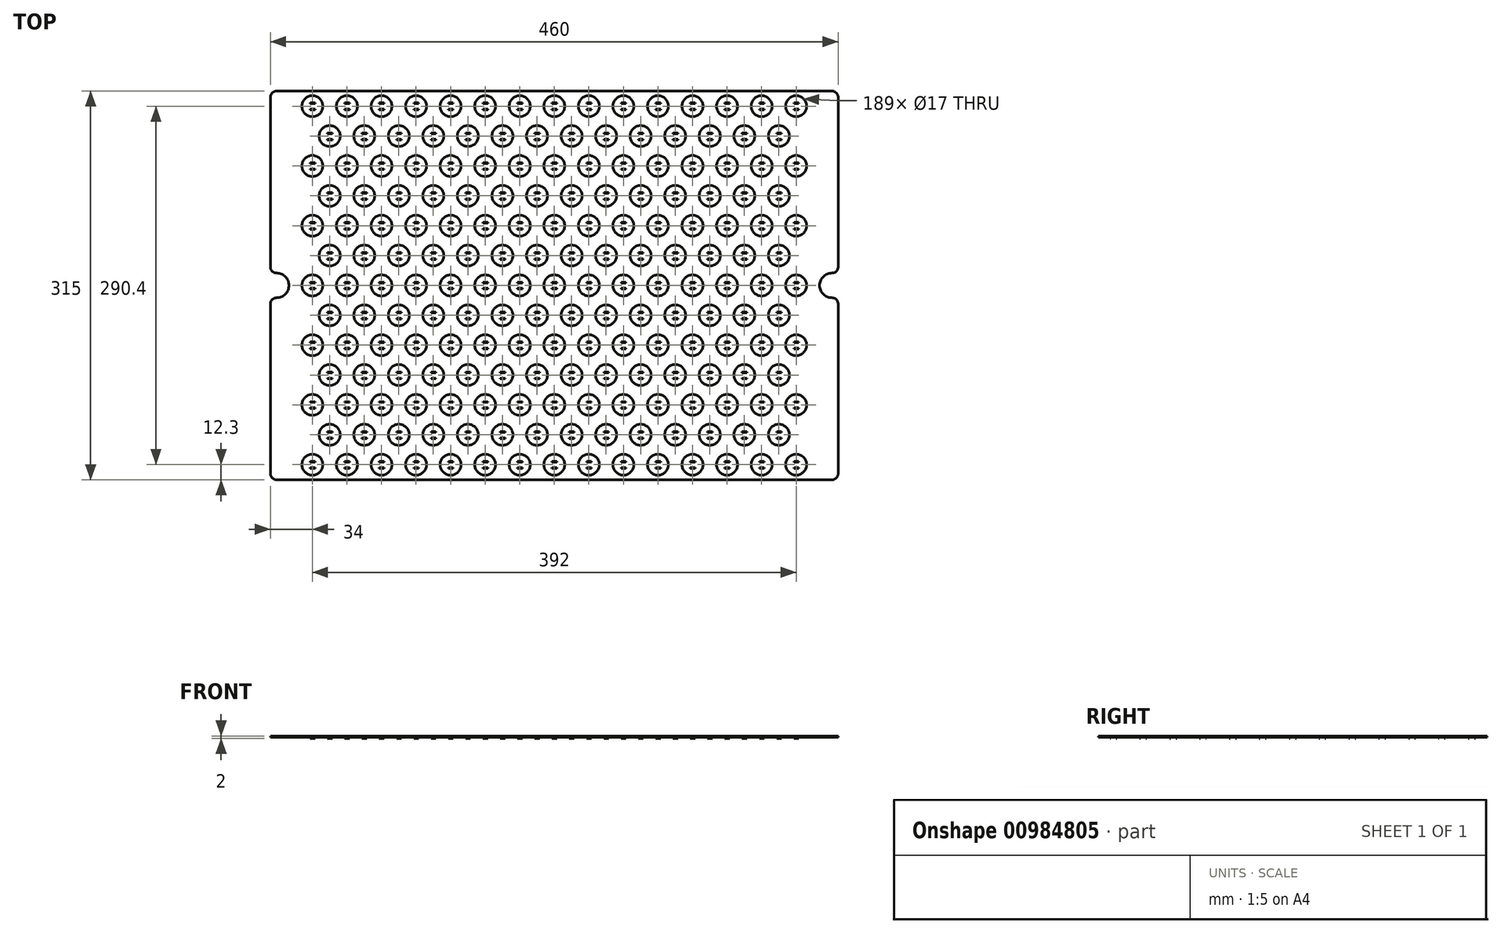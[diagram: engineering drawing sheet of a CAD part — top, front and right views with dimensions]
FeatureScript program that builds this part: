
annotation { "Feature Type Name" : "Feature", "Feature Type Description" : "" }
export const myFeature = defineFeature(function(context is Context, id is Id, definition is map)
    precondition{}
    {
        {
            var Q0;
            Q0=qCreatedBy(makeId("Top.planeOp"),FACE);
            var sketch = newSketch(context, id + "F0", { "sketchPlane" : qUnion([Q0])});
            skLineSegment(sketch, "E0.bottom", {"start": v(-225, 157.5) * mm, "end": v(225, 157.5) * mm});
            skLineSegment(sketch, "E0.top", {"start": v(-225, -157.5) * mm, "end": v(225, -157.5) * mm});
            skLineSegment(sketch, "E0.left", {"start": v(-230, 152.5) * mm, "end": v(-230, 15) * mm});
            skLineSegment(sketch, "E0.right", {"start": v(230, 152.5) * mm, "end": v(230, 15) * mm});
            skPoint(sketch, "E1.visualSharp", {"position": v(-230, 157.5) * mm});
            skArc(sketch, "E1.filletArc", {"start": v(-225, 157.5) * mm, "mid": v(-228.54, 156.04) * mm, "end": v(-230, 152.5) * mm});
            skPoint(sketch, "E2.visualSharp", {"position": v(230, 157.5) * mm});
            skArc(sketch, "E2.filletArc", {"start": v(230, 152.5) * mm, "mid": v(228.54, 156.04) * mm, "end": v(225, 157.5) * mm});
            skPoint(sketch, "E3.visualSharp", {"position": v(230, -157.5) * mm});
            skArc(sketch, "E3.filletArc", {"start": v(225, -157.5) * mm, "mid": v(228.54, -156.04) * mm, "end": v(230, -152.5) * mm});
            skPoint(sketch, "E4.visualSharp", {"position": v(-230, -157.5) * mm});
            skArc(sketch, "E4.filletArc", {"start": v(-230, -152.5) * mm, "mid": v(-228.54, -156.04) * mm, "end": v(-225, -157.5) * mm});
            skArc(sketch, "E5", {"start": v(-225, 10) * mm, "mid": v(-215, 0) * mm, "end": v(-225, -10) * mm});
            skArc(sketch, "E6", {"start": v(225, 10) * mm, "mid": v(215, 0) * mm, "end": v(225, -10) * mm});
            skLineSegment(sketch, "E7.trimOffspring", {"start": v(-230, -15) * mm, "end": v(-230, -152.5) * mm});
            skLineSegment(sketch, "E8.trimOffspring", {"start": v(230, -15) * mm, "end": v(230, -152.5) * mm});
            skPoint(sketch, "E9.visualSharp", {"position": v(230, 8.66) * mm});
            skArc(sketch, "E9.filletArc", {"start": v(225, 10) * mm, "mid": v(228.54, 11.46) * mm, "end": v(230, 15) * mm});
            skPoint(sketch, "E10.visualSharp", {"position": v(230, -8.66) * mm});
            skArc(sketch, "E10.filletArc", {"start": v(230, -15) * mm, "mid": v(228.54, -11.46) * mm, "end": v(225, -10) * mm});
            skPoint(sketch, "E11.visualSharp", {"position": v(-230, 8.66) * mm});
            skArc(sketch, "E11.filletArc", {"start": v(-230, 15) * mm, "mid": v(-228.54, 11.46) * mm, "end": v(-225, 10) * mm});
            skPoint(sketch, "E12.visualSharp", {"position": v(-230, -8.66) * mm});
            skArc(sketch, "E12.filletArc", {"start": v(-225, -10) * mm, "mid": v(-228.54, -11.46) * mm, "end": v(-230, -15) * mm});
            skCircle(sketch, "E13", {"center": v(-196, 145.2) * mm, "radius": 8.5 * mm});
            skCircle(sketch, "E14", {"center": v(-182, 121) * mm, "radius": 8.5 * mm});
            skCircle(sketch, "E15.0.1.0", {"center": v(-196, 96.8) * mm, "radius": 8.5 * mm});
            skCircle(sketch, "E15.0.2.0", {"center": v(-196, 48.4) * mm, "radius": 8.5 * mm});
            skCircle(sketch, "E15.0.3.0", {"center": v(-196, 0) * mm, "radius": 8.5 * mm});
            skCircle(sketch, "E15.0.4.0", {"center": v(-196, -48.4) * mm, "radius": 8.5 * mm});
            skCircle(sketch, "E15.0.5.0", {"center": v(-196, -96.8) * mm, "radius": 8.5 * mm});
            skCircle(sketch, "E15.0.6.0", {"center": v(-196, -145.2) * mm, "radius": 8.5 * mm});
            skCircle(sketch, "E15.1.0.0", {"center": v(-168, 145.2) * mm, "radius": 8.5 * mm});
            skCircle(sketch, "E15.1.1.0", {"center": v(-168, 96.8) * mm, "radius": 8.5 * mm});
            skCircle(sketch, "E15.1.2.0", {"center": v(-168, 48.4) * mm, "radius": 8.5 * mm});
            skCircle(sketch, "E15.1.3.0", {"center": v(-168, 0) * mm, "radius": 8.5 * mm});
            skCircle(sketch, "E15.1.4.0", {"center": v(-168, -48.4) * mm, "radius": 8.5 * mm});
            skCircle(sketch, "E15.1.5.0", {"center": v(-168, -96.8) * mm, "radius": 8.5 * mm});
            skCircle(sketch, "E15.1.6.0", {"center": v(-168, -145.2) * mm, "radius": 8.5 * mm});
            skCircle(sketch, "E15.2.0.0", {"center": v(-140, 145.2) * mm, "radius": 8.5 * mm});
            skCircle(sketch, "E15.2.1.0", {"center": v(-140, 96.8) * mm, "radius": 8.5 * mm});
            skCircle(sketch, "E15.2.2.0", {"center": v(-140, 48.4) * mm, "radius": 8.5 * mm});
            skCircle(sketch, "E15.2.3.0", {"center": v(-140, 0) * mm, "radius": 8.5 * mm});
            skCircle(sketch, "E15.2.4.0", {"center": v(-140, -48.4) * mm, "radius": 8.5 * mm});
            skCircle(sketch, "E15.2.5.0", {"center": v(-140, -96.8) * mm, "radius": 8.5 * mm});
            skCircle(sketch, "E15.2.6.0", {"center": v(-140, -145.2) * mm, "radius": 8.5 * mm});
            skCircle(sketch, "E15.3.0.0", {"center": v(-112, 145.2) * mm, "radius": 8.5 * mm});
            skCircle(sketch, "E15.3.1.0", {"center": v(-112, 96.8) * mm, "radius": 8.5 * mm});
            skCircle(sketch, "E15.3.2.0", {"center": v(-112, 48.4) * mm, "radius": 8.5 * mm});
            skCircle(sketch, "E15.3.3.0", {"center": v(-112, 0) * mm, "radius": 8.5 * mm});
            skCircle(sketch, "E15.3.4.0", {"center": v(-112, -48.4) * mm, "radius": 8.5 * mm});
            skCircle(sketch, "E15.3.5.0", {"center": v(-112, -96.8) * mm, "radius": 8.5 * mm});
            skCircle(sketch, "E15.3.6.0", {"center": v(-112, -145.2) * mm, "radius": 8.5 * mm});
            skCircle(sketch, "E15.4.0.0", {"center": v(-84, 145.2) * mm, "radius": 8.5 * mm});
            skCircle(sketch, "E15.4.1.0", {"center": v(-84, 96.8) * mm, "radius": 8.5 * mm});
            skCircle(sketch, "E15.4.2.0", {"center": v(-84, 48.4) * mm, "radius": 8.5 * mm});
            skCircle(sketch, "E15.4.3.0", {"center": v(-84, 0) * mm, "radius": 8.5 * mm});
            skCircle(sketch, "E15.4.4.0", {"center": v(-84, -48.4) * mm, "radius": 8.5 * mm});
            skCircle(sketch, "E15.4.5.0", {"center": v(-84, -96.8) * mm, "radius": 8.5 * mm});
            skCircle(sketch, "E15.4.6.0", {"center": v(-84, -145.2) * mm, "radius": 8.5 * mm});
            skCircle(sketch, "E15.5.0.0", {"center": v(-56, 145.2) * mm, "radius": 8.5 * mm});
            skCircle(sketch, "E15.5.1.0", {"center": v(-56, 96.8) * mm, "radius": 8.5 * mm});
            skCircle(sketch, "E15.5.2.0", {"center": v(-56, 48.4) * mm, "radius": 8.5 * mm});
            skCircle(sketch, "E15.5.3.0", {"center": v(-56, 0) * mm, "radius": 8.5 * mm});
            skCircle(sketch, "E15.5.4.0", {"center": v(-56, -48.4) * mm, "radius": 8.5 * mm});
            skCircle(sketch, "E15.5.5.0", {"center": v(-56, -96.8) * mm, "radius": 8.5 * mm});
            skCircle(sketch, "E15.5.6.0", {"center": v(-56, -145.2) * mm, "radius": 8.5 * mm});
            skCircle(sketch, "E15.6.0.0", {"center": v(-28, 145.2) * mm, "radius": 8.5 * mm});
            skCircle(sketch, "E15.6.1.0", {"center": v(-28, 96.8) * mm, "radius": 8.5 * mm});
            skCircle(sketch, "E15.6.2.0", {"center": v(-28, 48.4) * mm, "radius": 8.5 * mm});
            skCircle(sketch, "E15.6.3.0", {"center": v(-28, 0) * mm, "radius": 8.5 * mm});
            skCircle(sketch, "E15.6.4.0", {"center": v(-28, -48.4) * mm, "radius": 8.5 * mm});
            skCircle(sketch, "E15.6.5.0", {"center": v(-28, -96.8) * mm, "radius": 8.5 * mm});
            skCircle(sketch, "E15.6.6.0", {"center": v(-28, -145.2) * mm, "radius": 8.5 * mm});
            skCircle(sketch, "E15.7.0.0", {"center": v(0, 145.2) * mm, "radius": 8.5 * mm});
            skCircle(sketch, "E15.7.1.0", {"center": v(0, 96.8) * mm, "radius": 8.5 * mm});
            skCircle(sketch, "E15.7.2.0", {"center": v(0, 48.4) * mm, "radius": 8.5 * mm});
            skCircle(sketch, "E15.7.3.0", {"center": v(0, 0) * mm, "radius": 8.5 * mm});
            skCircle(sketch, "E15.7.4.0", {"center": v(0, -48.4) * mm, "radius": 8.5 * mm});
            skCircle(sketch, "E15.7.5.0", {"center": v(0, -96.8) * mm, "radius": 8.5 * mm});
            skCircle(sketch, "E15.7.6.0", {"center": v(0, -145.2) * mm, "radius": 8.5 * mm});
            skCircle(sketch, "E15.8.0.0", {"center": v(28, 145.2) * mm, "radius": 8.5 * mm});
            skCircle(sketch, "E15.8.1.0", {"center": v(28, 96.8) * mm, "radius": 8.5 * mm});
            skCircle(sketch, "E15.8.2.0", {"center": v(28, 48.4) * mm, "radius": 8.5 * mm});
            skCircle(sketch, "E15.8.3.0", {"center": v(28, 0) * mm, "radius": 8.5 * mm});
            skCircle(sketch, "E15.8.4.0", {"center": v(28, -48.4) * mm, "radius": 8.5 * mm});
            skCircle(sketch, "E15.8.5.0", {"center": v(28, -96.8) * mm, "radius": 8.5 * mm});
            skCircle(sketch, "E15.8.6.0", {"center": v(28, -145.2) * mm, "radius": 8.5 * mm});
            skCircle(sketch, "E15.9.0.0", {"center": v(56, 145.2) * mm, "radius": 8.5 * mm});
            skCircle(sketch, "E15.9.1.0", {"center": v(56, 96.8) * mm, "radius": 8.5 * mm});
            skCircle(sketch, "E15.9.2.0", {"center": v(56, 48.4) * mm, "radius": 8.5 * mm});
            skCircle(sketch, "E15.9.3.0", {"center": v(56, 0) * mm, "radius": 8.5 * mm});
            skCircle(sketch, "E15.9.4.0", {"center": v(56, -48.4) * mm, "radius": 8.5 * mm});
            skCircle(sketch, "E15.9.5.0", {"center": v(56, -96.8) * mm, "radius": 8.5 * mm});
            skCircle(sketch, "E15.9.6.0", {"center": v(56, -145.2) * mm, "radius": 8.5 * mm});
            skCircle(sketch, "E15.10.0.0", {"center": v(84, 145.2) * mm, "radius": 8.5 * mm});
            skCircle(sketch, "E15.10.1.0", {"center": v(84, 96.8) * mm, "radius": 8.5 * mm});
            skCircle(sketch, "E15.10.2.0", {"center": v(84, 48.4) * mm, "radius": 8.5 * mm});
            skCircle(sketch, "E15.10.3.0", {"center": v(84, 0) * mm, "radius": 8.5 * mm});
            skCircle(sketch, "E15.10.4.0", {"center": v(84, -48.4) * mm, "radius": 8.5 * mm});
            skCircle(sketch, "E15.10.5.0", {"center": v(84, -96.8) * mm, "radius": 8.5 * mm});
            skCircle(sketch, "E15.10.6.0", {"center": v(84, -145.2) * mm, "radius": 8.5 * mm});
            skCircle(sketch, "E15.11.0.0", {"center": v(112, 145.2) * mm, "radius": 8.5 * mm});
            skCircle(sketch, "E15.11.1.0", {"center": v(112, 96.8) * mm, "radius": 8.5 * mm});
            skCircle(sketch, "E15.11.2.0", {"center": v(112, 48.4) * mm, "radius": 8.5 * mm});
            skCircle(sketch, "E15.11.3.0", {"center": v(112, 0) * mm, "radius": 8.5 * mm});
            skCircle(sketch, "E15.11.4.0", {"center": v(112, -48.4) * mm, "radius": 8.5 * mm});
            skCircle(sketch, "E15.11.5.0", {"center": v(112, -96.8) * mm, "radius": 8.5 * mm});
            skCircle(sketch, "E15.11.6.0", {"center": v(112, -145.2) * mm, "radius": 8.5 * mm});
            skCircle(sketch, "E15.12.0.0", {"center": v(140, 145.2) * mm, "radius": 8.5 * mm});
            skCircle(sketch, "E15.12.1.0", {"center": v(140, 96.8) * mm, "radius": 8.5 * mm});
            skCircle(sketch, "E15.12.2.0", {"center": v(140, 48.4) * mm, "radius": 8.5 * mm});
            skCircle(sketch, "E15.12.3.0", {"center": v(140, 0) * mm, "radius": 8.5 * mm});
            skCircle(sketch, "E15.12.4.0", {"center": v(140, -48.4) * mm, "radius": 8.5 * mm});
            skCircle(sketch, "E15.12.5.0", {"center": v(140, -96.8) * mm, "radius": 8.5 * mm});
            skCircle(sketch, "E15.12.6.0", {"center": v(140, -145.2) * mm, "radius": 8.5 * mm});
            skCircle(sketch, "E15.13.0.0", {"center": v(168, 145.2) * mm, "radius": 8.5 * mm});
            skCircle(sketch, "E15.13.1.0", {"center": v(168, 96.8) * mm, "radius": 8.5 * mm});
            skCircle(sketch, "E15.13.2.0", {"center": v(168, 48.4) * mm, "radius": 8.5 * mm});
            skCircle(sketch, "E15.13.3.0", {"center": v(168, 0) * mm, "radius": 8.5 * mm});
            skCircle(sketch, "E15.13.4.0", {"center": v(168, -48.4) * mm, "radius": 8.5 * mm});
            skCircle(sketch, "E15.13.5.0", {"center": v(168, -96.8) * mm, "radius": 8.5 * mm});
            skCircle(sketch, "E15.13.6.0", {"center": v(168, -145.2) * mm, "radius": 8.5 * mm});
            skCircle(sketch, "E15.14.0.0", {"center": v(196, 145.2) * mm, "radius": 8.5 * mm});
            skCircle(sketch, "E15.14.1.0", {"center": v(196, 96.8) * mm, "radius": 8.5 * mm});
            skCircle(sketch, "E15.14.2.0", {"center": v(196, 48.4) * mm, "radius": 8.5 * mm});
            skCircle(sketch, "E15.14.3.0", {"center": v(196, 0) * mm, "radius": 8.5 * mm});
            skCircle(sketch, "E15.14.4.0", {"center": v(196, -48.4) * mm, "radius": 8.5 * mm});
            skCircle(sketch, "E15.14.5.0", {"center": v(196, -96.8) * mm, "radius": 8.5 * mm});
            skCircle(sketch, "E15.14.6.0", {"center": v(196, -145.2) * mm, "radius": 8.5 * mm});
            skLineSegment(sketch, "E15.direction1", {"start": v(-196, 145.2) * mm, "end": v(-168, 145.2) * mm, "construction": true});
            skLineSegment(sketch, "E15.direction2", {"start": v(-196, 145.2) * mm, "end": v(-196, 96.8) * mm, "construction": true});
            skCircle(sketch, "E16.0.1.0", {"center": v(-182, 72.6) * mm, "radius": 8.5 * mm});
            skCircle(sketch, "E16.0.2.0", {"center": v(-182, 24.2) * mm, "radius": 8.5 * mm});
            skCircle(sketch, "E16.0.3.0", {"center": v(-182, -24.2) * mm, "radius": 8.5 * mm});
            skCircle(sketch, "E16.0.4.0", {"center": v(-182, -72.6) * mm, "radius": 8.5 * mm});
            skCircle(sketch, "E16.0.5.0", {"center": v(-182, -121) * mm, "radius": 8.5 * mm});
            skCircle(sketch, "E16.1.0.0", {"center": v(-154, 121) * mm, "radius": 8.5 * mm});
            skCircle(sketch, "E16.1.1.0", {"center": v(-154, 72.6) * mm, "radius": 8.5 * mm});
            skCircle(sketch, "E16.1.2.0", {"center": v(-154, 24.2) * mm, "radius": 8.5 * mm});
            skCircle(sketch, "E16.1.3.0", {"center": v(-154, -24.2) * mm, "radius": 8.5 * mm});
            skCircle(sketch, "E16.1.4.0", {"center": v(-154, -72.6) * mm, "radius": 8.5 * mm});
            skCircle(sketch, "E16.1.5.0", {"center": v(-154, -121) * mm, "radius": 8.5 * mm});
            skCircle(sketch, "E16.2.0.0", {"center": v(-126, 121) * mm, "radius": 8.5 * mm});
            skCircle(sketch, "E16.2.1.0", {"center": v(-126, 72.6) * mm, "radius": 8.5 * mm});
            skCircle(sketch, "E16.2.2.0", {"center": v(-126, 24.2) * mm, "radius": 8.5 * mm});
            skCircle(sketch, "E16.2.3.0", {"center": v(-126, -24.2) * mm, "radius": 8.5 * mm});
            skCircle(sketch, "E16.2.4.0", {"center": v(-126, -72.6) * mm, "radius": 8.5 * mm});
            skCircle(sketch, "E16.2.5.0", {"center": v(-126, -121) * mm, "radius": 8.5 * mm});
            skCircle(sketch, "E16.3.0.0", {"center": v(-98, 121) * mm, "radius": 8.5 * mm});
            skCircle(sketch, "E16.3.1.0", {"center": v(-98, 72.6) * mm, "radius": 8.5 * mm});
            skCircle(sketch, "E16.3.2.0", {"center": v(-98, 24.2) * mm, "radius": 8.5 * mm});
            skCircle(sketch, "E16.3.3.0", {"center": v(-98, -24.2) * mm, "radius": 8.5 * mm});
            skCircle(sketch, "E16.3.4.0", {"center": v(-98, -72.6) * mm, "radius": 8.5 * mm});
            skCircle(sketch, "E16.3.5.0", {"center": v(-98, -121) * mm, "radius": 8.5 * mm});
            skCircle(sketch, "E16.4.0.0", {"center": v(-70, 121) * mm, "radius": 8.5 * mm});
            skCircle(sketch, "E16.4.1.0", {"center": v(-70, 72.6) * mm, "radius": 8.5 * mm});
            skCircle(sketch, "E16.4.2.0", {"center": v(-70, 24.2) * mm, "radius": 8.5 * mm});
            skCircle(sketch, "E16.4.3.0", {"center": v(-70, -24.2) * mm, "radius": 8.5 * mm});
            skCircle(sketch, "E16.4.4.0", {"center": v(-70, -72.6) * mm, "radius": 8.5 * mm});
            skCircle(sketch, "E16.4.5.0", {"center": v(-70, -121) * mm, "radius": 8.5 * mm});
            skCircle(sketch, "E16.5.0.0", {"center": v(-42, 121) * mm, "radius": 8.5 * mm});
            skCircle(sketch, "E16.5.1.0", {"center": v(-42, 72.6) * mm, "radius": 8.5 * mm});
            skCircle(sketch, "E16.5.2.0", {"center": v(-42, 24.2) * mm, "radius": 8.5 * mm});
            skCircle(sketch, "E16.5.3.0", {"center": v(-42, -24.2) * mm, "radius": 8.5 * mm});
            skCircle(sketch, "E16.5.4.0", {"center": v(-42, -72.6) * mm, "radius": 8.5 * mm});
            skCircle(sketch, "E16.5.5.0", {"center": v(-42, -121) * mm, "radius": 8.5 * mm});
            skCircle(sketch, "E16.6.0.0", {"center": v(-14, 121) * mm, "radius": 8.5 * mm});
            skCircle(sketch, "E16.6.1.0", {"center": v(-14, 72.6) * mm, "radius": 8.5 * mm});
            skCircle(sketch, "E16.6.2.0", {"center": v(-14, 24.2) * mm, "radius": 8.5 * mm});
            skCircle(sketch, "E16.6.3.0", {"center": v(-14, -24.2) * mm, "radius": 8.5 * mm});
            skCircle(sketch, "E16.6.4.0", {"center": v(-14, -72.6) * mm, "radius": 8.5 * mm});
            skCircle(sketch, "E16.6.5.0", {"center": v(-14, -121) * mm, "radius": 8.5 * mm});
            skCircle(sketch, "E16.7.0.0", {"center": v(14, 121) * mm, "radius": 8.5 * mm});
            skCircle(sketch, "E16.7.1.0", {"center": v(14, 72.6) * mm, "radius": 8.5 * mm});
            skCircle(sketch, "E16.7.2.0", {"center": v(14, 24.2) * mm, "radius": 8.5 * mm});
            skCircle(sketch, "E16.7.3.0", {"center": v(14, -24.2) * mm, "radius": 8.5 * mm});
            skCircle(sketch, "E16.7.4.0", {"center": v(14, -72.6) * mm, "radius": 8.5 * mm});
            skCircle(sketch, "E16.7.5.0", {"center": v(14, -121) * mm, "radius": 8.5 * mm});
            skCircle(sketch, "E16.8.0.0", {"center": v(42, 121) * mm, "radius": 8.5 * mm});
            skCircle(sketch, "E16.8.1.0", {"center": v(42, 72.6) * mm, "radius": 8.5 * mm});
            skCircle(sketch, "E16.8.2.0", {"center": v(42, 24.2) * mm, "radius": 8.5 * mm});
            skCircle(sketch, "E16.8.3.0", {"center": v(42, -24.2) * mm, "radius": 8.5 * mm});
            skCircle(sketch, "E16.8.4.0", {"center": v(42, -72.6) * mm, "radius": 8.5 * mm});
            skCircle(sketch, "E16.8.5.0", {"center": v(42, -121) * mm, "radius": 8.5 * mm});
            skCircle(sketch, "E16.9.0.0", {"center": v(70, 121) * mm, "radius": 8.5 * mm});
            skCircle(sketch, "E16.9.1.0", {"center": v(70, 72.6) * mm, "radius": 8.5 * mm});
            skCircle(sketch, "E16.9.2.0", {"center": v(70, 24.2) * mm, "radius": 8.5 * mm});
            skCircle(sketch, "E16.9.3.0", {"center": v(70, -24.2) * mm, "radius": 8.5 * mm});
            skCircle(sketch, "E16.9.4.0", {"center": v(70, -72.6) * mm, "radius": 8.5 * mm});
            skCircle(sketch, "E16.9.5.0", {"center": v(70, -121) * mm, "radius": 8.5 * mm});
            skCircle(sketch, "E16.10.0.0", {"center": v(98, 121) * mm, "radius": 8.5 * mm});
            skCircle(sketch, "E16.10.1.0", {"center": v(98, 72.6) * mm, "radius": 8.5 * mm});
            skCircle(sketch, "E16.10.2.0", {"center": v(98, 24.2) * mm, "radius": 8.5 * mm});
            skCircle(sketch, "E16.10.3.0", {"center": v(98, -24.2) * mm, "radius": 8.5 * mm});
            skCircle(sketch, "E16.10.4.0", {"center": v(98, -72.6) * mm, "radius": 8.5 * mm});
            skCircle(sketch, "E16.10.5.0", {"center": v(98, -121) * mm, "radius": 8.5 * mm});
            skCircle(sketch, "E16.11.0.0", {"center": v(126, 121) * mm, "radius": 8.5 * mm});
            skCircle(sketch, "E16.11.1.0", {"center": v(126, 72.6) * mm, "radius": 8.5 * mm});
            skCircle(sketch, "E16.11.2.0", {"center": v(126, 24.2) * mm, "radius": 8.5 * mm});
            skCircle(sketch, "E16.11.3.0", {"center": v(126, -24.2) * mm, "radius": 8.5 * mm});
            skCircle(sketch, "E16.11.4.0", {"center": v(126, -72.6) * mm, "radius": 8.5 * mm});
            skCircle(sketch, "E16.11.5.0", {"center": v(126, -121) * mm, "radius": 8.5 * mm});
            skCircle(sketch, "E16.12.0.0", {"center": v(154, 121) * mm, "radius": 8.5 * mm});
            skCircle(sketch, "E16.12.1.0", {"center": v(154, 72.6) * mm, "radius": 8.5 * mm});
            skCircle(sketch, "E16.12.2.0", {"center": v(154, 24.2) * mm, "radius": 8.5 * mm});
            skCircle(sketch, "E16.12.3.0", {"center": v(154, -24.2) * mm, "radius": 8.5 * mm});
            skCircle(sketch, "E16.12.4.0", {"center": v(154, -72.6) * mm, "radius": 8.5 * mm});
            skCircle(sketch, "E16.12.5.0", {"center": v(154, -121) * mm, "radius": 8.5 * mm});
            skCircle(sketch, "E16.13.0.0", {"center": v(182, 121) * mm, "radius": 8.5 * mm});
            skCircle(sketch, "E16.13.1.0", {"center": v(182, 72.6) * mm, "radius": 8.5 * mm});
            skCircle(sketch, "E16.13.2.0", {"center": v(182, 24.2) * mm, "radius": 8.5 * mm});
            skCircle(sketch, "E16.13.3.0", {"center": v(182, -24.2) * mm, "radius": 8.5 * mm});
            skCircle(sketch, "E16.13.4.0", {"center": v(182, -72.6) * mm, "radius": 8.5 * mm});
            skCircle(sketch, "E16.13.5.0", {"center": v(182, -121) * mm, "radius": 8.5 * mm});
            skLineSegment(sketch, "E16.direction1", {"start": v(-182, 121) * mm, "end": v(-154, 121) * mm, "construction": true});
            skLineSegment(sketch, "E16.direction2", {"start": v(-182, 121) * mm, "end": v(-182, 72.6) * mm, "construction": true});
            skSolve(sketch);
        }
        {
            var Q0;
            Q0=makeQuery(id+"F0.imprint","IMPRINT",FACE,{"disambiguationData":[TD([[makeQuery(id+"F0.imprint","IMPRINT",EDGE,{"derivedFrom":sQuery(id+"F0.wireOp",EDGE,"E0.bottom")}),-1.0]])]});
            extrude(context, id + "F1", {"entities" : qUnion([Q0]), "depth" : 1 * mm, "offsetDistance" : 25 * mm});
        }
        {
            var Q0;
            Q0=makeQuery(id+"F1.opExtrude","CAP_FACE",FACE,{"disambiguationData":[OSD([sQuery(id+"F0.wireOp",EDGE,"E0.bottom"),sQuery(id+"F0.wireOp",EDGE,"E0.top"),sQuery(id+"F0.wireOp",EDGE,"E0.left"),sQuery(id+"F0.wireOp",EDGE,"E0.right"),sQuery(id+"F0.wireOp",EDGE,"E1.filletArc"),sQuery(id+"F0.wireOp",EDGE,"E2.filletArc"),sQuery(id+"F0.wireOp",EDGE,"E3.filletArc"),sQuery(id+"F0.wireOp",EDGE,"E4.filletArc"),sQuery(id+"F0.wireOp",EDGE,"E5"),sQuery(id+"F0.wireOp",EDGE,"E6"),sQuery(id+"F0.wireOp",EDGE,"E7.trimOffspring"),sQuery(id+"F0.wireOp",EDGE,"E8.trimOffspring"),sQuery(id+"F0.wireOp",EDGE,"E9.filletArc"),sQuery(id+"F0.wireOp",EDGE,"E10.filletArc"),sQuery(id+"F0.wireOp",EDGE,"E11.filletArc"),sQuery(id+"F0.wireOp",EDGE,"E12.filletArc"),sQuery(id+"F0.wireOp",EDGE,"E13"),sQuery(id+"F0.wireOp",EDGE,"E14"),sQuery(id+"F0.wireOp",EDGE,"E15.0.1.0"),sQuery(id+"F0.wireOp",EDGE,"E15.0.2.0"),sQuery(id+"F0.wireOp",EDGE,"E15.0.3.0"),sQuery(id+"F0.wireOp",EDGE,"E15.0.4.0"),sQuery(id+"F0.wireOp",EDGE,"E15.0.5.0"),sQuery(id+"F0.wireOp",EDGE,"E15.0.6.0"),sQuery(id+"F0.wireOp",EDGE,"E15.1.0.0"),sQuery(id+"F0.wireOp",EDGE,"E15.1.1.0"),sQuery(id+"F0.wireOp",EDGE,"E15.1.2.0"),sQuery(id+"F0.wireOp",EDGE,"E15.1.3.0"),sQuery(id+"F0.wireOp",EDGE,"E15.1.4.0"),sQuery(id+"F0.wireOp",EDGE,"E15.1.5.0"),sQuery(id+"F0.wireOp",EDGE,"E15.1.6.0"),sQuery(id+"F0.wireOp",EDGE,"E15.2.0.0"),sQuery(id+"F0.wireOp",EDGE,"E15.2.1.0"),sQuery(id+"F0.wireOp",EDGE,"E15.2.2.0"),sQuery(id+"F0.wireOp",EDGE,"E15.2.3.0"),sQuery(id+"F0.wireOp",EDGE,"E15.2.4.0"),sQuery(id+"F0.wireOp",EDGE,"E15.2.5.0"),sQuery(id+"F0.wireOp",EDGE,"E15.2.6.0"),sQuery(id+"F0.wireOp",EDGE,"E15.3.0.0"),sQuery(id+"F0.wireOp",EDGE,"E15.3.1.0"),sQuery(id+"F0.wireOp",EDGE,"E15.3.2.0"),sQuery(id+"F0.wireOp",EDGE,"E15.3.3.0"),sQuery(id+"F0.wireOp",EDGE,"E15.3.4.0"),sQuery(id+"F0.wireOp",EDGE,"E15.3.5.0"),sQuery(id+"F0.wireOp",EDGE,"E15.3.6.0"),sQuery(id+"F0.wireOp",EDGE,"E15.4.0.0"),sQuery(id+"F0.wireOp",EDGE,"E15.4.1.0"),sQuery(id+"F0.wireOp",EDGE,"E15.4.2.0"),sQuery(id+"F0.wireOp",EDGE,"E15.4.3.0"),sQuery(id+"F0.wireOp",EDGE,"E15.4.4.0"),sQuery(id+"F0.wireOp",EDGE,"E15.4.5.0"),sQuery(id+"F0.wireOp",EDGE,"E15.4.6.0"),sQuery(id+"F0.wireOp",EDGE,"E15.5.0.0"),sQuery(id+"F0.wireOp",EDGE,"E15.5.1.0"),sQuery(id+"F0.wireOp",EDGE,"E15.5.2.0"),sQuery(id+"F0.wireOp",EDGE,"E15.5.3.0"),sQuery(id+"F0.wireOp",EDGE,"E15.5.4.0"),sQuery(id+"F0.wireOp",EDGE,"E15.5.5.0"),sQuery(id+"F0.wireOp",EDGE,"E15.5.6.0"),sQuery(id+"F0.wireOp",EDGE,"E15.6.0.0"),sQuery(id+"F0.wireOp",EDGE,"E15.6.1.0"),sQuery(id+"F0.wireOp",EDGE,"E15.6.2.0"),sQuery(id+"F0.wireOp",EDGE,"E15.6.3.0"),sQuery(id+"F0.wireOp",EDGE,"E15.6.4.0"),sQuery(id+"F0.wireOp",EDGE,"E15.6.5.0"),sQuery(id+"F0.wireOp",EDGE,"E15.6.6.0"),sQuery(id+"F0.wireOp",EDGE,"E15.7.0.0"),sQuery(id+"F0.wireOp",EDGE,"E15.7.1.0"),sQuery(id+"F0.wireOp",EDGE,"E15.7.2.0"),sQuery(id+"F0.wireOp",EDGE,"E15.7.3.0"),sQuery(id+"F0.wireOp",EDGE,"E15.7.4.0"),sQuery(id+"F0.wireOp",EDGE,"E15.7.5.0"),sQuery(id+"F0.wireOp",EDGE,"E15.7.6.0"),sQuery(id+"F0.wireOp",EDGE,"E15.8.0.0"),sQuery(id+"F0.wireOp",EDGE,"E15.8.1.0"),sQuery(id+"F0.wireOp",EDGE,"E15.8.2.0"),sQuery(id+"F0.wireOp",EDGE,"E15.8.3.0"),sQuery(id+"F0.wireOp",EDGE,"E15.8.4.0"),sQuery(id+"F0.wireOp",EDGE,"E15.8.5.0"),sQuery(id+"F0.wireOp",EDGE,"E15.8.6.0"),sQuery(id+"F0.wireOp",EDGE,"E15.9.0.0"),sQuery(id+"F0.wireOp",EDGE,"E15.9.1.0"),sQuery(id+"F0.wireOp",EDGE,"E15.9.2.0"),sQuery(id+"F0.wireOp",EDGE,"E15.9.3.0"),sQuery(id+"F0.wireOp",EDGE,"E15.9.4.0"),sQuery(id+"F0.wireOp",EDGE,"E15.9.5.0"),sQuery(id+"F0.wireOp",EDGE,"E15.9.6.0"),sQuery(id+"F0.wireOp",EDGE,"E15.10.0.0"),sQuery(id+"F0.wireOp",EDGE,"E15.10.1.0"),sQuery(id+"F0.wireOp",EDGE,"E15.10.2.0"),sQuery(id+"F0.wireOp",EDGE,"E15.10.3.0"),sQuery(id+"F0.wireOp",EDGE,"E15.10.4.0"),sQuery(id+"F0.wireOp",EDGE,"E15.10.5.0"),sQuery(id+"F0.wireOp",EDGE,"E15.10.6.0"),sQuery(id+"F0.wireOp",EDGE,"E15.11.0.0"),sQuery(id+"F0.wireOp",EDGE,"E15.11.1.0"),sQuery(id+"F0.wireOp",EDGE,"E15.11.2.0"),sQuery(id+"F0.wireOp",EDGE,"E15.11.3.0"),sQuery(id+"F0.wireOp",EDGE,"E15.11.4.0"),sQuery(id+"F0.wireOp",EDGE,"E15.11.5.0"),sQuery(id+"F0.wireOp",EDGE,"E15.11.6.0"),sQuery(id+"F0.wireOp",EDGE,"E15.12.0.0"),sQuery(id+"F0.wireOp",EDGE,"E15.12.1.0"),sQuery(id+"F0.wireOp",EDGE,"E15.12.2.0"),sQuery(id+"F0.wireOp",EDGE,"E15.12.3.0"),sQuery(id+"F0.wireOp",EDGE,"E15.12.4.0"),sQuery(id+"F0.wireOp",EDGE,"E15.12.5.0"),sQuery(id+"F0.wireOp",EDGE,"E15.12.6.0"),sQuery(id+"F0.wireOp",EDGE,"E15.13.0.0"),sQuery(id+"F0.wireOp",EDGE,"E15.13.1.0"),sQuery(id+"F0.wireOp",EDGE,"E15.13.2.0"),sQuery(id+"F0.wireOp",EDGE,"E15.13.3.0"),sQuery(id+"F0.wireOp",EDGE,"E15.13.4.0"),sQuery(id+"F0.wireOp",EDGE,"E15.13.5.0"),sQuery(id+"F0.wireOp",EDGE,"E15.13.6.0"),sQuery(id+"F0.wireOp",EDGE,"E15.14.0.0"),sQuery(id+"F0.wireOp",EDGE,"E15.14.1.0"),sQuery(id+"F0.wireOp",EDGE,"E15.14.2.0"),sQuery(id+"F0.wireOp",EDGE,"E15.14.3.0"),sQuery(id+"F0.wireOp",EDGE,"E15.14.4.0"),sQuery(id+"F0.wireOp",EDGE,"E15.14.5.0"),sQuery(id+"F0.wireOp",EDGE,"E15.14.6.0"),sQuery(id+"F0.wireOp",EDGE,"E16.0.1.0"),sQuery(id+"F0.wireOp",EDGE,"E16.0.2.0"),sQuery(id+"F0.wireOp",EDGE,"E16.0.3.0"),sQuery(id+"F0.wireOp",EDGE,"E16.0.4.0"),sQuery(id+"F0.wireOp",EDGE,"E16.0.5.0"),sQuery(id+"F0.wireOp",EDGE,"E16.1.0.0"),sQuery(id+"F0.wireOp",EDGE,"E16.1.1.0"),sQuery(id+"F0.wireOp",EDGE,"E16.1.2.0"),sQuery(id+"F0.wireOp",EDGE,"E16.1.3.0"),sQuery(id+"F0.wireOp",EDGE,"E16.1.4.0"),sQuery(id+"F0.wireOp",EDGE,"E16.1.5.0"),sQuery(id+"F0.wireOp",EDGE,"E16.2.0.0"),sQuery(id+"F0.wireOp",EDGE,"E16.2.1.0"),sQuery(id+"F0.wireOp",EDGE,"E16.2.2.0"),sQuery(id+"F0.wireOp",EDGE,"E16.2.3.0"),sQuery(id+"F0.wireOp",EDGE,"E16.2.4.0"),sQuery(id+"F0.wireOp",EDGE,"E16.2.5.0"),sQuery(id+"F0.wireOp",EDGE,"E16.3.0.0"),sQuery(id+"F0.wireOp",EDGE,"E16.3.1.0"),sQuery(id+"F0.wireOp",EDGE,"E16.3.2.0"),sQuery(id+"F0.wireOp",EDGE,"E16.3.3.0"),sQuery(id+"F0.wireOp",EDGE,"E16.3.4.0"),sQuery(id+"F0.wireOp",EDGE,"E16.3.5.0"),sQuery(id+"F0.wireOp",EDGE,"E16.4.0.0"),sQuery(id+"F0.wireOp",EDGE,"E16.4.1.0"),sQuery(id+"F0.wireOp",EDGE,"E16.4.2.0"),sQuery(id+"F0.wireOp",EDGE,"E16.4.3.0"),sQuery(id+"F0.wireOp",EDGE,"E16.4.4.0"),sQuery(id+"F0.wireOp",EDGE,"E16.4.5.0"),sQuery(id+"F0.wireOp",EDGE,"E16.5.0.0"),sQuery(id+"F0.wireOp",EDGE,"E16.5.1.0"),sQuery(id+"F0.wireOp",EDGE,"E16.5.2.0"),sQuery(id+"F0.wireOp",EDGE,"E16.5.3.0"),sQuery(id+"F0.wireOp",EDGE,"E16.5.4.0"),sQuery(id+"F0.wireOp",EDGE,"E16.5.5.0"),sQuery(id+"F0.wireOp",EDGE,"E16.6.0.0"),sQuery(id+"F0.wireOp",EDGE,"E16.6.1.0"),sQuery(id+"F0.wireOp",EDGE,"E16.6.2.0"),sQuery(id+"F0.wireOp",EDGE,"E16.6.3.0"),sQuery(id+"F0.wireOp",EDGE,"E16.6.4.0"),sQuery(id+"F0.wireOp",EDGE,"E16.6.5.0"),sQuery(id+"F0.wireOp",EDGE,"E16.7.0.0"),sQuery(id+"F0.wireOp",EDGE,"E16.7.1.0"),sQuery(id+"F0.wireOp",EDGE,"E16.7.2.0"),sQuery(id+"F0.wireOp",EDGE,"E16.7.3.0"),sQuery(id+"F0.wireOp",EDGE,"E16.7.4.0"),sQuery(id+"F0.wireOp",EDGE,"E16.7.5.0"),sQuery(id+"F0.wireOp",EDGE,"E16.8.0.0"),sQuery(id+"F0.wireOp",EDGE,"E16.8.1.0"),sQuery(id+"F0.wireOp",EDGE,"E16.8.2.0"),sQuery(id+"F0.wireOp",EDGE,"E16.8.3.0"),sQuery(id+"F0.wireOp",EDGE,"E16.8.4.0"),sQuery(id+"F0.wireOp",EDGE,"E16.8.5.0"),sQuery(id+"F0.wireOp",EDGE,"E16.9.0.0"),sQuery(id+"F0.wireOp",EDGE,"E16.9.1.0"),sQuery(id+"F0.wireOp",EDGE,"E16.9.2.0"),sQuery(id+"F0.wireOp",EDGE,"E16.9.3.0"),sQuery(id+"F0.wireOp",EDGE,"E16.9.4.0"),sQuery(id+"F0.wireOp",EDGE,"E16.9.5.0"),sQuery(id+"F0.wireOp",EDGE,"E16.10.0.0"),sQuery(id+"F0.wireOp",EDGE,"E16.10.1.0"),sQuery(id+"F0.wireOp",EDGE,"E16.10.2.0"),sQuery(id+"F0.wireOp",EDGE,"E16.10.3.0"),sQuery(id+"F0.wireOp",EDGE,"E16.10.4.0"),sQuery(id+"F0.wireOp",EDGE,"E16.10.5.0"),sQuery(id+"F0.wireOp",EDGE,"E16.11.0.0"),sQuery(id+"F0.wireOp",EDGE,"E16.11.1.0"),sQuery(id+"F0.wireOp",EDGE,"E16.11.2.0"),sQuery(id+"F0.wireOp",EDGE,"E16.11.3.0"),sQuery(id+"F0.wireOp",EDGE,"E16.11.4.0"),sQuery(id+"F0.wireOp",EDGE,"E16.11.5.0"),sQuery(id+"F0.wireOp",EDGE,"E16.12.0.0"),sQuery(id+"F0.wireOp",EDGE,"E16.12.1.0"),sQuery(id+"F0.wireOp",EDGE,"E16.12.2.0"),sQuery(id+"F0.wireOp",EDGE,"E16.12.3.0"),sQuery(id+"F0.wireOp",EDGE,"E16.12.4.0"),sQuery(id+"F0.wireOp",EDGE,"E16.12.5.0"),sQuery(id+"F0.wireOp",EDGE,"E16.13.0.0"),sQuery(id+"F0.wireOp",EDGE,"E16.13.1.0"),sQuery(id+"F0.wireOp",EDGE,"E16.13.2.0"),sQuery(id+"F0.wireOp",EDGE,"E16.13.3.0"),sQuery(id+"F0.wireOp",EDGE,"E16.13.4.0"),sQuery(id+"F0.wireOp",EDGE,"E16.13.5.0")])],"isStart":true});
            var sketch = newSketch(context, id + "F2", { "sketchPlane" : qUnion([Q0])});
            skLineSegment(sketch, "E17.bottom", {"start": v(198.17, -147.84) * mm, "end": v(194.17, -147.84) * mm});
            skLineSegment(sketch, "E17.top", {"start": v(198.17, -147.24) * mm, "end": v(194.17, -147.24) * mm});
            skLineSegment(sketch, "E17.left", {"start": v(198.17, -147.84) * mm, "end": v(198.17, -147.24) * mm});
            skLineSegment(sketch, "E17.right", {"start": v(194.17, -147.84) * mm, "end": v(194.17, -147.24) * mm});
            skLineSegment(sketch, "E18.bottom", {"start": v(198.17, -142.84) * mm, "end": v(194.17, -142.84) * mm});
            skLineSegment(sketch, "E18.top", {"start": v(198.17, -142.24) * mm, "end": v(194.17, -142.24) * mm});
            skLineSegment(sketch, "E18.left", {"start": v(198.17, -142.84) * mm, "end": v(198.17, -142.24) * mm});
            skLineSegment(sketch, "E18.right", {"start": v(194.17, -142.84) * mm, "end": v(194.17, -142.24) * mm});
            skLineSegment(sketch, "E19.bottom", {"start": v(184.15, -123.5) * mm, "end": v(180.15, -123.5) * mm});
            skLineSegment(sketch, "E19.top", {"start": v(184.15, -122.9) * mm, "end": v(180.15, -122.9) * mm});
            skLineSegment(sketch, "E19.left", {"start": v(184.15, -123.5) * mm, "end": v(184.15, -122.9) * mm});
            skLineSegment(sketch, "E19.right", {"start": v(180.15, -123.5) * mm, "end": v(180.15, -122.9) * mm});
            skLineSegment(sketch, "E20.bottom", {"start": v(184.15, -118.5) * mm, "end": v(180.15, -118.5) * mm});
            skLineSegment(sketch, "E20.top", {"start": v(184.15, -117.9) * mm, "end": v(180.15, -117.9) * mm});
            skLineSegment(sketch, "E20.left", {"start": v(184.15, -118.5) * mm, "end": v(184.15, -117.9) * mm});
            skLineSegment(sketch, "E20.right", {"start": v(180.15, -118.5) * mm, "end": v(180.15, -117.9) * mm});
            skLineSegment(sketch, "E21.0.1.0", {"start": v(198.17, -94.44) * mm, "end": v(194.17, -94.44) * mm});
            skLineSegment(sketch, "E21.0.1.1", {"start": v(198.17, -98.84) * mm, "end": v(194.17, -98.84) * mm});
            skLineSegment(sketch, "E21.0.1.2", {"start": v(198.17, -93.84) * mm, "end": v(194.17, -93.84) * mm});
            skLineSegment(sketch, "E21.0.1.3", {"start": v(198.17, -99.44) * mm, "end": v(194.17, -99.44) * mm});
            skLineSegment(sketch, "E21.0.1.4", {"start": v(198.17, -94.44) * mm, "end": v(198.17, -93.84) * mm});
            skLineSegment(sketch, "E21.0.1.5", {"start": v(198.17, -99.44) * mm, "end": v(198.17, -98.84) * mm});
            skLineSegment(sketch, "E21.0.1.6", {"start": v(194.17, -99.44) * mm, "end": v(194.17, -98.84) * mm});
            skLineSegment(sketch, "E21.0.1.7", {"start": v(194.17, -94.44) * mm, "end": v(194.17, -93.84) * mm});
            skLineSegment(sketch, "E21.0.2.0", {"start": v(198.17, -46.04) * mm, "end": v(194.17, -46.04) * mm});
            skLineSegment(sketch, "E21.0.2.1", {"start": v(198.17, -50.44) * mm, "end": v(194.17, -50.44) * mm});
            skLineSegment(sketch, "E21.0.2.2", {"start": v(198.17, -45.44) * mm, "end": v(194.17, -45.44) * mm});
            skLineSegment(sketch, "E21.0.2.3", {"start": v(198.17, -51.04) * mm, "end": v(194.17, -51.04) * mm});
            skLineSegment(sketch, "E21.0.2.4", {"start": v(198.17, -46.04) * mm, "end": v(198.17, -45.44) * mm});
            skLineSegment(sketch, "E21.0.2.5", {"start": v(198.17, -51.04) * mm, "end": v(198.17, -50.44) * mm});
            skLineSegment(sketch, "E21.0.2.6", {"start": v(194.17, -51.04) * mm, "end": v(194.17, -50.44) * mm});
            skLineSegment(sketch, "E21.0.2.7", {"start": v(194.17, -46.04) * mm, "end": v(194.17, -45.44) * mm});
            skLineSegment(sketch, "E21.0.3.0", {"start": v(198.17, 2.36) * mm, "end": v(194.17, 2.36) * mm});
            skLineSegment(sketch, "E21.0.3.1", {"start": v(198.17, -2.04) * mm, "end": v(194.17, -2.04) * mm});
            skLineSegment(sketch, "E21.0.3.2", {"start": v(198.17, 2.96) * mm, "end": v(194.17, 2.96) * mm});
            skLineSegment(sketch, "E21.0.3.3", {"start": v(198.17, -2.64) * mm, "end": v(194.17, -2.64) * mm});
            skLineSegment(sketch, "E21.0.3.4", {"start": v(198.17, 2.36) * mm, "end": v(198.17, 2.96) * mm});
            skLineSegment(sketch, "E21.0.3.5", {"start": v(198.17, -2.64) * mm, "end": v(198.17, -2.04) * mm});
            skLineSegment(sketch, "E21.0.3.6", {"start": v(194.17, -2.64) * mm, "end": v(194.17, -2.04) * mm});
            skLineSegment(sketch, "E21.0.3.7", {"start": v(194.17, 2.36) * mm, "end": v(194.17, 2.96) * mm});
            skLineSegment(sketch, "E21.0.4.0", {"start": v(198.17, 50.76) * mm, "end": v(194.17, 50.76) * mm});
            skLineSegment(sketch, "E21.0.4.1", {"start": v(198.17, 46.36) * mm, "end": v(194.17, 46.36) * mm});
            skLineSegment(sketch, "E21.0.4.2", {"start": v(198.17, 51.36) * mm, "end": v(194.17, 51.36) * mm});
            skLineSegment(sketch, "E21.0.4.3", {"start": v(198.17, 45.76) * mm, "end": v(194.17, 45.76) * mm});
            skLineSegment(sketch, "E21.0.4.4", {"start": v(198.17, 50.76) * mm, "end": v(198.17, 51.36) * mm});
            skLineSegment(sketch, "E21.0.4.5", {"start": v(198.17, 45.76) * mm, "end": v(198.17, 46.36) * mm});
            skLineSegment(sketch, "E21.0.4.6", {"start": v(194.17, 45.76) * mm, "end": v(194.17, 46.36) * mm});
            skLineSegment(sketch, "E21.0.4.7", {"start": v(194.17, 50.76) * mm, "end": v(194.17, 51.36) * mm});
            skLineSegment(sketch, "E21.0.5.0", {"start": v(198.17, 99.16) * mm, "end": v(194.17, 99.16) * mm});
            skLineSegment(sketch, "E21.0.5.1", {"start": v(198.17, 94.76) * mm, "end": v(194.17, 94.76) * mm});
            skLineSegment(sketch, "E21.0.5.2", {"start": v(198.17, 99.76) * mm, "end": v(194.17, 99.76) * mm});
            skLineSegment(sketch, "E21.0.5.3", {"start": v(198.17, 94.16) * mm, "end": v(194.17, 94.16) * mm});
            skLineSegment(sketch, "E21.0.5.4", {"start": v(198.17, 99.16) * mm, "end": v(198.17, 99.76) * mm});
            skLineSegment(sketch, "E21.0.5.5", {"start": v(198.17, 94.16) * mm, "end": v(198.17, 94.76) * mm});
            skLineSegment(sketch, "E21.0.5.6", {"start": v(194.17, 94.16) * mm, "end": v(194.17, 94.76) * mm});
            skLineSegment(sketch, "E21.0.5.7", {"start": v(194.17, 99.16) * mm, "end": v(194.17, 99.76) * mm});
            skLineSegment(sketch, "E21.0.6.0", {"start": v(198.17, 147.56) * mm, "end": v(194.17, 147.56) * mm});
            skLineSegment(sketch, "E21.0.6.1", {"start": v(198.17, 143.16) * mm, "end": v(194.17, 143.16) * mm});
            skLineSegment(sketch, "E21.0.6.2", {"start": v(198.17, 148.16) * mm, "end": v(194.17, 148.16) * mm});
            skLineSegment(sketch, "E21.0.6.3", {"start": v(198.17, 142.56) * mm, "end": v(194.17, 142.56) * mm});
            skLineSegment(sketch, "E21.0.6.4", {"start": v(198.17, 147.56) * mm, "end": v(198.17, 148.16) * mm});
            skLineSegment(sketch, "E21.0.6.5", {"start": v(198.17, 142.56) * mm, "end": v(198.17, 143.16) * mm});
            skLineSegment(sketch, "E21.0.6.6", {"start": v(194.17, 142.56) * mm, "end": v(194.17, 143.16) * mm});
            skLineSegment(sketch, "E21.0.6.7", {"start": v(194.17, 147.56) * mm, "end": v(194.17, 148.16) * mm});
            skLineSegment(sketch, "E21.1.0.0", {"start": v(170.17, -142.84) * mm, "end": v(166.17, -142.84) * mm});
            skLineSegment(sketch, "E21.1.0.1", {"start": v(170.17, -147.24) * mm, "end": v(166.17, -147.24) * mm});
            skLineSegment(sketch, "E21.1.0.2", {"start": v(170.17, -142.24) * mm, "end": v(166.17, -142.24) * mm});
            skLineSegment(sketch, "E21.1.0.3", {"start": v(170.17, -147.84) * mm, "end": v(166.17, -147.84) * mm});
            skLineSegment(sketch, "E21.1.0.4", {"start": v(170.17, -142.84) * mm, "end": v(170.17, -142.24) * mm});
            skLineSegment(sketch, "E21.1.0.5", {"start": v(170.17, -147.84) * mm, "end": v(170.17, -147.24) * mm});
            skLineSegment(sketch, "E21.1.0.6", {"start": v(166.17, -147.84) * mm, "end": v(166.17, -147.24) * mm});
            skLineSegment(sketch, "E21.1.0.7", {"start": v(166.17, -142.84) * mm, "end": v(166.17, -142.24) * mm});
            skLineSegment(sketch, "E21.1.1.0", {"start": v(170.17, -94.44) * mm, "end": v(166.17, -94.44) * mm});
            skLineSegment(sketch, "E21.1.1.1", {"start": v(170.17, -98.84) * mm, "end": v(166.17, -98.84) * mm});
            skLineSegment(sketch, "E21.1.1.2", {"start": v(170.17, -93.84) * mm, "end": v(166.17, -93.84) * mm});
            skLineSegment(sketch, "E21.1.1.3", {"start": v(170.17, -99.44) * mm, "end": v(166.17, -99.44) * mm});
            skLineSegment(sketch, "E21.1.1.4", {"start": v(170.17, -94.44) * mm, "end": v(170.17, -93.84) * mm});
            skLineSegment(sketch, "E21.1.1.5", {"start": v(170.17, -99.44) * mm, "end": v(170.17, -98.84) * mm});
            skLineSegment(sketch, "E21.1.1.6", {"start": v(166.17, -99.44) * mm, "end": v(166.17, -98.84) * mm});
            skLineSegment(sketch, "E21.1.1.7", {"start": v(166.17, -94.44) * mm, "end": v(166.17, -93.84) * mm});
            skLineSegment(sketch, "E21.1.2.0", {"start": v(170.17, -46.04) * mm, "end": v(166.17, -46.04) * mm});
            skLineSegment(sketch, "E21.1.2.1", {"start": v(170.17, -50.44) * mm, "end": v(166.17, -50.44) * mm});
            skLineSegment(sketch, "E21.1.2.2", {"start": v(170.17, -45.44) * mm, "end": v(166.17, -45.44) * mm});
            skLineSegment(sketch, "E21.1.2.3", {"start": v(170.17, -51.04) * mm, "end": v(166.17, -51.04) * mm});
            skLineSegment(sketch, "E21.1.2.4", {"start": v(170.17, -46.04) * mm, "end": v(170.17, -45.44) * mm});
            skLineSegment(sketch, "E21.1.2.5", {"start": v(170.17, -51.04) * mm, "end": v(170.17, -50.44) * mm});
            skLineSegment(sketch, "E21.1.2.6", {"start": v(166.17, -51.04) * mm, "end": v(166.17, -50.44) * mm});
            skLineSegment(sketch, "E21.1.2.7", {"start": v(166.17, -46.04) * mm, "end": v(166.17, -45.44) * mm});
            skLineSegment(sketch, "E21.1.3.0", {"start": v(170.17, 2.36) * mm, "end": v(166.17, 2.36) * mm});
            skLineSegment(sketch, "E21.1.3.1", {"start": v(170.17, -2.04) * mm, "end": v(166.17, -2.04) * mm});
            skLineSegment(sketch, "E21.1.3.2", {"start": v(170.17, 2.96) * mm, "end": v(166.17, 2.96) * mm});
            skLineSegment(sketch, "E21.1.3.3", {"start": v(170.17, -2.64) * mm, "end": v(166.17, -2.64) * mm});
            skLineSegment(sketch, "E21.1.3.4", {"start": v(170.17, 2.36) * mm, "end": v(170.17, 2.96) * mm});
            skLineSegment(sketch, "E21.1.3.5", {"start": v(170.17, -2.64) * mm, "end": v(170.17, -2.04) * mm});
            skLineSegment(sketch, "E21.1.3.6", {"start": v(166.17, -2.64) * mm, "end": v(166.17, -2.04) * mm});
            skLineSegment(sketch, "E21.1.3.7", {"start": v(166.17, 2.36) * mm, "end": v(166.17, 2.96) * mm});
            skLineSegment(sketch, "E21.1.4.0", {"start": v(170.17, 50.76) * mm, "end": v(166.17, 50.76) * mm});
            skLineSegment(sketch, "E21.1.4.1", {"start": v(170.17, 46.36) * mm, "end": v(166.17, 46.36) * mm});
            skLineSegment(sketch, "E21.1.4.2", {"start": v(170.17, 51.36) * mm, "end": v(166.17, 51.36) * mm});
            skLineSegment(sketch, "E21.1.4.3", {"start": v(170.17, 45.76) * mm, "end": v(166.17, 45.76) * mm});
            skLineSegment(sketch, "E21.1.4.4", {"start": v(170.17, 50.76) * mm, "end": v(170.17, 51.36) * mm});
            skLineSegment(sketch, "E21.1.4.5", {"start": v(170.17, 45.76) * mm, "end": v(170.17, 46.36) * mm});
            skLineSegment(sketch, "E21.1.4.6", {"start": v(166.17, 45.76) * mm, "end": v(166.17, 46.36) * mm});
            skLineSegment(sketch, "E21.1.4.7", {"start": v(166.17, 50.76) * mm, "end": v(166.17, 51.36) * mm});
            skLineSegment(sketch, "E21.1.5.0", {"start": v(170.17, 99.16) * mm, "end": v(166.17, 99.16) * mm});
            skLineSegment(sketch, "E21.1.5.1", {"start": v(170.17, 94.76) * mm, "end": v(166.17, 94.76) * mm});
            skLineSegment(sketch, "E21.1.5.2", {"start": v(170.17, 99.76) * mm, "end": v(166.17, 99.76) * mm});
            skLineSegment(sketch, "E21.1.5.3", {"start": v(170.17, 94.16) * mm, "end": v(166.17, 94.16) * mm});
            skLineSegment(sketch, "E21.1.5.4", {"start": v(170.17, 99.16) * mm, "end": v(170.17, 99.76) * mm});
            skLineSegment(sketch, "E21.1.5.5", {"start": v(170.17, 94.16) * mm, "end": v(170.17, 94.76) * mm});
            skLineSegment(sketch, "E21.1.5.6", {"start": v(166.17, 94.16) * mm, "end": v(166.17, 94.76) * mm});
            skLineSegment(sketch, "E21.1.5.7", {"start": v(166.17, 99.16) * mm, "end": v(166.17, 99.76) * mm});
            skLineSegment(sketch, "E21.1.6.0", {"start": v(170.17, 147.56) * mm, "end": v(166.17, 147.56) * mm});
            skLineSegment(sketch, "E21.1.6.1", {"start": v(170.17, 143.16) * mm, "end": v(166.17, 143.16) * mm});
            skLineSegment(sketch, "E21.1.6.2", {"start": v(170.17, 148.16) * mm, "end": v(166.17, 148.16) * mm});
            skLineSegment(sketch, "E21.1.6.3", {"start": v(170.17, 142.56) * mm, "end": v(166.17, 142.56) * mm});
            skLineSegment(sketch, "E21.1.6.4", {"start": v(170.17, 147.56) * mm, "end": v(170.17, 148.16) * mm});
            skLineSegment(sketch, "E21.1.6.5", {"start": v(170.17, 142.56) * mm, "end": v(170.17, 143.16) * mm});
            skLineSegment(sketch, "E21.1.6.6", {"start": v(166.17, 142.56) * mm, "end": v(166.17, 143.16) * mm});
            skLineSegment(sketch, "E21.1.6.7", {"start": v(166.17, 147.56) * mm, "end": v(166.17, 148.16) * mm});
            skLineSegment(sketch, "E21.2.0.0", {"start": v(142.17, -142.84) * mm, "end": v(138.17, -142.84) * mm});
            skLineSegment(sketch, "E21.2.0.1", {"start": v(142.17, -147.24) * mm, "end": v(138.17, -147.24) * mm});
            skLineSegment(sketch, "E21.2.0.2", {"start": v(142.17, -142.24) * mm, "end": v(138.17, -142.24) * mm});
            skLineSegment(sketch, "E21.2.0.3", {"start": v(142.17, -147.84) * mm, "end": v(138.17, -147.84) * mm});
            skLineSegment(sketch, "E21.2.0.4", {"start": v(142.17, -142.84) * mm, "end": v(142.17, -142.24) * mm});
            skLineSegment(sketch, "E21.2.0.5", {"start": v(142.17, -147.84) * mm, "end": v(142.17, -147.24) * mm});
            skLineSegment(sketch, "E21.2.0.6", {"start": v(138.17, -147.84) * mm, "end": v(138.17, -147.24) * mm});
            skLineSegment(sketch, "E21.2.0.7", {"start": v(138.17, -142.84) * mm, "end": v(138.17, -142.24) * mm});
            skLineSegment(sketch, "E21.2.1.0", {"start": v(142.17, -94.44) * mm, "end": v(138.17, -94.44) * mm});
            skLineSegment(sketch, "E21.2.1.1", {"start": v(142.17, -98.84) * mm, "end": v(138.17, -98.84) * mm});
            skLineSegment(sketch, "E21.2.1.2", {"start": v(142.17, -93.84) * mm, "end": v(138.17, -93.84) * mm});
            skLineSegment(sketch, "E21.2.1.3", {"start": v(142.17, -99.44) * mm, "end": v(138.17, -99.44) * mm});
            skLineSegment(sketch, "E21.2.1.4", {"start": v(142.17, -94.44) * mm, "end": v(142.17, -93.84) * mm});
            skLineSegment(sketch, "E21.2.1.5", {"start": v(142.17, -99.44) * mm, "end": v(142.17, -98.84) * mm});
            skLineSegment(sketch, "E21.2.1.6", {"start": v(138.17, -99.44) * mm, "end": v(138.17, -98.84) * mm});
            skLineSegment(sketch, "E21.2.1.7", {"start": v(138.17, -94.44) * mm, "end": v(138.17, -93.84) * mm});
            skLineSegment(sketch, "E21.2.2.0", {"start": v(142.17, -46.04) * mm, "end": v(138.17, -46.04) * mm});
            skLineSegment(sketch, "E21.2.2.1", {"start": v(142.17, -50.44) * mm, "end": v(138.17, -50.44) * mm});
            skLineSegment(sketch, "E21.2.2.2", {"start": v(142.17, -45.44) * mm, "end": v(138.17, -45.44) * mm});
            skLineSegment(sketch, "E21.2.2.3", {"start": v(142.17, -51.04) * mm, "end": v(138.17, -51.04) * mm});
            skLineSegment(sketch, "E21.2.2.4", {"start": v(142.17, -46.04) * mm, "end": v(142.17, -45.44) * mm});
            skLineSegment(sketch, "E21.2.2.5", {"start": v(142.17, -51.04) * mm, "end": v(142.17, -50.44) * mm});
            skLineSegment(sketch, "E21.2.2.6", {"start": v(138.17, -51.04) * mm, "end": v(138.17, -50.44) * mm});
            skLineSegment(sketch, "E21.2.2.7", {"start": v(138.17, -46.04) * mm, "end": v(138.17, -45.44) * mm});
            skLineSegment(sketch, "E21.2.3.0", {"start": v(142.17, 2.36) * mm, "end": v(138.17, 2.36) * mm});
            skLineSegment(sketch, "E21.2.3.1", {"start": v(142.17, -2.04) * mm, "end": v(138.17, -2.04) * mm});
            skLineSegment(sketch, "E21.2.3.2", {"start": v(142.17, 2.96) * mm, "end": v(138.17, 2.96) * mm});
            skLineSegment(sketch, "E21.2.3.3", {"start": v(142.17, -2.64) * mm, "end": v(138.17, -2.64) * mm});
            skLineSegment(sketch, "E21.2.3.4", {"start": v(142.17, 2.36) * mm, "end": v(142.17, 2.96) * mm});
            skLineSegment(sketch, "E21.2.3.5", {"start": v(142.17, -2.64) * mm, "end": v(142.17, -2.04) * mm});
            skLineSegment(sketch, "E21.2.3.6", {"start": v(138.17, -2.64) * mm, "end": v(138.17, -2.04) * mm});
            skLineSegment(sketch, "E21.2.3.7", {"start": v(138.17, 2.36) * mm, "end": v(138.17, 2.96) * mm});
            skLineSegment(sketch, "E21.2.4.0", {"start": v(142.17, 50.76) * mm, "end": v(138.17, 50.76) * mm});
            skLineSegment(sketch, "E21.2.4.1", {"start": v(142.17, 46.36) * mm, "end": v(138.17, 46.36) * mm});
            skLineSegment(sketch, "E21.2.4.2", {"start": v(142.17, 51.36) * mm, "end": v(138.17, 51.36) * mm});
            skLineSegment(sketch, "E21.2.4.3", {"start": v(142.17, 45.76) * mm, "end": v(138.17, 45.76) * mm});
            skLineSegment(sketch, "E21.2.4.4", {"start": v(142.17, 50.76) * mm, "end": v(142.17, 51.36) * mm});
            skLineSegment(sketch, "E21.2.4.5", {"start": v(142.17, 45.76) * mm, "end": v(142.17, 46.36) * mm});
            skLineSegment(sketch, "E21.2.4.6", {"start": v(138.17, 45.76) * mm, "end": v(138.17, 46.36) * mm});
            skLineSegment(sketch, "E21.2.4.7", {"start": v(138.17, 50.76) * mm, "end": v(138.17, 51.36) * mm});
            skLineSegment(sketch, "E21.2.5.0", {"start": v(142.17, 99.16) * mm, "end": v(138.17, 99.16) * mm});
            skLineSegment(sketch, "E21.2.5.1", {"start": v(142.17, 94.76) * mm, "end": v(138.17, 94.76) * mm});
            skLineSegment(sketch, "E21.2.5.2", {"start": v(142.17, 99.76) * mm, "end": v(138.17, 99.76) * mm});
            skLineSegment(sketch, "E21.2.5.3", {"start": v(142.17, 94.16) * mm, "end": v(138.17, 94.16) * mm});
            skLineSegment(sketch, "E21.2.5.4", {"start": v(142.17, 99.16) * mm, "end": v(142.17, 99.76) * mm});
            skLineSegment(sketch, "E21.2.5.5", {"start": v(142.17, 94.16) * mm, "end": v(142.17, 94.76) * mm});
            skLineSegment(sketch, "E21.2.5.6", {"start": v(138.17, 94.16) * mm, "end": v(138.17, 94.76) * mm});
            skLineSegment(sketch, "E21.2.5.7", {"start": v(138.17, 99.16) * mm, "end": v(138.17, 99.76) * mm});
            skLineSegment(sketch, "E21.2.6.0", {"start": v(142.17, 147.56) * mm, "end": v(138.17, 147.56) * mm});
            skLineSegment(sketch, "E21.2.6.1", {"start": v(142.17, 143.16) * mm, "end": v(138.17, 143.16) * mm});
            skLineSegment(sketch, "E21.2.6.2", {"start": v(142.17, 148.16) * mm, "end": v(138.17, 148.16) * mm});
            skLineSegment(sketch, "E21.2.6.3", {"start": v(142.17, 142.56) * mm, "end": v(138.17, 142.56) * mm});
            skLineSegment(sketch, "E21.2.6.4", {"start": v(142.17, 147.56) * mm, "end": v(142.17, 148.16) * mm});
            skLineSegment(sketch, "E21.2.6.5", {"start": v(142.17, 142.56) * mm, "end": v(142.17, 143.16) * mm});
            skLineSegment(sketch, "E21.2.6.6", {"start": v(138.17, 142.56) * mm, "end": v(138.17, 143.16) * mm});
            skLineSegment(sketch, "E21.2.6.7", {"start": v(138.17, 147.56) * mm, "end": v(138.17, 148.16) * mm});
            skLineSegment(sketch, "E21.3.0.0", {"start": v(114.17, -142.84) * mm, "end": v(110.17, -142.84) * mm});
            skLineSegment(sketch, "E21.3.0.1", {"start": v(114.17, -147.24) * mm, "end": v(110.17, -147.24) * mm});
            skLineSegment(sketch, "E21.3.0.2", {"start": v(114.17, -142.24) * mm, "end": v(110.17, -142.24) * mm});
            skLineSegment(sketch, "E21.3.0.3", {"start": v(114.17, -147.84) * mm, "end": v(110.17, -147.84) * mm});
            skLineSegment(sketch, "E21.3.0.4", {"start": v(114.17, -142.84) * mm, "end": v(114.17, -142.24) * mm});
            skLineSegment(sketch, "E21.3.0.5", {"start": v(114.17, -147.84) * mm, "end": v(114.17, -147.24) * mm});
            skLineSegment(sketch, "E21.3.0.6", {"start": v(110.17, -147.84) * mm, "end": v(110.17, -147.24) * mm});
            skLineSegment(sketch, "E21.3.0.7", {"start": v(110.17, -142.84) * mm, "end": v(110.17, -142.24) * mm});
            skLineSegment(sketch, "E21.3.1.0", {"start": v(114.17, -94.44) * mm, "end": v(110.17, -94.44) * mm});
            skLineSegment(sketch, "E21.3.1.1", {"start": v(114.17, -98.84) * mm, "end": v(110.17, -98.84) * mm});
            skLineSegment(sketch, "E21.3.1.2", {"start": v(114.17, -93.84) * mm, "end": v(110.17, -93.84) * mm});
            skLineSegment(sketch, "E21.3.1.3", {"start": v(114.17, -99.44) * mm, "end": v(110.17, -99.44) * mm});
            skLineSegment(sketch, "E21.3.1.4", {"start": v(114.17, -94.44) * mm, "end": v(114.17, -93.84) * mm});
            skLineSegment(sketch, "E21.3.1.5", {"start": v(114.17, -99.44) * mm, "end": v(114.17, -98.84) * mm});
            skLineSegment(sketch, "E21.3.1.6", {"start": v(110.17, -99.44) * mm, "end": v(110.17, -98.84) * mm});
            skLineSegment(sketch, "E21.3.1.7", {"start": v(110.17, -94.44) * mm, "end": v(110.17, -93.84) * mm});
            skLineSegment(sketch, "E21.3.2.0", {"start": v(114.17, -46.04) * mm, "end": v(110.17, -46.04) * mm});
            skLineSegment(sketch, "E21.3.2.1", {"start": v(114.17, -50.44) * mm, "end": v(110.17, -50.44) * mm});
            skLineSegment(sketch, "E21.3.2.2", {"start": v(114.17, -45.44) * mm, "end": v(110.17, -45.44) * mm});
            skLineSegment(sketch, "E21.3.2.3", {"start": v(114.17, -51.04) * mm, "end": v(110.17, -51.04) * mm});
            skLineSegment(sketch, "E21.3.2.4", {"start": v(114.17, -46.04) * mm, "end": v(114.17, -45.44) * mm});
            skLineSegment(sketch, "E21.3.2.5", {"start": v(114.17, -51.04) * mm, "end": v(114.17, -50.44) * mm});
            skLineSegment(sketch, "E21.3.2.6", {"start": v(110.17, -51.04) * mm, "end": v(110.17, -50.44) * mm});
            skLineSegment(sketch, "E21.3.2.7", {"start": v(110.17, -46.04) * mm, "end": v(110.17, -45.44) * mm});
            skLineSegment(sketch, "E21.3.3.0", {"start": v(114.17, 2.36) * mm, "end": v(110.17, 2.36) * mm});
            skLineSegment(sketch, "E21.3.3.1", {"start": v(114.17, -2.04) * mm, "end": v(110.17, -2.04) * mm});
            skLineSegment(sketch, "E21.3.3.2", {"start": v(114.17, 2.96) * mm, "end": v(110.17, 2.96) * mm});
            skLineSegment(sketch, "E21.3.3.3", {"start": v(114.17, -2.64) * mm, "end": v(110.17, -2.64) * mm});
            skLineSegment(sketch, "E21.3.3.4", {"start": v(114.17, 2.36) * mm, "end": v(114.17, 2.96) * mm});
            skLineSegment(sketch, "E21.3.3.5", {"start": v(114.17, -2.64) * mm, "end": v(114.17, -2.04) * mm});
            skLineSegment(sketch, "E21.3.3.6", {"start": v(110.17, -2.64) * mm, "end": v(110.17, -2.04) * mm});
            skLineSegment(sketch, "E21.3.3.7", {"start": v(110.17, 2.36) * mm, "end": v(110.17, 2.96) * mm});
            skLineSegment(sketch, "E21.3.4.0", {"start": v(114.17, 50.76) * mm, "end": v(110.17, 50.76) * mm});
            skLineSegment(sketch, "E21.3.4.1", {"start": v(114.17, 46.36) * mm, "end": v(110.17, 46.36) * mm});
            skLineSegment(sketch, "E21.3.4.2", {"start": v(114.17, 51.36) * mm, "end": v(110.17, 51.36) * mm});
            skLineSegment(sketch, "E21.3.4.3", {"start": v(114.17, 45.76) * mm, "end": v(110.17, 45.76) * mm});
            skLineSegment(sketch, "E21.3.4.4", {"start": v(114.17, 50.76) * mm, "end": v(114.17, 51.36) * mm});
            skLineSegment(sketch, "E21.3.4.5", {"start": v(114.17, 45.76) * mm, "end": v(114.17, 46.36) * mm});
            skLineSegment(sketch, "E21.3.4.6", {"start": v(110.17, 45.76) * mm, "end": v(110.17, 46.36) * mm});
            skLineSegment(sketch, "E21.3.4.7", {"start": v(110.17, 50.76) * mm, "end": v(110.17, 51.36) * mm});
            skLineSegment(sketch, "E21.3.5.0", {"start": v(114.17, 99.16) * mm, "end": v(110.17, 99.16) * mm});
            skLineSegment(sketch, "E21.3.5.1", {"start": v(114.17, 94.76) * mm, "end": v(110.17, 94.76) * mm});
            skLineSegment(sketch, "E21.3.5.2", {"start": v(114.17, 99.76) * mm, "end": v(110.17, 99.76) * mm});
            skLineSegment(sketch, "E21.3.5.3", {"start": v(114.17, 94.16) * mm, "end": v(110.17, 94.16) * mm});
            skLineSegment(sketch, "E21.3.5.4", {"start": v(114.17, 99.16) * mm, "end": v(114.17, 99.76) * mm});
            skLineSegment(sketch, "E21.3.5.5", {"start": v(114.17, 94.16) * mm, "end": v(114.17, 94.76) * mm});
            skLineSegment(sketch, "E21.3.5.6", {"start": v(110.17, 94.16) * mm, "end": v(110.17, 94.76) * mm});
            skLineSegment(sketch, "E21.3.5.7", {"start": v(110.17, 99.16) * mm, "end": v(110.17, 99.76) * mm});
            skLineSegment(sketch, "E21.3.6.0", {"start": v(114.17, 147.56) * mm, "end": v(110.17, 147.56) * mm});
            skLineSegment(sketch, "E21.3.6.1", {"start": v(114.17, 143.16) * mm, "end": v(110.17, 143.16) * mm});
            skLineSegment(sketch, "E21.3.6.2", {"start": v(114.17, 148.16) * mm, "end": v(110.17, 148.16) * mm});
            skLineSegment(sketch, "E21.3.6.3", {"start": v(114.17, 142.56) * mm, "end": v(110.17, 142.56) * mm});
            skLineSegment(sketch, "E21.3.6.4", {"start": v(114.17, 147.56) * mm, "end": v(114.17, 148.16) * mm});
            skLineSegment(sketch, "E21.3.6.5", {"start": v(114.17, 142.56) * mm, "end": v(114.17, 143.16) * mm});
            skLineSegment(sketch, "E21.3.6.6", {"start": v(110.17, 142.56) * mm, "end": v(110.17, 143.16) * mm});
            skLineSegment(sketch, "E21.3.6.7", {"start": v(110.17, 147.56) * mm, "end": v(110.17, 148.16) * mm});
            skLineSegment(sketch, "E21.4.0.0", {"start": v(86.17, -142.84) * mm, "end": v(82.17, -142.84) * mm});
            skLineSegment(sketch, "E21.4.0.1", {"start": v(86.17, -147.24) * mm, "end": v(82.17, -147.24) * mm});
            skLineSegment(sketch, "E21.4.0.2", {"start": v(86.17, -142.24) * mm, "end": v(82.17, -142.24) * mm});
            skLineSegment(sketch, "E21.4.0.3", {"start": v(86.17, -147.84) * mm, "end": v(82.17, -147.84) * mm});
            skLineSegment(sketch, "E21.4.0.4", {"start": v(86.17, -142.84) * mm, "end": v(86.17, -142.24) * mm});
            skLineSegment(sketch, "E21.4.0.5", {"start": v(86.17, -147.84) * mm, "end": v(86.17, -147.24) * mm});
            skLineSegment(sketch, "E21.4.0.6", {"start": v(82.17, -147.84) * mm, "end": v(82.17, -147.24) * mm});
            skLineSegment(sketch, "E21.4.0.7", {"start": v(82.17, -142.84) * mm, "end": v(82.17, -142.24) * mm});
            skLineSegment(sketch, "E21.4.1.0", {"start": v(86.17, -94.44) * mm, "end": v(82.17, -94.44) * mm});
            skLineSegment(sketch, "E21.4.1.1", {"start": v(86.17, -98.84) * mm, "end": v(82.17, -98.84) * mm});
            skLineSegment(sketch, "E21.4.1.2", {"start": v(86.17, -93.84) * mm, "end": v(82.17, -93.84) * mm});
            skLineSegment(sketch, "E21.4.1.3", {"start": v(86.17, -99.44) * mm, "end": v(82.17, -99.44) * mm});
            skLineSegment(sketch, "E21.4.1.4", {"start": v(86.17, -94.44) * mm, "end": v(86.17, -93.84) * mm});
            skLineSegment(sketch, "E21.4.1.5", {"start": v(86.17, -99.44) * mm, "end": v(86.17, -98.84) * mm});
            skLineSegment(sketch, "E21.4.1.6", {"start": v(82.17, -99.44) * mm, "end": v(82.17, -98.84) * mm});
            skLineSegment(sketch, "E21.4.1.7", {"start": v(82.17, -94.44) * mm, "end": v(82.17, -93.84) * mm});
            skLineSegment(sketch, "E21.4.2.0", {"start": v(86.17, -46.04) * mm, "end": v(82.17, -46.04) * mm});
            skLineSegment(sketch, "E21.4.2.1", {"start": v(86.17, -50.44) * mm, "end": v(82.17, -50.44) * mm});
            skLineSegment(sketch, "E21.4.2.2", {"start": v(86.17, -45.44) * mm, "end": v(82.17, -45.44) * mm});
            skLineSegment(sketch, "E21.4.2.3", {"start": v(86.17, -51.04) * mm, "end": v(82.17, -51.04) * mm});
            skLineSegment(sketch, "E21.4.2.4", {"start": v(86.17, -46.04) * mm, "end": v(86.17, -45.44) * mm});
            skLineSegment(sketch, "E21.4.2.5", {"start": v(86.17, -51.04) * mm, "end": v(86.17, -50.44) * mm});
            skLineSegment(sketch, "E21.4.2.6", {"start": v(82.17, -51.04) * mm, "end": v(82.17, -50.44) * mm});
            skLineSegment(sketch, "E21.4.2.7", {"start": v(82.17, -46.04) * mm, "end": v(82.17, -45.44) * mm});
            skLineSegment(sketch, "E21.4.3.0", {"start": v(86.17, 2.36) * mm, "end": v(82.17, 2.36) * mm});
            skLineSegment(sketch, "E21.4.3.1", {"start": v(86.17, -2.04) * mm, "end": v(82.17, -2.04) * mm});
            skLineSegment(sketch, "E21.4.3.2", {"start": v(86.17, 2.96) * mm, "end": v(82.17, 2.96) * mm});
            skLineSegment(sketch, "E21.4.3.3", {"start": v(86.17, -2.64) * mm, "end": v(82.17, -2.64) * mm});
            skLineSegment(sketch, "E21.4.3.4", {"start": v(86.17, 2.36) * mm, "end": v(86.17, 2.96) * mm});
            skLineSegment(sketch, "E21.4.3.5", {"start": v(86.17, -2.64) * mm, "end": v(86.17, -2.04) * mm});
            skLineSegment(sketch, "E21.4.3.6", {"start": v(82.17, -2.64) * mm, "end": v(82.17, -2.04) * mm});
            skLineSegment(sketch, "E21.4.3.7", {"start": v(82.17, 2.36) * mm, "end": v(82.17, 2.96) * mm});
            skLineSegment(sketch, "E21.4.4.0", {"start": v(86.17, 50.76) * mm, "end": v(82.17, 50.76) * mm});
            skLineSegment(sketch, "E21.4.4.1", {"start": v(86.17, 46.36) * mm, "end": v(82.17, 46.36) * mm});
            skLineSegment(sketch, "E21.4.4.2", {"start": v(86.17, 51.36) * mm, "end": v(82.17, 51.36) * mm});
            skLineSegment(sketch, "E21.4.4.3", {"start": v(86.17, 45.76) * mm, "end": v(82.17, 45.76) * mm});
            skLineSegment(sketch, "E21.4.4.4", {"start": v(86.17, 50.76) * mm, "end": v(86.17, 51.36) * mm});
            skLineSegment(sketch, "E21.4.4.5", {"start": v(86.17, 45.76) * mm, "end": v(86.17, 46.36) * mm});
            skLineSegment(sketch, "E21.4.4.6", {"start": v(82.17, 45.76) * mm, "end": v(82.17, 46.36) * mm});
            skLineSegment(sketch, "E21.4.4.7", {"start": v(82.17, 50.76) * mm, "end": v(82.17, 51.36) * mm});
            skLineSegment(sketch, "E21.4.5.0", {"start": v(86.17, 99.16) * mm, "end": v(82.17, 99.16) * mm});
            skLineSegment(sketch, "E21.4.5.1", {"start": v(86.17, 94.76) * mm, "end": v(82.17, 94.76) * mm});
            skLineSegment(sketch, "E21.4.5.2", {"start": v(86.17, 99.76) * mm, "end": v(82.17, 99.76) * mm});
            skLineSegment(sketch, "E21.4.5.3", {"start": v(86.17, 94.16) * mm, "end": v(82.17, 94.16) * mm});
            skLineSegment(sketch, "E21.4.5.4", {"start": v(86.17, 99.16) * mm, "end": v(86.17, 99.76) * mm});
            skLineSegment(sketch, "E21.4.5.5", {"start": v(86.17, 94.16) * mm, "end": v(86.17, 94.76) * mm});
            skLineSegment(sketch, "E21.4.5.6", {"start": v(82.17, 94.16) * mm, "end": v(82.17, 94.76) * mm});
            skLineSegment(sketch, "E21.4.5.7", {"start": v(82.17, 99.16) * mm, "end": v(82.17, 99.76) * mm});
            skLineSegment(sketch, "E21.4.6.0", {"start": v(86.17, 147.56) * mm, "end": v(82.17, 147.56) * mm});
            skLineSegment(sketch, "E21.4.6.1", {"start": v(86.17, 143.16) * mm, "end": v(82.17, 143.16) * mm});
            skLineSegment(sketch, "E21.4.6.2", {"start": v(86.17, 148.16) * mm, "end": v(82.17, 148.16) * mm});
            skLineSegment(sketch, "E21.4.6.3", {"start": v(86.17, 142.56) * mm, "end": v(82.17, 142.56) * mm});
            skLineSegment(sketch, "E21.4.6.4", {"start": v(86.17, 147.56) * mm, "end": v(86.17, 148.16) * mm});
            skLineSegment(sketch, "E21.4.6.5", {"start": v(86.17, 142.56) * mm, "end": v(86.17, 143.16) * mm});
            skLineSegment(sketch, "E21.4.6.6", {"start": v(82.17, 142.56) * mm, "end": v(82.17, 143.16) * mm});
            skLineSegment(sketch, "E21.4.6.7", {"start": v(82.17, 147.56) * mm, "end": v(82.17, 148.16) * mm});
            skLineSegment(sketch, "E21.5.0.0", {"start": v(58.17, -142.84) * mm, "end": v(54.17, -142.84) * mm});
            skLineSegment(sketch, "E21.5.0.1", {"start": v(58.17, -147.24) * mm, "end": v(54.17, -147.24) * mm});
            skLineSegment(sketch, "E21.5.0.2", {"start": v(58.17, -142.24) * mm, "end": v(54.17, -142.24) * mm});
            skLineSegment(sketch, "E21.5.0.3", {"start": v(58.17, -147.84) * mm, "end": v(54.17, -147.84) * mm});
            skLineSegment(sketch, "E21.5.0.4", {"start": v(58.17, -142.84) * mm, "end": v(58.17, -142.24) * mm});
            skLineSegment(sketch, "E21.5.0.5", {"start": v(58.17, -147.84) * mm, "end": v(58.17, -147.24) * mm});
            skLineSegment(sketch, "E21.5.0.6", {"start": v(54.17, -147.84) * mm, "end": v(54.17, -147.24) * mm});
            skLineSegment(sketch, "E21.5.0.7", {"start": v(54.17, -142.84) * mm, "end": v(54.17, -142.24) * mm});
            skLineSegment(sketch, "E21.5.1.0", {"start": v(58.17, -94.44) * mm, "end": v(54.17, -94.44) * mm});
            skLineSegment(sketch, "E21.5.1.1", {"start": v(58.17, -98.84) * mm, "end": v(54.17, -98.84) * mm});
            skLineSegment(sketch, "E21.5.1.2", {"start": v(58.17, -93.84) * mm, "end": v(54.17, -93.84) * mm});
            skLineSegment(sketch, "E21.5.1.3", {"start": v(58.17, -99.44) * mm, "end": v(54.17, -99.44) * mm});
            skLineSegment(sketch, "E21.5.1.4", {"start": v(58.17, -94.44) * mm, "end": v(58.17, -93.84) * mm});
            skLineSegment(sketch, "E21.5.1.5", {"start": v(58.17, -99.44) * mm, "end": v(58.17, -98.84) * mm});
            skLineSegment(sketch, "E21.5.1.6", {"start": v(54.17, -99.44) * mm, "end": v(54.17, -98.84) * mm});
            skLineSegment(sketch, "E21.5.1.7", {"start": v(54.17, -94.44) * mm, "end": v(54.17, -93.84) * mm});
            skLineSegment(sketch, "E21.5.2.0", {"start": v(58.17, -46.04) * mm, "end": v(54.17, -46.04) * mm});
            skLineSegment(sketch, "E21.5.2.1", {"start": v(58.17, -50.44) * mm, "end": v(54.17, -50.44) * mm});
            skLineSegment(sketch, "E21.5.2.2", {"start": v(58.17, -45.44) * mm, "end": v(54.17, -45.44) * mm});
            skLineSegment(sketch, "E21.5.2.3", {"start": v(58.17, -51.04) * mm, "end": v(54.17, -51.04) * mm});
            skLineSegment(sketch, "E21.5.2.4", {"start": v(58.17, -46.04) * mm, "end": v(58.17, -45.44) * mm});
            skLineSegment(sketch, "E21.5.2.5", {"start": v(58.17, -51.04) * mm, "end": v(58.17, -50.44) * mm});
            skLineSegment(sketch, "E21.5.2.6", {"start": v(54.17, -51.04) * mm, "end": v(54.17, -50.44) * mm});
            skLineSegment(sketch, "E21.5.2.7", {"start": v(54.17, -46.04) * mm, "end": v(54.17, -45.44) * mm});
            skLineSegment(sketch, "E21.5.3.0", {"start": v(58.17, 2.36) * mm, "end": v(54.17, 2.36) * mm});
            skLineSegment(sketch, "E21.5.3.1", {"start": v(58.17, -2.04) * mm, "end": v(54.17, -2.04) * mm});
            skLineSegment(sketch, "E21.5.3.2", {"start": v(58.17, 2.96) * mm, "end": v(54.17, 2.96) * mm});
            skLineSegment(sketch, "E21.5.3.3", {"start": v(58.17, -2.64) * mm, "end": v(54.17, -2.64) * mm});
            skLineSegment(sketch, "E21.5.3.4", {"start": v(58.17, 2.36) * mm, "end": v(58.17, 2.96) * mm});
            skLineSegment(sketch, "E21.5.3.5", {"start": v(58.17, -2.64) * mm, "end": v(58.17, -2.04) * mm});
            skLineSegment(sketch, "E21.5.3.6", {"start": v(54.17, -2.64) * mm, "end": v(54.17, -2.04) * mm});
            skLineSegment(sketch, "E21.5.3.7", {"start": v(54.17, 2.36) * mm, "end": v(54.17, 2.96) * mm});
            skLineSegment(sketch, "E21.5.4.0", {"start": v(58.17, 50.76) * mm, "end": v(54.17, 50.76) * mm});
            skLineSegment(sketch, "E21.5.4.1", {"start": v(58.17, 46.36) * mm, "end": v(54.17, 46.36) * mm});
            skLineSegment(sketch, "E21.5.4.2", {"start": v(58.17, 51.36) * mm, "end": v(54.17, 51.36) * mm});
            skLineSegment(sketch, "E21.5.4.3", {"start": v(58.17, 45.76) * mm, "end": v(54.17, 45.76) * mm});
            skLineSegment(sketch, "E21.5.4.4", {"start": v(58.17, 50.76) * mm, "end": v(58.17, 51.36) * mm});
            skLineSegment(sketch, "E21.5.4.5", {"start": v(58.17, 45.76) * mm, "end": v(58.17, 46.36) * mm});
            skLineSegment(sketch, "E21.5.4.6", {"start": v(54.17, 45.76) * mm, "end": v(54.17, 46.36) * mm});
            skLineSegment(sketch, "E21.5.4.7", {"start": v(54.17, 50.76) * mm, "end": v(54.17, 51.36) * mm});
            skLineSegment(sketch, "E21.5.5.0", {"start": v(58.17, 99.16) * mm, "end": v(54.17, 99.16) * mm});
            skLineSegment(sketch, "E21.5.5.1", {"start": v(58.17, 94.76) * mm, "end": v(54.17, 94.76) * mm});
            skLineSegment(sketch, "E21.5.5.2", {"start": v(58.17, 99.76) * mm, "end": v(54.17, 99.76) * mm});
            skLineSegment(sketch, "E21.5.5.3", {"start": v(58.17, 94.16) * mm, "end": v(54.17, 94.16) * mm});
            skLineSegment(sketch, "E21.5.5.4", {"start": v(58.17, 99.16) * mm, "end": v(58.17, 99.76) * mm});
            skLineSegment(sketch, "E21.5.5.5", {"start": v(58.17, 94.16) * mm, "end": v(58.17, 94.76) * mm});
            skLineSegment(sketch, "E21.5.5.6", {"start": v(54.17, 94.16) * mm, "end": v(54.17, 94.76) * mm});
            skLineSegment(sketch, "E21.5.5.7", {"start": v(54.17, 99.16) * mm, "end": v(54.17, 99.76) * mm});
            skLineSegment(sketch, "E21.5.6.0", {"start": v(58.17, 147.56) * mm, "end": v(54.17, 147.56) * mm});
            skLineSegment(sketch, "E21.5.6.1", {"start": v(58.17, 143.16) * mm, "end": v(54.17, 143.16) * mm});
            skLineSegment(sketch, "E21.5.6.2", {"start": v(58.17, 148.16) * mm, "end": v(54.17, 148.16) * mm});
            skLineSegment(sketch, "E21.5.6.3", {"start": v(58.17, 142.56) * mm, "end": v(54.17, 142.56) * mm});
            skLineSegment(sketch, "E21.5.6.4", {"start": v(58.17, 147.56) * mm, "end": v(58.17, 148.16) * mm});
            skLineSegment(sketch, "E21.5.6.5", {"start": v(58.17, 142.56) * mm, "end": v(58.17, 143.16) * mm});
            skLineSegment(sketch, "E21.5.6.6", {"start": v(54.17, 142.56) * mm, "end": v(54.17, 143.16) * mm});
            skLineSegment(sketch, "E21.5.6.7", {"start": v(54.17, 147.56) * mm, "end": v(54.17, 148.16) * mm});
            skLineSegment(sketch, "E21.6.0.0", {"start": v(30.17, -142.84) * mm, "end": v(26.17, -142.84) * mm});
            skLineSegment(sketch, "E21.6.0.1", {"start": v(30.17, -147.24) * mm, "end": v(26.17, -147.24) * mm});
            skLineSegment(sketch, "E21.6.0.2", {"start": v(30.17, -142.24) * mm, "end": v(26.17, -142.24) * mm});
            skLineSegment(sketch, "E21.6.0.3", {"start": v(30.17, -147.84) * mm, "end": v(26.17, -147.84) * mm});
            skLineSegment(sketch, "E21.6.0.4", {"start": v(30.17, -142.84) * mm, "end": v(30.17, -142.24) * mm});
            skLineSegment(sketch, "E21.6.0.5", {"start": v(30.17, -147.84) * mm, "end": v(30.17, -147.24) * mm});
            skLineSegment(sketch, "E21.6.0.6", {"start": v(26.17, -147.84) * mm, "end": v(26.17, -147.24) * mm});
            skLineSegment(sketch, "E21.6.0.7", {"start": v(26.17, -142.84) * mm, "end": v(26.17, -142.24) * mm});
            skLineSegment(sketch, "E21.6.1.0", {"start": v(30.17, -94.44) * mm, "end": v(26.17, -94.44) * mm});
            skLineSegment(sketch, "E21.6.1.1", {"start": v(30.17, -98.84) * mm, "end": v(26.17, -98.84) * mm});
            skLineSegment(sketch, "E21.6.1.2", {"start": v(30.17, -93.84) * mm, "end": v(26.17, -93.84) * mm});
            skLineSegment(sketch, "E21.6.1.3", {"start": v(30.17, -99.44) * mm, "end": v(26.17, -99.44) * mm});
            skLineSegment(sketch, "E21.6.1.4", {"start": v(30.17, -94.44) * mm, "end": v(30.17, -93.84) * mm});
            skLineSegment(sketch, "E21.6.1.5", {"start": v(30.17, -99.44) * mm, "end": v(30.17, -98.84) * mm});
            skLineSegment(sketch, "E21.6.1.6", {"start": v(26.17, -99.44) * mm, "end": v(26.17, -98.84) * mm});
            skLineSegment(sketch, "E21.6.1.7", {"start": v(26.17, -94.44) * mm, "end": v(26.17, -93.84) * mm});
            skLineSegment(sketch, "E21.6.2.0", {"start": v(30.17, -46.04) * mm, "end": v(26.17, -46.04) * mm});
            skLineSegment(sketch, "E21.6.2.1", {"start": v(30.17, -50.44) * mm, "end": v(26.17, -50.44) * mm});
            skLineSegment(sketch, "E21.6.2.2", {"start": v(30.17, -45.44) * mm, "end": v(26.17, -45.44) * mm});
            skLineSegment(sketch, "E21.6.2.3", {"start": v(30.17, -51.04) * mm, "end": v(26.17, -51.04) * mm});
            skLineSegment(sketch, "E21.6.2.4", {"start": v(30.17, -46.04) * mm, "end": v(30.17, -45.44) * mm});
            skLineSegment(sketch, "E21.6.2.5", {"start": v(30.17, -51.04) * mm, "end": v(30.17, -50.44) * mm});
            skLineSegment(sketch, "E21.6.2.6", {"start": v(26.17, -51.04) * mm, "end": v(26.17, -50.44) * mm});
            skLineSegment(sketch, "E21.6.2.7", {"start": v(26.17, -46.04) * mm, "end": v(26.17, -45.44) * mm});
            skLineSegment(sketch, "E21.6.3.0", {"start": v(30.17, 2.36) * mm, "end": v(26.17, 2.36) * mm});
            skLineSegment(sketch, "E21.6.3.1", {"start": v(30.17, -2.04) * mm, "end": v(26.17, -2.04) * mm});
            skLineSegment(sketch, "E21.6.3.2", {"start": v(30.17, 2.96) * mm, "end": v(26.17, 2.96) * mm});
            skLineSegment(sketch, "E21.6.3.3", {"start": v(30.17, -2.64) * mm, "end": v(26.17, -2.64) * mm});
            skLineSegment(sketch, "E21.6.3.4", {"start": v(30.17, 2.36) * mm, "end": v(30.17, 2.96) * mm});
            skLineSegment(sketch, "E21.6.3.5", {"start": v(30.17, -2.64) * mm, "end": v(30.17, -2.04) * mm});
            skLineSegment(sketch, "E21.6.3.6", {"start": v(26.17, -2.64) * mm, "end": v(26.17, -2.04) * mm});
            skLineSegment(sketch, "E21.6.3.7", {"start": v(26.17, 2.36) * mm, "end": v(26.17, 2.96) * mm});
            skLineSegment(sketch, "E21.6.4.0", {"start": v(30.17, 50.76) * mm, "end": v(26.17, 50.76) * mm});
            skLineSegment(sketch, "E21.6.4.1", {"start": v(30.17, 46.36) * mm, "end": v(26.17, 46.36) * mm});
            skLineSegment(sketch, "E21.6.4.2", {"start": v(30.17, 51.36) * mm, "end": v(26.17, 51.36) * mm});
            skLineSegment(sketch, "E21.6.4.3", {"start": v(30.17, 45.76) * mm, "end": v(26.17, 45.76) * mm});
            skLineSegment(sketch, "E21.6.4.4", {"start": v(30.17, 50.76) * mm, "end": v(30.17, 51.36) * mm});
            skLineSegment(sketch, "E21.6.4.5", {"start": v(30.17, 45.76) * mm, "end": v(30.17, 46.36) * mm});
            skLineSegment(sketch, "E21.6.4.6", {"start": v(26.17, 45.76) * mm, "end": v(26.17, 46.36) * mm});
            skLineSegment(sketch, "E21.6.4.7", {"start": v(26.17, 50.76) * mm, "end": v(26.17, 51.36) * mm});
            skLineSegment(sketch, "E21.6.5.0", {"start": v(30.17, 99.16) * mm, "end": v(26.17, 99.16) * mm});
            skLineSegment(sketch, "E21.6.5.1", {"start": v(30.17, 94.76) * mm, "end": v(26.17, 94.76) * mm});
            skLineSegment(sketch, "E21.6.5.2", {"start": v(30.17, 99.76) * mm, "end": v(26.17, 99.76) * mm});
            skLineSegment(sketch, "E21.6.5.3", {"start": v(30.17, 94.16) * mm, "end": v(26.17, 94.16) * mm});
            skLineSegment(sketch, "E21.6.5.4", {"start": v(30.17, 99.16) * mm, "end": v(30.17, 99.76) * mm});
            skLineSegment(sketch, "E21.6.5.5", {"start": v(30.17, 94.16) * mm, "end": v(30.17, 94.76) * mm});
            skLineSegment(sketch, "E21.6.5.6", {"start": v(26.17, 94.16) * mm, "end": v(26.17, 94.76) * mm});
            skLineSegment(sketch, "E21.6.5.7", {"start": v(26.17, 99.16) * mm, "end": v(26.17, 99.76) * mm});
            skLineSegment(sketch, "E21.6.6.0", {"start": v(30.17, 147.56) * mm, "end": v(26.17, 147.56) * mm});
            skLineSegment(sketch, "E21.6.6.1", {"start": v(30.17, 143.16) * mm, "end": v(26.17, 143.16) * mm});
            skLineSegment(sketch, "E21.6.6.2", {"start": v(30.17, 148.16) * mm, "end": v(26.17, 148.16) * mm});
            skLineSegment(sketch, "E21.6.6.3", {"start": v(30.17, 142.56) * mm, "end": v(26.17, 142.56) * mm});
            skLineSegment(sketch, "E21.6.6.4", {"start": v(30.17, 147.56) * mm, "end": v(30.17, 148.16) * mm});
            skLineSegment(sketch, "E21.6.6.5", {"start": v(30.17, 142.56) * mm, "end": v(30.17, 143.16) * mm});
            skLineSegment(sketch, "E21.6.6.6", {"start": v(26.17, 142.56) * mm, "end": v(26.17, 143.16) * mm});
            skLineSegment(sketch, "E21.6.6.7", {"start": v(26.17, 147.56) * mm, "end": v(26.17, 148.16) * mm});
            skLineSegment(sketch, "E21.7.0.0", {"start": v(2.17, -142.84) * mm, "end": v(-1.83, -142.84) * mm});
            skLineSegment(sketch, "E21.7.0.1", {"start": v(2.17, -147.24) * mm, "end": v(-1.83, -147.24) * mm});
            skLineSegment(sketch, "E21.7.0.2", {"start": v(2.17, -142.24) * mm, "end": v(-1.83, -142.24) * mm});
            skLineSegment(sketch, "E21.7.0.3", {"start": v(2.17, -147.84) * mm, "end": v(-1.83, -147.84) * mm});
            skLineSegment(sketch, "E21.7.0.4", {"start": v(2.17, -142.84) * mm, "end": v(2.17, -142.24) * mm});
            skLineSegment(sketch, "E21.7.0.5", {"start": v(2.17, -147.84) * mm, "end": v(2.17, -147.24) * mm});
            skLineSegment(sketch, "E21.7.0.6", {"start": v(-1.83, -147.84) * mm, "end": v(-1.83, -147.24) * mm});
            skLineSegment(sketch, "E21.7.0.7", {"start": v(-1.83, -142.84) * mm, "end": v(-1.83, -142.24) * mm});
            skLineSegment(sketch, "E21.7.1.0", {"start": v(2.17, -94.44) * mm, "end": v(-1.83, -94.44) * mm});
            skLineSegment(sketch, "E21.7.1.1", {"start": v(2.17, -98.84) * mm, "end": v(-1.83, -98.84) * mm});
            skLineSegment(sketch, "E21.7.1.2", {"start": v(2.17, -93.84) * mm, "end": v(-1.83, -93.84) * mm});
            skLineSegment(sketch, "E21.7.1.3", {"start": v(2.17, -99.44) * mm, "end": v(-1.83, -99.44) * mm});
            skLineSegment(sketch, "E21.7.1.4", {"start": v(2.17, -94.44) * mm, "end": v(2.17, -93.84) * mm});
            skLineSegment(sketch, "E21.7.1.5", {"start": v(2.17, -99.44) * mm, "end": v(2.17, -98.84) * mm});
            skLineSegment(sketch, "E21.7.1.6", {"start": v(-1.83, -99.44) * mm, "end": v(-1.83, -98.84) * mm});
            skLineSegment(sketch, "E21.7.1.7", {"start": v(-1.83, -94.44) * mm, "end": v(-1.83, -93.84) * mm});
            skLineSegment(sketch, "E21.7.2.0", {"start": v(2.17, -46.04) * mm, "end": v(-1.83, -46.04) * mm});
            skLineSegment(sketch, "E21.7.2.1", {"start": v(2.17, -50.44) * mm, "end": v(-1.83, -50.44) * mm});
            skLineSegment(sketch, "E21.7.2.2", {"start": v(2.17, -45.44) * mm, "end": v(-1.83, -45.44) * mm});
            skLineSegment(sketch, "E21.7.2.3", {"start": v(2.17, -51.04) * mm, "end": v(-1.83, -51.04) * mm});
            skLineSegment(sketch, "E21.7.2.4", {"start": v(2.17, -46.04) * mm, "end": v(2.17, -45.44) * mm});
            skLineSegment(sketch, "E21.7.2.5", {"start": v(2.17, -51.04) * mm, "end": v(2.17, -50.44) * mm});
            skLineSegment(sketch, "E21.7.2.6", {"start": v(-1.83, -51.04) * mm, "end": v(-1.83, -50.44) * mm});
            skLineSegment(sketch, "E21.7.2.7", {"start": v(-1.83, -46.04) * mm, "end": v(-1.83, -45.44) * mm});
            skLineSegment(sketch, "E21.7.3.0", {"start": v(2.17, 2.36) * mm, "end": v(-1.83, 2.36) * mm});
            skLineSegment(sketch, "E21.7.3.1", {"start": v(2.17, -2.04) * mm, "end": v(-1.83, -2.04) * mm});
            skLineSegment(sketch, "E21.7.3.2", {"start": v(2.17, 2.96) * mm, "end": v(-1.83, 2.96) * mm});
            skLineSegment(sketch, "E21.7.3.3", {"start": v(2.17, -2.64) * mm, "end": v(-1.83, -2.64) * mm});
            skLineSegment(sketch, "E21.7.3.4", {"start": v(2.17, 2.36) * mm, "end": v(2.17, 2.96) * mm});
            skLineSegment(sketch, "E21.7.3.5", {"start": v(2.17, -2.64) * mm, "end": v(2.17, -2.04) * mm});
            skLineSegment(sketch, "E21.7.3.6", {"start": v(-1.83, -2.64) * mm, "end": v(-1.83, -2.04) * mm});
            skLineSegment(sketch, "E21.7.3.7", {"start": v(-1.83, 2.36) * mm, "end": v(-1.83, 2.96) * mm});
            skLineSegment(sketch, "E21.7.4.0", {"start": v(2.17, 50.76) * mm, "end": v(-1.83, 50.76) * mm});
            skLineSegment(sketch, "E21.7.4.1", {"start": v(2.17, 46.36) * mm, "end": v(-1.83, 46.36) * mm});
            skLineSegment(sketch, "E21.7.4.2", {"start": v(2.17, 51.36) * mm, "end": v(-1.83, 51.36) * mm});
            skLineSegment(sketch, "E21.7.4.3", {"start": v(2.17, 45.76) * mm, "end": v(-1.83, 45.76) * mm});
            skLineSegment(sketch, "E21.7.4.4", {"start": v(2.17, 50.76) * mm, "end": v(2.17, 51.36) * mm});
            skLineSegment(sketch, "E21.7.4.5", {"start": v(2.17, 45.76) * mm, "end": v(2.17, 46.36) * mm});
            skLineSegment(sketch, "E21.7.4.6", {"start": v(-1.83, 45.76) * mm, "end": v(-1.83, 46.36) * mm});
            skLineSegment(sketch, "E21.7.4.7", {"start": v(-1.83, 50.76) * mm, "end": v(-1.83, 51.36) * mm});
            skLineSegment(sketch, "E21.7.5.0", {"start": v(2.17, 99.16) * mm, "end": v(-1.83, 99.16) * mm});
            skLineSegment(sketch, "E21.7.5.1", {"start": v(2.17, 94.76) * mm, "end": v(-1.83, 94.76) * mm});
            skLineSegment(sketch, "E21.7.5.2", {"start": v(2.17, 99.76) * mm, "end": v(-1.83, 99.76) * mm});
            skLineSegment(sketch, "E21.7.5.3", {"start": v(2.17, 94.16) * mm, "end": v(-1.83, 94.16) * mm});
            skLineSegment(sketch, "E21.7.5.4", {"start": v(2.17, 99.16) * mm, "end": v(2.17, 99.76) * mm});
            skLineSegment(sketch, "E21.7.5.5", {"start": v(2.17, 94.16) * mm, "end": v(2.17, 94.76) * mm});
            skLineSegment(sketch, "E21.7.5.6", {"start": v(-1.83, 94.16) * mm, "end": v(-1.83, 94.76) * mm});
            skLineSegment(sketch, "E21.7.5.7", {"start": v(-1.83, 99.16) * mm, "end": v(-1.83, 99.76) * mm});
            skLineSegment(sketch, "E21.7.6.0", {"start": v(2.17, 147.56) * mm, "end": v(-1.83, 147.56) * mm});
            skLineSegment(sketch, "E21.7.6.1", {"start": v(2.17, 143.16) * mm, "end": v(-1.83, 143.16) * mm});
            skLineSegment(sketch, "E21.7.6.2", {"start": v(2.17, 148.16) * mm, "end": v(-1.83, 148.16) * mm});
            skLineSegment(sketch, "E21.7.6.3", {"start": v(2.17, 142.56) * mm, "end": v(-1.83, 142.56) * mm});
            skLineSegment(sketch, "E21.7.6.4", {"start": v(2.17, 147.56) * mm, "end": v(2.17, 148.16) * mm});
            skLineSegment(sketch, "E21.7.6.5", {"start": v(2.17, 142.56) * mm, "end": v(2.17, 143.16) * mm});
            skLineSegment(sketch, "E21.7.6.6", {"start": v(-1.83, 142.56) * mm, "end": v(-1.83, 143.16) * mm});
            skLineSegment(sketch, "E21.7.6.7", {"start": v(-1.83, 147.56) * mm, "end": v(-1.83, 148.16) * mm});
            skLineSegment(sketch, "E21.8.0.0", {"start": v(-25.83, -142.84) * mm, "end": v(-29.83, -142.84) * mm});
            skLineSegment(sketch, "E21.8.0.1", {"start": v(-25.83, -147.24) * mm, "end": v(-29.83, -147.24) * mm});
            skLineSegment(sketch, "E21.8.0.2", {"start": v(-25.83, -142.24) * mm, "end": v(-29.83, -142.24) * mm});
            skLineSegment(sketch, "E21.8.0.3", {"start": v(-25.83, -147.84) * mm, "end": v(-29.83, -147.84) * mm});
            skLineSegment(sketch, "E21.8.0.4", {"start": v(-25.83, -142.84) * mm, "end": v(-25.83, -142.24) * mm});
            skLineSegment(sketch, "E21.8.0.5", {"start": v(-25.83, -147.84) * mm, "end": v(-25.83, -147.24) * mm});
            skLineSegment(sketch, "E21.8.0.6", {"start": v(-29.83, -147.84) * mm, "end": v(-29.83, -147.24) * mm});
            skLineSegment(sketch, "E21.8.0.7", {"start": v(-29.83, -142.84) * mm, "end": v(-29.83, -142.24) * mm});
            skLineSegment(sketch, "E21.8.1.0", {"start": v(-25.83, -94.44) * mm, "end": v(-29.83, -94.44) * mm});
            skLineSegment(sketch, "E21.8.1.1", {"start": v(-25.83, -98.84) * mm, "end": v(-29.83, -98.84) * mm});
            skLineSegment(sketch, "E21.8.1.2", {"start": v(-25.83, -93.84) * mm, "end": v(-29.83, -93.84) * mm});
            skLineSegment(sketch, "E21.8.1.3", {"start": v(-25.83, -99.44) * mm, "end": v(-29.83, -99.44) * mm});
            skLineSegment(sketch, "E21.8.1.4", {"start": v(-25.83, -94.44) * mm, "end": v(-25.83, -93.84) * mm});
            skLineSegment(sketch, "E21.8.1.5", {"start": v(-25.83, -99.44) * mm, "end": v(-25.83, -98.84) * mm});
            skLineSegment(sketch, "E21.8.1.6", {"start": v(-29.83, -99.44) * mm, "end": v(-29.83, -98.84) * mm});
            skLineSegment(sketch, "E21.8.1.7", {"start": v(-29.83, -94.44) * mm, "end": v(-29.83, -93.84) * mm});
            skLineSegment(sketch, "E21.8.2.0", {"start": v(-25.83, -46.04) * mm, "end": v(-29.83, -46.04) * mm});
            skLineSegment(sketch, "E21.8.2.1", {"start": v(-25.83, -50.44) * mm, "end": v(-29.83, -50.44) * mm});
            skLineSegment(sketch, "E21.8.2.2", {"start": v(-25.83, -45.44) * mm, "end": v(-29.83, -45.44) * mm});
            skLineSegment(sketch, "E21.8.2.3", {"start": v(-25.83, -51.04) * mm, "end": v(-29.83, -51.04) * mm});
            skLineSegment(sketch, "E21.8.2.4", {"start": v(-25.83, -46.04) * mm, "end": v(-25.83, -45.44) * mm});
            skLineSegment(sketch, "E21.8.2.5", {"start": v(-25.83, -51.04) * mm, "end": v(-25.83, -50.44) * mm});
            skLineSegment(sketch, "E21.8.2.6", {"start": v(-29.83, -51.04) * mm, "end": v(-29.83, -50.44) * mm});
            skLineSegment(sketch, "E21.8.2.7", {"start": v(-29.83, -46.04) * mm, "end": v(-29.83, -45.44) * mm});
            skLineSegment(sketch, "E21.8.3.0", {"start": v(-25.83, 2.36) * mm, "end": v(-29.83, 2.36) * mm});
            skLineSegment(sketch, "E21.8.3.1", {"start": v(-25.83, -2.04) * mm, "end": v(-29.83, -2.04) * mm});
            skLineSegment(sketch, "E21.8.3.2", {"start": v(-25.83, 2.96) * mm, "end": v(-29.83, 2.96) * mm});
            skLineSegment(sketch, "E21.8.3.3", {"start": v(-25.83, -2.64) * mm, "end": v(-29.83, -2.64) * mm});
            skLineSegment(sketch, "E21.8.3.4", {"start": v(-25.83, 2.36) * mm, "end": v(-25.83, 2.96) * mm});
            skLineSegment(sketch, "E21.8.3.5", {"start": v(-25.83, -2.64) * mm, "end": v(-25.83, -2.04) * mm});
            skLineSegment(sketch, "E21.8.3.6", {"start": v(-29.83, -2.64) * mm, "end": v(-29.83, -2.04) * mm});
            skLineSegment(sketch, "E21.8.3.7", {"start": v(-29.83, 2.36) * mm, "end": v(-29.83, 2.96) * mm});
            skLineSegment(sketch, "E21.8.4.0", {"start": v(-25.83, 50.76) * mm, "end": v(-29.83, 50.76) * mm});
            skLineSegment(sketch, "E21.8.4.1", {"start": v(-25.83, 46.36) * mm, "end": v(-29.83, 46.36) * mm});
            skLineSegment(sketch, "E21.8.4.2", {"start": v(-25.83, 51.36) * mm, "end": v(-29.83, 51.36) * mm});
            skLineSegment(sketch, "E21.8.4.3", {"start": v(-25.83, 45.76) * mm, "end": v(-29.83, 45.76) * mm});
            skLineSegment(sketch, "E21.8.4.4", {"start": v(-25.83, 50.76) * mm, "end": v(-25.83, 51.36) * mm});
            skLineSegment(sketch, "E21.8.4.5", {"start": v(-25.83, 45.76) * mm, "end": v(-25.83, 46.36) * mm});
            skLineSegment(sketch, "E21.8.4.6", {"start": v(-29.83, 45.76) * mm, "end": v(-29.83, 46.36) * mm});
            skLineSegment(sketch, "E21.8.4.7", {"start": v(-29.83, 50.76) * mm, "end": v(-29.83, 51.36) * mm});
            skLineSegment(sketch, "E21.8.5.0", {"start": v(-25.83, 99.16) * mm, "end": v(-29.83, 99.16) * mm});
            skLineSegment(sketch, "E21.8.5.1", {"start": v(-25.83, 94.76) * mm, "end": v(-29.83, 94.76) * mm});
            skLineSegment(sketch, "E21.8.5.2", {"start": v(-25.83, 99.76) * mm, "end": v(-29.83, 99.76) * mm});
            skLineSegment(sketch, "E21.8.5.3", {"start": v(-25.83, 94.16) * mm, "end": v(-29.83, 94.16) * mm});
            skLineSegment(sketch, "E21.8.5.4", {"start": v(-25.83, 99.16) * mm, "end": v(-25.83, 99.76) * mm});
            skLineSegment(sketch, "E21.8.5.5", {"start": v(-25.83, 94.16) * mm, "end": v(-25.83, 94.76) * mm});
            skLineSegment(sketch, "E21.8.5.6", {"start": v(-29.83, 94.16) * mm, "end": v(-29.83, 94.76) * mm});
            skLineSegment(sketch, "E21.8.5.7", {"start": v(-29.83, 99.16) * mm, "end": v(-29.83, 99.76) * mm});
            skLineSegment(sketch, "E21.8.6.0", {"start": v(-25.83, 147.56) * mm, "end": v(-29.83, 147.56) * mm});
            skLineSegment(sketch, "E21.8.6.1", {"start": v(-25.83, 143.16) * mm, "end": v(-29.83, 143.16) * mm});
            skLineSegment(sketch, "E21.8.6.2", {"start": v(-25.83, 148.16) * mm, "end": v(-29.83, 148.16) * mm});
            skLineSegment(sketch, "E21.8.6.3", {"start": v(-25.83, 142.56) * mm, "end": v(-29.83, 142.56) * mm});
            skLineSegment(sketch, "E21.8.6.4", {"start": v(-25.83, 147.56) * mm, "end": v(-25.83, 148.16) * mm});
            skLineSegment(sketch, "E21.8.6.5", {"start": v(-25.83, 142.56) * mm, "end": v(-25.83, 143.16) * mm});
            skLineSegment(sketch, "E21.8.6.6", {"start": v(-29.83, 142.56) * mm, "end": v(-29.83, 143.16) * mm});
            skLineSegment(sketch, "E21.8.6.7", {"start": v(-29.83, 147.56) * mm, "end": v(-29.83, 148.16) * mm});
            skLineSegment(sketch, "E21.9.0.0", {"start": v(-53.83, -142.84) * mm, "end": v(-57.83, -142.84) * mm});
            skLineSegment(sketch, "E21.9.0.1", {"start": v(-53.83, -147.24) * mm, "end": v(-57.83, -147.24) * mm});
            skLineSegment(sketch, "E21.9.0.2", {"start": v(-53.83, -142.24) * mm, "end": v(-57.83, -142.24) * mm});
            skLineSegment(sketch, "E21.9.0.3", {"start": v(-53.83, -147.84) * mm, "end": v(-57.83, -147.84) * mm});
            skLineSegment(sketch, "E21.9.0.4", {"start": v(-53.83, -142.84) * mm, "end": v(-53.83, -142.24) * mm});
            skLineSegment(sketch, "E21.9.0.5", {"start": v(-53.83, -147.84) * mm, "end": v(-53.83, -147.24) * mm});
            skLineSegment(sketch, "E21.9.0.6", {"start": v(-57.83, -147.84) * mm, "end": v(-57.83, -147.24) * mm});
            skLineSegment(sketch, "E21.9.0.7", {"start": v(-57.83, -142.84) * mm, "end": v(-57.83, -142.24) * mm});
            skLineSegment(sketch, "E21.9.1.0", {"start": v(-53.83, -94.44) * mm, "end": v(-57.83, -94.44) * mm});
            skLineSegment(sketch, "E21.9.1.1", {"start": v(-53.83, -98.84) * mm, "end": v(-57.83, -98.84) * mm});
            skLineSegment(sketch, "E21.9.1.2", {"start": v(-53.83, -93.84) * mm, "end": v(-57.83, -93.84) * mm});
            skLineSegment(sketch, "E21.9.1.3", {"start": v(-53.83, -99.44) * mm, "end": v(-57.83, -99.44) * mm});
            skLineSegment(sketch, "E21.9.1.4", {"start": v(-53.83, -94.44) * mm, "end": v(-53.83, -93.84) * mm});
            skLineSegment(sketch, "E21.9.1.5", {"start": v(-53.83, -99.44) * mm, "end": v(-53.83, -98.84) * mm});
            skLineSegment(sketch, "E21.9.1.6", {"start": v(-57.83, -99.44) * mm, "end": v(-57.83, -98.84) * mm});
            skLineSegment(sketch, "E21.9.1.7", {"start": v(-57.83, -94.44) * mm, "end": v(-57.83, -93.84) * mm});
            skLineSegment(sketch, "E21.9.2.0", {"start": v(-53.83, -46.04) * mm, "end": v(-57.83, -46.04) * mm});
            skLineSegment(sketch, "E21.9.2.1", {"start": v(-53.83, -50.44) * mm, "end": v(-57.83, -50.44) * mm});
            skLineSegment(sketch, "E21.9.2.2", {"start": v(-53.83, -45.44) * mm, "end": v(-57.83, -45.44) * mm});
            skLineSegment(sketch, "E21.9.2.3", {"start": v(-53.83, -51.04) * mm, "end": v(-57.83, -51.04) * mm});
            skLineSegment(sketch, "E21.9.2.4", {"start": v(-53.83, -46.04) * mm, "end": v(-53.83, -45.44) * mm});
            skLineSegment(sketch, "E21.9.2.5", {"start": v(-53.83, -51.04) * mm, "end": v(-53.83, -50.44) * mm});
            skLineSegment(sketch, "E21.9.2.6", {"start": v(-57.83, -51.04) * mm, "end": v(-57.83, -50.44) * mm});
            skLineSegment(sketch, "E21.9.2.7", {"start": v(-57.83, -46.04) * mm, "end": v(-57.83, -45.44) * mm});
            skLineSegment(sketch, "E21.9.3.0", {"start": v(-53.83, 2.36) * mm, "end": v(-57.83, 2.36) * mm});
            skLineSegment(sketch, "E21.9.3.1", {"start": v(-53.83, -2.04) * mm, "end": v(-57.83, -2.04) * mm});
            skLineSegment(sketch, "E21.9.3.2", {"start": v(-53.83, 2.96) * mm, "end": v(-57.83, 2.96) * mm});
            skLineSegment(sketch, "E21.9.3.3", {"start": v(-53.83, -2.64) * mm, "end": v(-57.83, -2.64) * mm});
            skLineSegment(sketch, "E21.9.3.4", {"start": v(-53.83, 2.36) * mm, "end": v(-53.83, 2.96) * mm});
            skLineSegment(sketch, "E21.9.3.5", {"start": v(-53.83, -2.64) * mm, "end": v(-53.83, -2.04) * mm});
            skLineSegment(sketch, "E21.9.3.6", {"start": v(-57.83, -2.64) * mm, "end": v(-57.83, -2.04) * mm});
            skLineSegment(sketch, "E21.9.3.7", {"start": v(-57.83, 2.36) * mm, "end": v(-57.83, 2.96) * mm});
            skLineSegment(sketch, "E21.9.4.0", {"start": v(-53.83, 50.76) * mm, "end": v(-57.83, 50.76) * mm});
            skLineSegment(sketch, "E21.9.4.1", {"start": v(-53.83, 46.36) * mm, "end": v(-57.83, 46.36) * mm});
            skLineSegment(sketch, "E21.9.4.2", {"start": v(-53.83, 51.36) * mm, "end": v(-57.83, 51.36) * mm});
            skLineSegment(sketch, "E21.9.4.3", {"start": v(-53.83, 45.76) * mm, "end": v(-57.83, 45.76) * mm});
            skLineSegment(sketch, "E21.9.4.4", {"start": v(-53.83, 50.76) * mm, "end": v(-53.83, 51.36) * mm});
            skLineSegment(sketch, "E21.9.4.5", {"start": v(-53.83, 45.76) * mm, "end": v(-53.83, 46.36) * mm});
            skLineSegment(sketch, "E21.9.4.6", {"start": v(-57.83, 45.76) * mm, "end": v(-57.83, 46.36) * mm});
            skLineSegment(sketch, "E21.9.4.7", {"start": v(-57.83, 50.76) * mm, "end": v(-57.83, 51.36) * mm});
            skLineSegment(sketch, "E21.9.5.0", {"start": v(-53.83, 99.16) * mm, "end": v(-57.83, 99.16) * mm});
            skLineSegment(sketch, "E21.9.5.1", {"start": v(-53.83, 94.76) * mm, "end": v(-57.83, 94.76) * mm});
            skLineSegment(sketch, "E21.9.5.2", {"start": v(-53.83, 99.76) * mm, "end": v(-57.83, 99.76) * mm});
            skLineSegment(sketch, "E21.9.5.3", {"start": v(-53.83, 94.16) * mm, "end": v(-57.83, 94.16) * mm});
            skLineSegment(sketch, "E21.9.5.4", {"start": v(-53.83, 99.16) * mm, "end": v(-53.83, 99.76) * mm});
            skLineSegment(sketch, "E21.9.5.5", {"start": v(-53.83, 94.16) * mm, "end": v(-53.83, 94.76) * mm});
            skLineSegment(sketch, "E21.9.5.6", {"start": v(-57.83, 94.16) * mm, "end": v(-57.83, 94.76) * mm});
            skLineSegment(sketch, "E21.9.5.7", {"start": v(-57.83, 99.16) * mm, "end": v(-57.83, 99.76) * mm});
            skLineSegment(sketch, "E21.9.6.0", {"start": v(-53.83, 147.56) * mm, "end": v(-57.83, 147.56) * mm});
            skLineSegment(sketch, "E21.9.6.1", {"start": v(-53.83, 143.16) * mm, "end": v(-57.83, 143.16) * mm});
            skLineSegment(sketch, "E21.9.6.2", {"start": v(-53.83, 148.16) * mm, "end": v(-57.83, 148.16) * mm});
            skLineSegment(sketch, "E21.9.6.3", {"start": v(-53.83, 142.56) * mm, "end": v(-57.83, 142.56) * mm});
            skLineSegment(sketch, "E21.9.6.4", {"start": v(-53.83, 147.56) * mm, "end": v(-53.83, 148.16) * mm});
            skLineSegment(sketch, "E21.9.6.5", {"start": v(-53.83, 142.56) * mm, "end": v(-53.83, 143.16) * mm});
            skLineSegment(sketch, "E21.9.6.6", {"start": v(-57.83, 142.56) * mm, "end": v(-57.83, 143.16) * mm});
            skLineSegment(sketch, "E21.9.6.7", {"start": v(-57.83, 147.56) * mm, "end": v(-57.83, 148.16) * mm});
            skLineSegment(sketch, "E21.10.0.0", {"start": v(-81.83, -142.84) * mm, "end": v(-85.83, -142.84) * mm});
            skLineSegment(sketch, "E21.10.0.1", {"start": v(-81.83, -147.24) * mm, "end": v(-85.83, -147.24) * mm});
            skLineSegment(sketch, "E21.10.0.2", {"start": v(-81.83, -142.24) * mm, "end": v(-85.83, -142.24) * mm});
            skLineSegment(sketch, "E21.10.0.3", {"start": v(-81.83, -147.84) * mm, "end": v(-85.83, -147.84) * mm});
            skLineSegment(sketch, "E21.10.0.4", {"start": v(-81.83, -142.84) * mm, "end": v(-81.83, -142.24) * mm});
            skLineSegment(sketch, "E21.10.0.5", {"start": v(-81.83, -147.84) * mm, "end": v(-81.83, -147.24) * mm});
            skLineSegment(sketch, "E21.10.0.6", {"start": v(-85.83, -147.84) * mm, "end": v(-85.83, -147.24) * mm});
            skLineSegment(sketch, "E21.10.0.7", {"start": v(-85.83, -142.84) * mm, "end": v(-85.83, -142.24) * mm});
            skLineSegment(sketch, "E21.10.1.0", {"start": v(-81.83, -94.44) * mm, "end": v(-85.83, -94.44) * mm});
            skLineSegment(sketch, "E21.10.1.1", {"start": v(-81.83, -98.84) * mm, "end": v(-85.83, -98.84) * mm});
            skLineSegment(sketch, "E21.10.1.2", {"start": v(-81.83, -93.84) * mm, "end": v(-85.83, -93.84) * mm});
            skLineSegment(sketch, "E21.10.1.3", {"start": v(-81.83, -99.44) * mm, "end": v(-85.83, -99.44) * mm});
            skLineSegment(sketch, "E21.10.1.4", {"start": v(-81.83, -94.44) * mm, "end": v(-81.83, -93.84) * mm});
            skLineSegment(sketch, "E21.10.1.5", {"start": v(-81.83, -99.44) * mm, "end": v(-81.83, -98.84) * mm});
            skLineSegment(sketch, "E21.10.1.6", {"start": v(-85.83, -99.44) * mm, "end": v(-85.83, -98.84) * mm});
            skLineSegment(sketch, "E21.10.1.7", {"start": v(-85.83, -94.44) * mm, "end": v(-85.83, -93.84) * mm});
            skLineSegment(sketch, "E21.10.2.0", {"start": v(-81.83, -46.04) * mm, "end": v(-85.83, -46.04) * mm});
            skLineSegment(sketch, "E21.10.2.1", {"start": v(-81.83, -50.44) * mm, "end": v(-85.83, -50.44) * mm});
            skLineSegment(sketch, "E21.10.2.2", {"start": v(-81.83, -45.44) * mm, "end": v(-85.83, -45.44) * mm});
            skLineSegment(sketch, "E21.10.2.3", {"start": v(-81.83, -51.04) * mm, "end": v(-85.83, -51.04) * mm});
            skLineSegment(sketch, "E21.10.2.4", {"start": v(-81.83, -46.04) * mm, "end": v(-81.83, -45.44) * mm});
            skLineSegment(sketch, "E21.10.2.5", {"start": v(-81.83, -51.04) * mm, "end": v(-81.83, -50.44) * mm});
            skLineSegment(sketch, "E21.10.2.6", {"start": v(-85.83, -51.04) * mm, "end": v(-85.83, -50.44) * mm});
            skLineSegment(sketch, "E21.10.2.7", {"start": v(-85.83, -46.04) * mm, "end": v(-85.83, -45.44) * mm});
            skLineSegment(sketch, "E21.10.3.0", {"start": v(-81.83, 2.36) * mm, "end": v(-85.83, 2.36) * mm});
            skLineSegment(sketch, "E21.10.3.1", {"start": v(-81.83, -2.04) * mm, "end": v(-85.83, -2.04) * mm});
            skLineSegment(sketch, "E21.10.3.2", {"start": v(-81.83, 2.96) * mm, "end": v(-85.83, 2.96) * mm});
            skLineSegment(sketch, "E21.10.3.3", {"start": v(-81.83, -2.64) * mm, "end": v(-85.83, -2.64) * mm});
            skLineSegment(sketch, "E21.10.3.4", {"start": v(-81.83, 2.36) * mm, "end": v(-81.83, 2.96) * mm});
            skLineSegment(sketch, "E21.10.3.5", {"start": v(-81.83, -2.64) * mm, "end": v(-81.83, -2.04) * mm});
            skLineSegment(sketch, "E21.10.3.6", {"start": v(-85.83, -2.64) * mm, "end": v(-85.83, -2.04) * mm});
            skLineSegment(sketch, "E21.10.3.7", {"start": v(-85.83, 2.36) * mm, "end": v(-85.83, 2.96) * mm});
            skLineSegment(sketch, "E21.10.4.0", {"start": v(-81.83, 50.76) * mm, "end": v(-85.83, 50.76) * mm});
            skLineSegment(sketch, "E21.10.4.1", {"start": v(-81.83, 46.36) * mm, "end": v(-85.83, 46.36) * mm});
            skLineSegment(sketch, "E21.10.4.2", {"start": v(-81.83, 51.36) * mm, "end": v(-85.83, 51.36) * mm});
            skLineSegment(sketch, "E21.10.4.3", {"start": v(-81.83, 45.76) * mm, "end": v(-85.83, 45.76) * mm});
            skLineSegment(sketch, "E21.10.4.4", {"start": v(-81.83, 50.76) * mm, "end": v(-81.83, 51.36) * mm});
            skLineSegment(sketch, "E21.10.4.5", {"start": v(-81.83, 45.76) * mm, "end": v(-81.83, 46.36) * mm});
            skLineSegment(sketch, "E21.10.4.6", {"start": v(-85.83, 45.76) * mm, "end": v(-85.83, 46.36) * mm});
            skLineSegment(sketch, "E21.10.4.7", {"start": v(-85.83, 50.76) * mm, "end": v(-85.83, 51.36) * mm});
            skLineSegment(sketch, "E21.10.5.0", {"start": v(-81.83, 99.16) * mm, "end": v(-85.83, 99.16) * mm});
            skLineSegment(sketch, "E21.10.5.1", {"start": v(-81.83, 94.76) * mm, "end": v(-85.83, 94.76) * mm});
            skLineSegment(sketch, "E21.10.5.2", {"start": v(-81.83, 99.76) * mm, "end": v(-85.83, 99.76) * mm});
            skLineSegment(sketch, "E21.10.5.3", {"start": v(-81.83, 94.16) * mm, "end": v(-85.83, 94.16) * mm});
            skLineSegment(sketch, "E21.10.5.4", {"start": v(-81.83, 99.16) * mm, "end": v(-81.83, 99.76) * mm});
            skLineSegment(sketch, "E21.10.5.5", {"start": v(-81.83, 94.16) * mm, "end": v(-81.83, 94.76) * mm});
            skLineSegment(sketch, "E21.10.5.6", {"start": v(-85.83, 94.16) * mm, "end": v(-85.83, 94.76) * mm});
            skLineSegment(sketch, "E21.10.5.7", {"start": v(-85.83, 99.16) * mm, "end": v(-85.83, 99.76) * mm});
            skLineSegment(sketch, "E21.10.6.0", {"start": v(-81.83, 147.56) * mm, "end": v(-85.83, 147.56) * mm});
            skLineSegment(sketch, "E21.10.6.1", {"start": v(-81.83, 143.16) * mm, "end": v(-85.83, 143.16) * mm});
            skLineSegment(sketch, "E21.10.6.2", {"start": v(-81.83, 148.16) * mm, "end": v(-85.83, 148.16) * mm});
            skLineSegment(sketch, "E21.10.6.3", {"start": v(-81.83, 142.56) * mm, "end": v(-85.83, 142.56) * mm});
            skLineSegment(sketch, "E21.10.6.4", {"start": v(-81.83, 147.56) * mm, "end": v(-81.83, 148.16) * mm});
            skLineSegment(sketch, "E21.10.6.5", {"start": v(-81.83, 142.56) * mm, "end": v(-81.83, 143.16) * mm});
            skLineSegment(sketch, "E21.10.6.6", {"start": v(-85.83, 142.56) * mm, "end": v(-85.83, 143.16) * mm});
            skLineSegment(sketch, "E21.10.6.7", {"start": v(-85.83, 147.56) * mm, "end": v(-85.83, 148.16) * mm});
            skLineSegment(sketch, "E21.11.0.0", {"start": v(-109.83, -142.84) * mm, "end": v(-113.83, -142.84) * mm});
            skLineSegment(sketch, "E21.11.0.1", {"start": v(-109.83, -147.24) * mm, "end": v(-113.83, -147.24) * mm});
            skLineSegment(sketch, "E21.11.0.2", {"start": v(-109.83, -142.24) * mm, "end": v(-113.83, -142.24) * mm});
            skLineSegment(sketch, "E21.11.0.3", {"start": v(-109.83, -147.84) * mm, "end": v(-113.83, -147.84) * mm});
            skLineSegment(sketch, "E21.11.0.4", {"start": v(-109.83, -142.84) * mm, "end": v(-109.83, -142.24) * mm});
            skLineSegment(sketch, "E21.11.0.5", {"start": v(-109.83, -147.84) * mm, "end": v(-109.83, -147.24) * mm});
            skLineSegment(sketch, "E21.11.0.6", {"start": v(-113.83, -147.84) * mm, "end": v(-113.83, -147.24) * mm});
            skLineSegment(sketch, "E21.11.0.7", {"start": v(-113.83, -142.84) * mm, "end": v(-113.83, -142.24) * mm});
            skLineSegment(sketch, "E21.11.1.0", {"start": v(-109.83, -94.44) * mm, "end": v(-113.83, -94.44) * mm});
            skLineSegment(sketch, "E21.11.1.1", {"start": v(-109.83, -98.84) * mm, "end": v(-113.83, -98.84) * mm});
            skLineSegment(sketch, "E21.11.1.2", {"start": v(-109.83, -93.84) * mm, "end": v(-113.83, -93.84) * mm});
            skLineSegment(sketch, "E21.11.1.3", {"start": v(-109.83, -99.44) * mm, "end": v(-113.83, -99.44) * mm});
            skLineSegment(sketch, "E21.11.1.4", {"start": v(-109.83, -94.44) * mm, "end": v(-109.83, -93.84) * mm});
            skLineSegment(sketch, "E21.11.1.5", {"start": v(-109.83, -99.44) * mm, "end": v(-109.83, -98.84) * mm});
            skLineSegment(sketch, "E21.11.1.6", {"start": v(-113.83, -99.44) * mm, "end": v(-113.83, -98.84) * mm});
            skLineSegment(sketch, "E21.11.1.7", {"start": v(-113.83, -94.44) * mm, "end": v(-113.83, -93.84) * mm});
            skLineSegment(sketch, "E21.11.2.0", {"start": v(-109.83, -46.04) * mm, "end": v(-113.83, -46.04) * mm});
            skLineSegment(sketch, "E21.11.2.1", {"start": v(-109.83, -50.44) * mm, "end": v(-113.83, -50.44) * mm});
            skLineSegment(sketch, "E21.11.2.2", {"start": v(-109.83, -45.44) * mm, "end": v(-113.83, -45.44) * mm});
            skLineSegment(sketch, "E21.11.2.3", {"start": v(-109.83, -51.04) * mm, "end": v(-113.83, -51.04) * mm});
            skLineSegment(sketch, "E21.11.2.4", {"start": v(-109.83, -46.04) * mm, "end": v(-109.83, -45.44) * mm});
            skLineSegment(sketch, "E21.11.2.5", {"start": v(-109.83, -51.04) * mm, "end": v(-109.83, -50.44) * mm});
            skLineSegment(sketch, "E21.11.2.6", {"start": v(-113.83, -51.04) * mm, "end": v(-113.83, -50.44) * mm});
            skLineSegment(sketch, "E21.11.2.7", {"start": v(-113.83, -46.04) * mm, "end": v(-113.83, -45.44) * mm});
            skLineSegment(sketch, "E21.11.3.0", {"start": v(-109.83, 2.36) * mm, "end": v(-113.83, 2.36) * mm});
            skLineSegment(sketch, "E21.11.3.1", {"start": v(-109.83, -2.04) * mm, "end": v(-113.83, -2.04) * mm});
            skLineSegment(sketch, "E21.11.3.2", {"start": v(-109.83, 2.96) * mm, "end": v(-113.83, 2.96) * mm});
            skLineSegment(sketch, "E21.11.3.3", {"start": v(-109.83, -2.64) * mm, "end": v(-113.83, -2.64) * mm});
            skLineSegment(sketch, "E21.11.3.4", {"start": v(-109.83, 2.36) * mm, "end": v(-109.83, 2.96) * mm});
            skLineSegment(sketch, "E21.11.3.5", {"start": v(-109.83, -2.64) * mm, "end": v(-109.83, -2.04) * mm});
            skLineSegment(sketch, "E21.11.3.6", {"start": v(-113.83, -2.64) * mm, "end": v(-113.83, -2.04) * mm});
            skLineSegment(sketch, "E21.11.3.7", {"start": v(-113.83, 2.36) * mm, "end": v(-113.83, 2.96) * mm});
            skLineSegment(sketch, "E21.11.4.0", {"start": v(-109.83, 50.76) * mm, "end": v(-113.83, 50.76) * mm});
            skLineSegment(sketch, "E21.11.4.1", {"start": v(-109.83, 46.36) * mm, "end": v(-113.83, 46.36) * mm});
            skLineSegment(sketch, "E21.11.4.2", {"start": v(-109.83, 51.36) * mm, "end": v(-113.83, 51.36) * mm});
            skLineSegment(sketch, "E21.11.4.3", {"start": v(-109.83, 45.76) * mm, "end": v(-113.83, 45.76) * mm});
            skLineSegment(sketch, "E21.11.4.4", {"start": v(-109.83, 50.76) * mm, "end": v(-109.83, 51.36) * mm});
            skLineSegment(sketch, "E21.11.4.5", {"start": v(-109.83, 45.76) * mm, "end": v(-109.83, 46.36) * mm});
            skLineSegment(sketch, "E21.11.4.6", {"start": v(-113.83, 45.76) * mm, "end": v(-113.83, 46.36) * mm});
            skLineSegment(sketch, "E21.11.4.7", {"start": v(-113.83, 50.76) * mm, "end": v(-113.83, 51.36) * mm});
            skLineSegment(sketch, "E21.11.5.0", {"start": v(-109.83, 99.16) * mm, "end": v(-113.83, 99.16) * mm});
            skLineSegment(sketch, "E21.11.5.1", {"start": v(-109.83, 94.76) * mm, "end": v(-113.83, 94.76) * mm});
            skLineSegment(sketch, "E21.11.5.2", {"start": v(-109.83, 99.76) * mm, "end": v(-113.83, 99.76) * mm});
            skLineSegment(sketch, "E21.11.5.3", {"start": v(-109.83, 94.16) * mm, "end": v(-113.83, 94.16) * mm});
            skLineSegment(sketch, "E21.11.5.4", {"start": v(-109.83, 99.16) * mm, "end": v(-109.83, 99.76) * mm});
            skLineSegment(sketch, "E21.11.5.5", {"start": v(-109.83, 94.16) * mm, "end": v(-109.83, 94.76) * mm});
            skLineSegment(sketch, "E21.11.5.6", {"start": v(-113.83, 94.16) * mm, "end": v(-113.83, 94.76) * mm});
            skLineSegment(sketch, "E21.11.5.7", {"start": v(-113.83, 99.16) * mm, "end": v(-113.83, 99.76) * mm});
            skLineSegment(sketch, "E21.11.6.0", {"start": v(-109.83, 147.56) * mm, "end": v(-113.83, 147.56) * mm});
            skLineSegment(sketch, "E21.11.6.1", {"start": v(-109.83, 143.16) * mm, "end": v(-113.83, 143.16) * mm});
            skLineSegment(sketch, "E21.11.6.2", {"start": v(-109.83, 148.16) * mm, "end": v(-113.83, 148.16) * mm});
            skLineSegment(sketch, "E21.11.6.3", {"start": v(-109.83, 142.56) * mm, "end": v(-113.83, 142.56) * mm});
            skLineSegment(sketch, "E21.11.6.4", {"start": v(-109.83, 147.56) * mm, "end": v(-109.83, 148.16) * mm});
            skLineSegment(sketch, "E21.11.6.5", {"start": v(-109.83, 142.56) * mm, "end": v(-109.83, 143.16) * mm});
            skLineSegment(sketch, "E21.11.6.6", {"start": v(-113.83, 142.56) * mm, "end": v(-113.83, 143.16) * mm});
            skLineSegment(sketch, "E21.11.6.7", {"start": v(-113.83, 147.56) * mm, "end": v(-113.83, 148.16) * mm});
            skLineSegment(sketch, "E21.12.0.0", {"start": v(-137.83, -142.84) * mm, "end": v(-141.83, -142.84) * mm});
            skLineSegment(sketch, "E21.12.0.1", {"start": v(-137.83, -147.24) * mm, "end": v(-141.83, -147.24) * mm});
            skLineSegment(sketch, "E21.12.0.2", {"start": v(-137.83, -142.24) * mm, "end": v(-141.83, -142.24) * mm});
            skLineSegment(sketch, "E21.12.0.3", {"start": v(-137.83, -147.84) * mm, "end": v(-141.83, -147.84) * mm});
            skLineSegment(sketch, "E21.12.0.4", {"start": v(-137.83, -142.84) * mm, "end": v(-137.83, -142.24) * mm});
            skLineSegment(sketch, "E21.12.0.5", {"start": v(-137.83, -147.84) * mm, "end": v(-137.83, -147.24) * mm});
            skLineSegment(sketch, "E21.12.0.6", {"start": v(-141.83, -147.84) * mm, "end": v(-141.83, -147.24) * mm});
            skLineSegment(sketch, "E21.12.0.7", {"start": v(-141.83, -142.84) * mm, "end": v(-141.83, -142.24) * mm});
            skLineSegment(sketch, "E21.12.1.0", {"start": v(-137.83, -94.44) * mm, "end": v(-141.83, -94.44) * mm});
            skLineSegment(sketch, "E21.12.1.1", {"start": v(-137.83, -98.84) * mm, "end": v(-141.83, -98.84) * mm});
            skLineSegment(sketch, "E21.12.1.2", {"start": v(-137.83, -93.84) * mm, "end": v(-141.83, -93.84) * mm});
            skLineSegment(sketch, "E21.12.1.3", {"start": v(-137.83, -99.44) * mm, "end": v(-141.83, -99.44) * mm});
            skLineSegment(sketch, "E21.12.1.4", {"start": v(-137.83, -94.44) * mm, "end": v(-137.83, -93.84) * mm});
            skLineSegment(sketch, "E21.12.1.5", {"start": v(-137.83, -99.44) * mm, "end": v(-137.83, -98.84) * mm});
            skLineSegment(sketch, "E21.12.1.6", {"start": v(-141.83, -99.44) * mm, "end": v(-141.83, -98.84) * mm});
            skLineSegment(sketch, "E21.12.1.7", {"start": v(-141.83, -94.44) * mm, "end": v(-141.83, -93.84) * mm});
            skLineSegment(sketch, "E21.12.2.0", {"start": v(-137.83, -46.04) * mm, "end": v(-141.83, -46.04) * mm});
            skLineSegment(sketch, "E21.12.2.1", {"start": v(-137.83, -50.44) * mm, "end": v(-141.83, -50.44) * mm});
            skLineSegment(sketch, "E21.12.2.2", {"start": v(-137.83, -45.44) * mm, "end": v(-141.83, -45.44) * mm});
            skLineSegment(sketch, "E21.12.2.3", {"start": v(-137.83, -51.04) * mm, "end": v(-141.83, -51.04) * mm});
            skLineSegment(sketch, "E21.12.2.4", {"start": v(-137.83, -46.04) * mm, "end": v(-137.83, -45.44) * mm});
            skLineSegment(sketch, "E21.12.2.5", {"start": v(-137.83, -51.04) * mm, "end": v(-137.83, -50.44) * mm});
            skLineSegment(sketch, "E21.12.2.6", {"start": v(-141.83, -51.04) * mm, "end": v(-141.83, -50.44) * mm});
            skLineSegment(sketch, "E21.12.2.7", {"start": v(-141.83, -46.04) * mm, "end": v(-141.83, -45.44) * mm});
            skLineSegment(sketch, "E21.12.3.0", {"start": v(-137.83, 2.36) * mm, "end": v(-141.83, 2.36) * mm});
            skLineSegment(sketch, "E21.12.3.1", {"start": v(-137.83, -2.04) * mm, "end": v(-141.83, -2.04) * mm});
            skLineSegment(sketch, "E21.12.3.2", {"start": v(-137.83, 2.96) * mm, "end": v(-141.83, 2.96) * mm});
            skLineSegment(sketch, "E21.12.3.3", {"start": v(-137.83, -2.64) * mm, "end": v(-141.83, -2.64) * mm});
            skLineSegment(sketch, "E21.12.3.4", {"start": v(-137.83, 2.36) * mm, "end": v(-137.83, 2.96) * mm});
            skLineSegment(sketch, "E21.12.3.5", {"start": v(-137.83, -2.64) * mm, "end": v(-137.83, -2.04) * mm});
            skLineSegment(sketch, "E21.12.3.6", {"start": v(-141.83, -2.64) * mm, "end": v(-141.83, -2.04) * mm});
            skLineSegment(sketch, "E21.12.3.7", {"start": v(-141.83, 2.36) * mm, "end": v(-141.83, 2.96) * mm});
            skLineSegment(sketch, "E21.12.4.0", {"start": v(-137.83, 50.76) * mm, "end": v(-141.83, 50.76) * mm});
            skLineSegment(sketch, "E21.12.4.1", {"start": v(-137.83, 46.36) * mm, "end": v(-141.83, 46.36) * mm});
            skLineSegment(sketch, "E21.12.4.2", {"start": v(-137.83, 51.36) * mm, "end": v(-141.83, 51.36) * mm});
            skLineSegment(sketch, "E21.12.4.3", {"start": v(-137.83, 45.76) * mm, "end": v(-141.83, 45.76) * mm});
            skLineSegment(sketch, "E21.12.4.4", {"start": v(-137.83, 50.76) * mm, "end": v(-137.83, 51.36) * mm});
            skLineSegment(sketch, "E21.12.4.5", {"start": v(-137.83, 45.76) * mm, "end": v(-137.83, 46.36) * mm});
            skLineSegment(sketch, "E21.12.4.6", {"start": v(-141.83, 45.76) * mm, "end": v(-141.83, 46.36) * mm});
            skLineSegment(sketch, "E21.12.4.7", {"start": v(-141.83, 50.76) * mm, "end": v(-141.83, 51.36) * mm});
            skLineSegment(sketch, "E21.12.5.0", {"start": v(-137.83, 99.16) * mm, "end": v(-141.83, 99.16) * mm});
            skLineSegment(sketch, "E21.12.5.1", {"start": v(-137.83, 94.76) * mm, "end": v(-141.83, 94.76) * mm});
            skLineSegment(sketch, "E21.12.5.2", {"start": v(-137.83, 99.76) * mm, "end": v(-141.83, 99.76) * mm});
            skLineSegment(sketch, "E21.12.5.3", {"start": v(-137.83, 94.16) * mm, "end": v(-141.83, 94.16) * mm});
            skLineSegment(sketch, "E21.12.5.4", {"start": v(-137.83, 99.16) * mm, "end": v(-137.83, 99.76) * mm});
            skLineSegment(sketch, "E21.12.5.5", {"start": v(-137.83, 94.16) * mm, "end": v(-137.83, 94.76) * mm});
            skLineSegment(sketch, "E21.12.5.6", {"start": v(-141.83, 94.16) * mm, "end": v(-141.83, 94.76) * mm});
            skLineSegment(sketch, "E21.12.5.7", {"start": v(-141.83, 99.16) * mm, "end": v(-141.83, 99.76) * mm});
            skLineSegment(sketch, "E21.12.6.0", {"start": v(-137.83, 147.56) * mm, "end": v(-141.83, 147.56) * mm});
            skLineSegment(sketch, "E21.12.6.1", {"start": v(-137.83, 143.16) * mm, "end": v(-141.83, 143.16) * mm});
            skLineSegment(sketch, "E21.12.6.2", {"start": v(-137.83, 148.16) * mm, "end": v(-141.83, 148.16) * mm});
            skLineSegment(sketch, "E21.12.6.3", {"start": v(-137.83, 142.56) * mm, "end": v(-141.83, 142.56) * mm});
            skLineSegment(sketch, "E21.12.6.4", {"start": v(-137.83, 147.56) * mm, "end": v(-137.83, 148.16) * mm});
            skLineSegment(sketch, "E21.12.6.5", {"start": v(-137.83, 142.56) * mm, "end": v(-137.83, 143.16) * mm});
            skLineSegment(sketch, "E21.12.6.6", {"start": v(-141.83, 142.56) * mm, "end": v(-141.83, 143.16) * mm});
            skLineSegment(sketch, "E21.12.6.7", {"start": v(-141.83, 147.56) * mm, "end": v(-141.83, 148.16) * mm});
            skLineSegment(sketch, "E21.13.0.0", {"start": v(-165.83, -142.84) * mm, "end": v(-169.83, -142.84) * mm});
            skLineSegment(sketch, "E21.13.0.1", {"start": v(-165.83, -147.24) * mm, "end": v(-169.83, -147.24) * mm});
            skLineSegment(sketch, "E21.13.0.2", {"start": v(-165.83, -142.24) * mm, "end": v(-169.83, -142.24) * mm});
            skLineSegment(sketch, "E21.13.0.3", {"start": v(-165.83, -147.84) * mm, "end": v(-169.83, -147.84) * mm});
            skLineSegment(sketch, "E21.13.0.4", {"start": v(-165.83, -142.84) * mm, "end": v(-165.83, -142.24) * mm});
            skLineSegment(sketch, "E21.13.0.5", {"start": v(-165.83, -147.84) * mm, "end": v(-165.83, -147.24) * mm});
            skLineSegment(sketch, "E21.13.0.6", {"start": v(-169.83, -147.84) * mm, "end": v(-169.83, -147.24) * mm});
            skLineSegment(sketch, "E21.13.0.7", {"start": v(-169.83, -142.84) * mm, "end": v(-169.83, -142.24) * mm});
            skLineSegment(sketch, "E21.13.1.0", {"start": v(-165.83, -94.44) * mm, "end": v(-169.83, -94.44) * mm});
            skLineSegment(sketch, "E21.13.1.1", {"start": v(-165.83, -98.84) * mm, "end": v(-169.83, -98.84) * mm});
            skLineSegment(sketch, "E21.13.1.2", {"start": v(-165.83, -93.84) * mm, "end": v(-169.83, -93.84) * mm});
            skLineSegment(sketch, "E21.13.1.3", {"start": v(-165.83, -99.44) * mm, "end": v(-169.83, -99.44) * mm});
            skLineSegment(sketch, "E21.13.1.4", {"start": v(-165.83, -94.44) * mm, "end": v(-165.83, -93.84) * mm});
            skLineSegment(sketch, "E21.13.1.5", {"start": v(-165.83, -99.44) * mm, "end": v(-165.83, -98.84) * mm});
            skLineSegment(sketch, "E21.13.1.6", {"start": v(-169.83, -99.44) * mm, "end": v(-169.83, -98.84) * mm});
            skLineSegment(sketch, "E21.13.1.7", {"start": v(-169.83, -94.44) * mm, "end": v(-169.83, -93.84) * mm});
            skLineSegment(sketch, "E21.13.2.0", {"start": v(-165.83, -46.04) * mm, "end": v(-169.83, -46.04) * mm});
            skLineSegment(sketch, "E21.13.2.1", {"start": v(-165.83, -50.44) * mm, "end": v(-169.83, -50.44) * mm});
            skLineSegment(sketch, "E21.13.2.2", {"start": v(-165.83, -45.44) * mm, "end": v(-169.83, -45.44) * mm});
            skLineSegment(sketch, "E21.13.2.3", {"start": v(-165.83, -51.04) * mm, "end": v(-169.83, -51.04) * mm});
            skLineSegment(sketch, "E21.13.2.4", {"start": v(-165.83, -46.04) * mm, "end": v(-165.83, -45.44) * mm});
            skLineSegment(sketch, "E21.13.2.5", {"start": v(-165.83, -51.04) * mm, "end": v(-165.83, -50.44) * mm});
            skLineSegment(sketch, "E21.13.2.6", {"start": v(-169.83, -51.04) * mm, "end": v(-169.83, -50.44) * mm});
            skLineSegment(sketch, "E21.13.2.7", {"start": v(-169.83, -46.04) * mm, "end": v(-169.83, -45.44) * mm});
            skLineSegment(sketch, "E21.13.3.0", {"start": v(-165.83, 2.36) * mm, "end": v(-169.83, 2.36) * mm});
            skLineSegment(sketch, "E21.13.3.1", {"start": v(-165.83, -2.04) * mm, "end": v(-169.83, -2.04) * mm});
            skLineSegment(sketch, "E21.13.3.2", {"start": v(-165.83, 2.96) * mm, "end": v(-169.83, 2.96) * mm});
            skLineSegment(sketch, "E21.13.3.3", {"start": v(-165.83, -2.64) * mm, "end": v(-169.83, -2.64) * mm});
            skLineSegment(sketch, "E21.13.3.4", {"start": v(-165.83, 2.36) * mm, "end": v(-165.83, 2.96) * mm});
            skLineSegment(sketch, "E21.13.3.5", {"start": v(-165.83, -2.64) * mm, "end": v(-165.83, -2.04) * mm});
            skLineSegment(sketch, "E21.13.3.6", {"start": v(-169.83, -2.64) * mm, "end": v(-169.83, -2.04) * mm});
            skLineSegment(sketch, "E21.13.3.7", {"start": v(-169.83, 2.36) * mm, "end": v(-169.83, 2.96) * mm});
            skLineSegment(sketch, "E21.13.4.0", {"start": v(-165.83, 50.76) * mm, "end": v(-169.83, 50.76) * mm});
            skLineSegment(sketch, "E21.13.4.1", {"start": v(-165.83, 46.36) * mm, "end": v(-169.83, 46.36) * mm});
            skLineSegment(sketch, "E21.13.4.2", {"start": v(-165.83, 51.36) * mm, "end": v(-169.83, 51.36) * mm});
            skLineSegment(sketch, "E21.13.4.3", {"start": v(-165.83, 45.76) * mm, "end": v(-169.83, 45.76) * mm});
            skLineSegment(sketch, "E21.13.4.4", {"start": v(-165.83, 50.76) * mm, "end": v(-165.83, 51.36) * mm});
            skLineSegment(sketch, "E21.13.4.5", {"start": v(-165.83, 45.76) * mm, "end": v(-165.83, 46.36) * mm});
            skLineSegment(sketch, "E21.13.4.6", {"start": v(-169.83, 45.76) * mm, "end": v(-169.83, 46.36) * mm});
            skLineSegment(sketch, "E21.13.4.7", {"start": v(-169.83, 50.76) * mm, "end": v(-169.83, 51.36) * mm});
            skLineSegment(sketch, "E21.13.5.0", {"start": v(-165.83, 99.16) * mm, "end": v(-169.83, 99.16) * mm});
            skLineSegment(sketch, "E21.13.5.1", {"start": v(-165.83, 94.76) * mm, "end": v(-169.83, 94.76) * mm});
            skLineSegment(sketch, "E21.13.5.2", {"start": v(-165.83, 99.76) * mm, "end": v(-169.83, 99.76) * mm});
            skLineSegment(sketch, "E21.13.5.3", {"start": v(-165.83, 94.16) * mm, "end": v(-169.83, 94.16) * mm});
            skLineSegment(sketch, "E21.13.5.4", {"start": v(-165.83, 99.16) * mm, "end": v(-165.83, 99.76) * mm});
            skLineSegment(sketch, "E21.13.5.5", {"start": v(-165.83, 94.16) * mm, "end": v(-165.83, 94.76) * mm});
            skLineSegment(sketch, "E21.13.5.6", {"start": v(-169.83, 94.16) * mm, "end": v(-169.83, 94.76) * mm});
            skLineSegment(sketch, "E21.13.5.7", {"start": v(-169.83, 99.16) * mm, "end": v(-169.83, 99.76) * mm});
            skLineSegment(sketch, "E21.13.6.0", {"start": v(-165.83, 147.56) * mm, "end": v(-169.83, 147.56) * mm});
            skLineSegment(sketch, "E21.13.6.1", {"start": v(-165.83, 143.16) * mm, "end": v(-169.83, 143.16) * mm});
            skLineSegment(sketch, "E21.13.6.2", {"start": v(-165.83, 148.16) * mm, "end": v(-169.83, 148.16) * mm});
            skLineSegment(sketch, "E21.13.6.3", {"start": v(-165.83, 142.56) * mm, "end": v(-169.83, 142.56) * mm});
            skLineSegment(sketch, "E21.13.6.4", {"start": v(-165.83, 147.56) * mm, "end": v(-165.83, 148.16) * mm});
            skLineSegment(sketch, "E21.13.6.5", {"start": v(-165.83, 142.56) * mm, "end": v(-165.83, 143.16) * mm});
            skLineSegment(sketch, "E21.13.6.6", {"start": v(-169.83, 142.56) * mm, "end": v(-169.83, 143.16) * mm});
            skLineSegment(sketch, "E21.13.6.7", {"start": v(-169.83, 147.56) * mm, "end": v(-169.83, 148.16) * mm});
            skLineSegment(sketch, "E21.14.0.0", {"start": v(-193.83, -142.84) * mm, "end": v(-197.83, -142.84) * mm});
            skLineSegment(sketch, "E21.14.0.1", {"start": v(-193.83, -147.24) * mm, "end": v(-197.83, -147.24) * mm});
            skLineSegment(sketch, "E21.14.0.2", {"start": v(-193.83, -142.24) * mm, "end": v(-197.83, -142.24) * mm});
            skLineSegment(sketch, "E21.14.0.3", {"start": v(-193.83, -147.84) * mm, "end": v(-197.83, -147.84) * mm});
            skLineSegment(sketch, "E21.14.0.4", {"start": v(-193.83, -142.84) * mm, "end": v(-193.83, -142.24) * mm});
            skLineSegment(sketch, "E21.14.0.5", {"start": v(-193.83, -147.84) * mm, "end": v(-193.83, -147.24) * mm});
            skLineSegment(sketch, "E21.14.0.6", {"start": v(-197.83, -147.84) * mm, "end": v(-197.83, -147.24) * mm});
            skLineSegment(sketch, "E21.14.0.7", {"start": v(-197.83, -142.84) * mm, "end": v(-197.83, -142.24) * mm});
            skLineSegment(sketch, "E21.14.1.0", {"start": v(-193.83, -94.44) * mm, "end": v(-197.83, -94.44) * mm});
            skLineSegment(sketch, "E21.14.1.1", {"start": v(-193.83, -98.84) * mm, "end": v(-197.83, -98.84) * mm});
            skLineSegment(sketch, "E21.14.1.2", {"start": v(-193.83, -93.84) * mm, "end": v(-197.83, -93.84) * mm});
            skLineSegment(sketch, "E21.14.1.3", {"start": v(-193.83, -99.44) * mm, "end": v(-197.83, -99.44) * mm});
            skLineSegment(sketch, "E21.14.1.4", {"start": v(-193.83, -94.44) * mm, "end": v(-193.83, -93.84) * mm});
            skLineSegment(sketch, "E21.14.1.5", {"start": v(-193.83, -99.44) * mm, "end": v(-193.83, -98.84) * mm});
            skLineSegment(sketch, "E21.14.1.6", {"start": v(-197.83, -99.44) * mm, "end": v(-197.83, -98.84) * mm});
            skLineSegment(sketch, "E21.14.1.7", {"start": v(-197.83, -94.44) * mm, "end": v(-197.83, -93.84) * mm});
            skLineSegment(sketch, "E21.14.2.0", {"start": v(-193.83, -46.04) * mm, "end": v(-197.83, -46.04) * mm});
            skLineSegment(sketch, "E21.14.2.1", {"start": v(-193.83, -50.44) * mm, "end": v(-197.83, -50.44) * mm});
            skLineSegment(sketch, "E21.14.2.2", {"start": v(-193.83, -45.44) * mm, "end": v(-197.83, -45.44) * mm});
            skLineSegment(sketch, "E21.14.2.3", {"start": v(-193.83, -51.04) * mm, "end": v(-197.83, -51.04) * mm});
            skLineSegment(sketch, "E21.14.2.4", {"start": v(-193.83, -46.04) * mm, "end": v(-193.83, -45.44) * mm});
            skLineSegment(sketch, "E21.14.2.5", {"start": v(-193.83, -51.04) * mm, "end": v(-193.83, -50.44) * mm});
            skLineSegment(sketch, "E21.14.2.6", {"start": v(-197.83, -51.04) * mm, "end": v(-197.83, -50.44) * mm});
            skLineSegment(sketch, "E21.14.2.7", {"start": v(-197.83, -46.04) * mm, "end": v(-197.83, -45.44) * mm});
            skLineSegment(sketch, "E21.14.3.0", {"start": v(-193.83, 2.36) * mm, "end": v(-197.83, 2.36) * mm});
            skLineSegment(sketch, "E21.14.3.1", {"start": v(-193.83, -2.04) * mm, "end": v(-197.83, -2.04) * mm});
            skLineSegment(sketch, "E21.14.3.2", {"start": v(-193.83, 2.96) * mm, "end": v(-197.83, 2.96) * mm});
            skLineSegment(sketch, "E21.14.3.3", {"start": v(-193.83, -2.64) * mm, "end": v(-197.83, -2.64) * mm});
            skLineSegment(sketch, "E21.14.3.4", {"start": v(-193.83, 2.36) * mm, "end": v(-193.83, 2.96) * mm});
            skLineSegment(sketch, "E21.14.3.5", {"start": v(-193.83, -2.64) * mm, "end": v(-193.83, -2.04) * mm});
            skLineSegment(sketch, "E21.14.3.6", {"start": v(-197.83, -2.64) * mm, "end": v(-197.83, -2.04) * mm});
            skLineSegment(sketch, "E21.14.3.7", {"start": v(-197.83, 2.36) * mm, "end": v(-197.83, 2.96) * mm});
            skLineSegment(sketch, "E21.14.4.0", {"start": v(-193.83, 50.76) * mm, "end": v(-197.83, 50.76) * mm});
            skLineSegment(sketch, "E21.14.4.1", {"start": v(-193.83, 46.36) * mm, "end": v(-197.83, 46.36) * mm});
            skLineSegment(sketch, "E21.14.4.2", {"start": v(-193.83, 51.36) * mm, "end": v(-197.83, 51.36) * mm});
            skLineSegment(sketch, "E21.14.4.3", {"start": v(-193.83, 45.76) * mm, "end": v(-197.83, 45.76) * mm});
            skLineSegment(sketch, "E21.14.4.4", {"start": v(-193.83, 50.76) * mm, "end": v(-193.83, 51.36) * mm});
            skLineSegment(sketch, "E21.14.4.5", {"start": v(-193.83, 45.76) * mm, "end": v(-193.83, 46.36) * mm});
            skLineSegment(sketch, "E21.14.4.6", {"start": v(-197.83, 45.76) * mm, "end": v(-197.83, 46.36) * mm});
            skLineSegment(sketch, "E21.14.4.7", {"start": v(-197.83, 50.76) * mm, "end": v(-197.83, 51.36) * mm});
            skLineSegment(sketch, "E21.14.5.0", {"start": v(-193.83, 99.16) * mm, "end": v(-197.83, 99.16) * mm});
            skLineSegment(sketch, "E21.14.5.1", {"start": v(-193.83, 94.76) * mm, "end": v(-197.83, 94.76) * mm});
            skLineSegment(sketch, "E21.14.5.2", {"start": v(-193.83, 99.76) * mm, "end": v(-197.83, 99.76) * mm});
            skLineSegment(sketch, "E21.14.5.3", {"start": v(-193.83, 94.16) * mm, "end": v(-197.83, 94.16) * mm});
            skLineSegment(sketch, "E21.14.5.4", {"start": v(-193.83, 99.16) * mm, "end": v(-193.83, 99.76) * mm});
            skLineSegment(sketch, "E21.14.5.5", {"start": v(-193.83, 94.16) * mm, "end": v(-193.83, 94.76) * mm});
            skLineSegment(sketch, "E21.14.5.6", {"start": v(-197.83, 94.16) * mm, "end": v(-197.83, 94.76) * mm});
            skLineSegment(sketch, "E21.14.5.7", {"start": v(-197.83, 99.16) * mm, "end": v(-197.83, 99.76) * mm});
            skLineSegment(sketch, "E21.14.6.0", {"start": v(-193.83, 147.56) * mm, "end": v(-197.83, 147.56) * mm});
            skLineSegment(sketch, "E21.14.6.1", {"start": v(-193.83, 143.16) * mm, "end": v(-197.83, 143.16) * mm});
            skLineSegment(sketch, "E21.14.6.2", {"start": v(-193.83, 148.16) * mm, "end": v(-197.83, 148.16) * mm});
            skLineSegment(sketch, "E21.14.6.3", {"start": v(-193.83, 142.56) * mm, "end": v(-197.83, 142.56) * mm});
            skLineSegment(sketch, "E21.14.6.4", {"start": v(-193.83, 147.56) * mm, "end": v(-193.83, 148.16) * mm});
            skLineSegment(sketch, "E21.14.6.5", {"start": v(-193.83, 142.56) * mm, "end": v(-193.83, 143.16) * mm});
            skLineSegment(sketch, "E21.14.6.6", {"start": v(-197.83, 142.56) * mm, "end": v(-197.83, 143.16) * mm});
            skLineSegment(sketch, "E21.14.6.7", {"start": v(-197.83, 147.56) * mm, "end": v(-197.83, 148.16) * mm});
            skLineSegment(sketch, "E21.direction1", {"start": v(194.17, -147.84) * mm, "end": v(166.17, -147.84) * mm, "construction": true});
            skLineSegment(sketch, "E21.direction2", {"start": v(194.17, -147.84) * mm, "end": v(194.17, -99.44) * mm, "construction": true});
            skLineSegment(sketch, "E22.0.1.0", {"start": v(184.15, -75.1) * mm, "end": v(180.15, -75.1) * mm});
            skLineSegment(sketch, "E22.0.1.1", {"start": v(184.15, -69.5) * mm, "end": v(180.15, -69.5) * mm});
            skLineSegment(sketch, "E22.0.1.2", {"start": v(184.15, -74.5) * mm, "end": v(180.15, -74.5) * mm});
            skLineSegment(sketch, "E22.0.1.3", {"start": v(184.15, -70.1) * mm, "end": v(180.15, -70.1) * mm});
            skLineSegment(sketch, "E22.0.1.4", {"start": v(184.15, -70.1) * mm, "end": v(184.15, -69.5) * mm});
            skLineSegment(sketch, "E22.0.1.5", {"start": v(184.15, -75.1) * mm, "end": v(184.15, -74.5) * mm});
            skLineSegment(sketch, "E22.0.1.6", {"start": v(180.15, -75.1) * mm, "end": v(180.15, -74.5) * mm});
            skLineSegment(sketch, "E22.0.1.7", {"start": v(180.15, -70.1) * mm, "end": v(180.15, -69.5) * mm});
            skLineSegment(sketch, "E22.0.2.0", {"start": v(184.15, -26.7) * mm, "end": v(180.15, -26.7) * mm});
            skLineSegment(sketch, "E22.0.2.1", {"start": v(184.15, -21.1) * mm, "end": v(180.15, -21.1) * mm});
            skLineSegment(sketch, "E22.0.2.2", {"start": v(184.15, -26.1) * mm, "end": v(180.15, -26.1) * mm});
            skLineSegment(sketch, "E22.0.2.3", {"start": v(184.15, -21.7) * mm, "end": v(180.15, -21.7) * mm});
            skLineSegment(sketch, "E22.0.2.4", {"start": v(184.15, -21.7) * mm, "end": v(184.15, -21.1) * mm});
            skLineSegment(sketch, "E22.0.2.5", {"start": v(184.15, -26.7) * mm, "end": v(184.15, -26.1) * mm});
            skLineSegment(sketch, "E22.0.2.6", {"start": v(180.15, -26.7) * mm, "end": v(180.15, -26.1) * mm});
            skLineSegment(sketch, "E22.0.2.7", {"start": v(180.15, -21.7) * mm, "end": v(180.15, -21.1) * mm});
            skLineSegment(sketch, "E22.0.3.0", {"start": v(184.15, 21.7) * mm, "end": v(180.15, 21.7) * mm});
            skLineSegment(sketch, "E22.0.3.1", {"start": v(184.15, 27.3) * mm, "end": v(180.15, 27.3) * mm});
            skLineSegment(sketch, "E22.0.3.2", {"start": v(184.15, 22.3) * mm, "end": v(180.15, 22.3) * mm});
            skLineSegment(sketch, "E22.0.3.3", {"start": v(184.15, 26.7) * mm, "end": v(180.15, 26.7) * mm});
            skLineSegment(sketch, "E22.0.3.4", {"start": v(184.15, 26.7) * mm, "end": v(184.15, 27.3) * mm});
            skLineSegment(sketch, "E22.0.3.5", {"start": v(184.15, 21.7) * mm, "end": v(184.15, 22.3) * mm});
            skLineSegment(sketch, "E22.0.3.6", {"start": v(180.15, 21.7) * mm, "end": v(180.15, 22.3) * mm});
            skLineSegment(sketch, "E22.0.3.7", {"start": v(180.15, 26.7) * mm, "end": v(180.15, 27.3) * mm});
            skLineSegment(sketch, "E22.0.4.0", {"start": v(184.15, 70.1) * mm, "end": v(180.15, 70.1) * mm});
            skLineSegment(sketch, "E22.0.4.1", {"start": v(184.15, 75.7) * mm, "end": v(180.15, 75.7) * mm});
            skLineSegment(sketch, "E22.0.4.2", {"start": v(184.15, 70.7) * mm, "end": v(180.15, 70.7) * mm});
            skLineSegment(sketch, "E22.0.4.3", {"start": v(184.15, 75.1) * mm, "end": v(180.15, 75.1) * mm});
            skLineSegment(sketch, "E22.0.4.4", {"start": v(184.15, 75.1) * mm, "end": v(184.15, 75.7) * mm});
            skLineSegment(sketch, "E22.0.4.5", {"start": v(184.15, 70.1) * mm, "end": v(184.15, 70.7) * mm});
            skLineSegment(sketch, "E22.0.4.6", {"start": v(180.15, 70.1) * mm, "end": v(180.15, 70.7) * mm});
            skLineSegment(sketch, "E22.0.4.7", {"start": v(180.15, 75.1) * mm, "end": v(180.15, 75.7) * mm});
            skLineSegment(sketch, "E22.0.5.0", {"start": v(184.15, 118.5) * mm, "end": v(180.15, 118.5) * mm});
            skLineSegment(sketch, "E22.0.5.1", {"start": v(184.15, 124.1) * mm, "end": v(180.15, 124.1) * mm});
            skLineSegment(sketch, "E22.0.5.2", {"start": v(184.15, 119.1) * mm, "end": v(180.15, 119.1) * mm});
            skLineSegment(sketch, "E22.0.5.3", {"start": v(184.15, 123.5) * mm, "end": v(180.15, 123.5) * mm});
            skLineSegment(sketch, "E22.0.5.4", {"start": v(184.15, 123.5) * mm, "end": v(184.15, 124.1) * mm});
            skLineSegment(sketch, "E22.0.5.5", {"start": v(184.15, 118.5) * mm, "end": v(184.15, 119.1) * mm});
            skLineSegment(sketch, "E22.0.5.6", {"start": v(180.15, 118.5) * mm, "end": v(180.15, 119.1) * mm});
            skLineSegment(sketch, "E22.0.5.7", {"start": v(180.15, 123.5) * mm, "end": v(180.15, 124.1) * mm});
            skLineSegment(sketch, "E22.1.0.0", {"start": v(156.15, -123.5) * mm, "end": v(152.15, -123.5) * mm});
            skLineSegment(sketch, "E22.1.0.1", {"start": v(156.15, -117.9) * mm, "end": v(152.15, -117.9) * mm});
            skLineSegment(sketch, "E22.1.0.2", {"start": v(156.15, -122.9) * mm, "end": v(152.15, -122.9) * mm});
            skLineSegment(sketch, "E22.1.0.3", {"start": v(156.15, -118.5) * mm, "end": v(152.15, -118.5) * mm});
            skLineSegment(sketch, "E22.1.0.4", {"start": v(156.15, -118.5) * mm, "end": v(156.15, -117.9) * mm});
            skLineSegment(sketch, "E22.1.0.5", {"start": v(156.15, -123.5) * mm, "end": v(156.15, -122.9) * mm});
            skLineSegment(sketch, "E22.1.0.6", {"start": v(152.15, -123.5) * mm, "end": v(152.15, -122.9) * mm});
            skLineSegment(sketch, "E22.1.0.7", {"start": v(152.15, -118.5) * mm, "end": v(152.15, -117.9) * mm});
            skLineSegment(sketch, "E22.1.1.0", {"start": v(156.15, -75.1) * mm, "end": v(152.15, -75.1) * mm});
            skLineSegment(sketch, "E22.1.1.1", {"start": v(156.15, -69.5) * mm, "end": v(152.15, -69.5) * mm});
            skLineSegment(sketch, "E22.1.1.2", {"start": v(156.15, -74.5) * mm, "end": v(152.15, -74.5) * mm});
            skLineSegment(sketch, "E22.1.1.3", {"start": v(156.15, -70.1) * mm, "end": v(152.15, -70.1) * mm});
            skLineSegment(sketch, "E22.1.1.4", {"start": v(156.15, -70.1) * mm, "end": v(156.15, -69.5) * mm});
            skLineSegment(sketch, "E22.1.1.5", {"start": v(156.15, -75.1) * mm, "end": v(156.15, -74.5) * mm});
            skLineSegment(sketch, "E22.1.1.6", {"start": v(152.15, -75.1) * mm, "end": v(152.15, -74.5) * mm});
            skLineSegment(sketch, "E22.1.1.7", {"start": v(152.15, -70.1) * mm, "end": v(152.15, -69.5) * mm});
            skLineSegment(sketch, "E22.1.2.0", {"start": v(156.15, -26.7) * mm, "end": v(152.15, -26.7) * mm});
            skLineSegment(sketch, "E22.1.2.1", {"start": v(156.15, -21.1) * mm, "end": v(152.15, -21.1) * mm});
            skLineSegment(sketch, "E22.1.2.2", {"start": v(156.15, -26.1) * mm, "end": v(152.15, -26.1) * mm});
            skLineSegment(sketch, "E22.1.2.3", {"start": v(156.15, -21.7) * mm, "end": v(152.15, -21.7) * mm});
            skLineSegment(sketch, "E22.1.2.4", {"start": v(156.15, -21.7) * mm, "end": v(156.15, -21.1) * mm});
            skLineSegment(sketch, "E22.1.2.5", {"start": v(156.15, -26.7) * mm, "end": v(156.15, -26.1) * mm});
            skLineSegment(sketch, "E22.1.2.6", {"start": v(152.15, -26.7) * mm, "end": v(152.15, -26.1) * mm});
            skLineSegment(sketch, "E22.1.2.7", {"start": v(152.15, -21.7) * mm, "end": v(152.15, -21.1) * mm});
            skLineSegment(sketch, "E22.1.3.0", {"start": v(156.15, 21.7) * mm, "end": v(152.15, 21.7) * mm});
            skLineSegment(sketch, "E22.1.3.1", {"start": v(156.15, 27.3) * mm, "end": v(152.15, 27.3) * mm});
            skLineSegment(sketch, "E22.1.3.2", {"start": v(156.15, 22.3) * mm, "end": v(152.15, 22.3) * mm});
            skLineSegment(sketch, "E22.1.3.3", {"start": v(156.15, 26.7) * mm, "end": v(152.15, 26.7) * mm});
            skLineSegment(sketch, "E22.1.3.4", {"start": v(156.15, 26.7) * mm, "end": v(156.15, 27.3) * mm});
            skLineSegment(sketch, "E22.1.3.5", {"start": v(156.15, 21.7) * mm, "end": v(156.15, 22.3) * mm});
            skLineSegment(sketch, "E22.1.3.6", {"start": v(152.15, 21.7) * mm, "end": v(152.15, 22.3) * mm});
            skLineSegment(sketch, "E22.1.3.7", {"start": v(152.15, 26.7) * mm, "end": v(152.15, 27.3) * mm});
            skLineSegment(sketch, "E22.1.4.0", {"start": v(156.15, 70.1) * mm, "end": v(152.15, 70.1) * mm});
            skLineSegment(sketch, "E22.1.4.1", {"start": v(156.15, 75.7) * mm, "end": v(152.15, 75.7) * mm});
            skLineSegment(sketch, "E22.1.4.2", {"start": v(156.15, 70.7) * mm, "end": v(152.15, 70.7) * mm});
            skLineSegment(sketch, "E22.1.4.3", {"start": v(156.15, 75.1) * mm, "end": v(152.15, 75.1) * mm});
            skLineSegment(sketch, "E22.1.4.4", {"start": v(156.15, 75.1) * mm, "end": v(156.15, 75.7) * mm});
            skLineSegment(sketch, "E22.1.4.5", {"start": v(156.15, 70.1) * mm, "end": v(156.15, 70.7) * mm});
            skLineSegment(sketch, "E22.1.4.6", {"start": v(152.15, 70.1) * mm, "end": v(152.15, 70.7) * mm});
            skLineSegment(sketch, "E22.1.4.7", {"start": v(152.15, 75.1) * mm, "end": v(152.15, 75.7) * mm});
            skLineSegment(sketch, "E22.1.5.0", {"start": v(156.15, 118.5) * mm, "end": v(152.15, 118.5) * mm});
            skLineSegment(sketch, "E22.1.5.1", {"start": v(156.15, 124.1) * mm, "end": v(152.15, 124.1) * mm});
            skLineSegment(sketch, "E22.1.5.2", {"start": v(156.15, 119.1) * mm, "end": v(152.15, 119.1) * mm});
            skLineSegment(sketch, "E22.1.5.3", {"start": v(156.15, 123.5) * mm, "end": v(152.15, 123.5) * mm});
            skLineSegment(sketch, "E22.1.5.4", {"start": v(156.15, 123.5) * mm, "end": v(156.15, 124.1) * mm});
            skLineSegment(sketch, "E22.1.5.5", {"start": v(156.15, 118.5) * mm, "end": v(156.15, 119.1) * mm});
            skLineSegment(sketch, "E22.1.5.6", {"start": v(152.15, 118.5) * mm, "end": v(152.15, 119.1) * mm});
            skLineSegment(sketch, "E22.1.5.7", {"start": v(152.15, 123.5) * mm, "end": v(152.15, 124.1) * mm});
            skLineSegment(sketch, "E22.2.0.0", {"start": v(128.15, -123.5) * mm, "end": v(124.15, -123.5) * mm});
            skLineSegment(sketch, "E22.2.0.1", {"start": v(128.15, -117.9) * mm, "end": v(124.15, -117.9) * mm});
            skLineSegment(sketch, "E22.2.0.2", {"start": v(128.15, -122.9) * mm, "end": v(124.15, -122.9) * mm});
            skLineSegment(sketch, "E22.2.0.3", {"start": v(128.15, -118.5) * mm, "end": v(124.15, -118.5) * mm});
            skLineSegment(sketch, "E22.2.0.4", {"start": v(128.15, -118.5) * mm, "end": v(128.15, -117.9) * mm});
            skLineSegment(sketch, "E22.2.0.5", {"start": v(128.15, -123.5) * mm, "end": v(128.15, -122.9) * mm});
            skLineSegment(sketch, "E22.2.0.6", {"start": v(124.15, -123.5) * mm, "end": v(124.15, -122.9) * mm});
            skLineSegment(sketch, "E22.2.0.7", {"start": v(124.15, -118.5) * mm, "end": v(124.15, -117.9) * mm});
            skLineSegment(sketch, "E22.2.1.0", {"start": v(128.15, -75.1) * mm, "end": v(124.15, -75.1) * mm});
            skLineSegment(sketch, "E22.2.1.1", {"start": v(128.15, -69.5) * mm, "end": v(124.15, -69.5) * mm});
            skLineSegment(sketch, "E22.2.1.2", {"start": v(128.15, -74.5) * mm, "end": v(124.15, -74.5) * mm});
            skLineSegment(sketch, "E22.2.1.3", {"start": v(128.15, -70.1) * mm, "end": v(124.15, -70.1) * mm});
            skLineSegment(sketch, "E22.2.1.4", {"start": v(128.15, -70.1) * mm, "end": v(128.15, -69.5) * mm});
            skLineSegment(sketch, "E22.2.1.5", {"start": v(128.15, -75.1) * mm, "end": v(128.15, -74.5) * mm});
            skLineSegment(sketch, "E22.2.1.6", {"start": v(124.15, -75.1) * mm, "end": v(124.15, -74.5) * mm});
            skLineSegment(sketch, "E22.2.1.7", {"start": v(124.15, -70.1) * mm, "end": v(124.15, -69.5) * mm});
            skLineSegment(sketch, "E22.2.2.0", {"start": v(128.15, -26.7) * mm, "end": v(124.15, -26.7) * mm});
            skLineSegment(sketch, "E22.2.2.1", {"start": v(128.15, -21.1) * mm, "end": v(124.15, -21.1) * mm});
            skLineSegment(sketch, "E22.2.2.2", {"start": v(128.15, -26.1) * mm, "end": v(124.15, -26.1) * mm});
            skLineSegment(sketch, "E22.2.2.3", {"start": v(128.15, -21.7) * mm, "end": v(124.15, -21.7) * mm});
            skLineSegment(sketch, "E22.2.2.4", {"start": v(128.15, -21.7) * mm, "end": v(128.15, -21.1) * mm});
            skLineSegment(sketch, "E22.2.2.5", {"start": v(128.15, -26.7) * mm, "end": v(128.15, -26.1) * mm});
            skLineSegment(sketch, "E22.2.2.6", {"start": v(124.15, -26.7) * mm, "end": v(124.15, -26.1) * mm});
            skLineSegment(sketch, "E22.2.2.7", {"start": v(124.15, -21.7) * mm, "end": v(124.15, -21.1) * mm});
            skLineSegment(sketch, "E22.2.3.0", {"start": v(128.15, 21.7) * mm, "end": v(124.15, 21.7) * mm});
            skLineSegment(sketch, "E22.2.3.1", {"start": v(128.15, 27.3) * mm, "end": v(124.15, 27.3) * mm});
            skLineSegment(sketch, "E22.2.3.2", {"start": v(128.15, 22.3) * mm, "end": v(124.15, 22.3) * mm});
            skLineSegment(sketch, "E22.2.3.3", {"start": v(128.15, 26.7) * mm, "end": v(124.15, 26.7) * mm});
            skLineSegment(sketch, "E22.2.3.4", {"start": v(128.15, 26.7) * mm, "end": v(128.15, 27.3) * mm});
            skLineSegment(sketch, "E22.2.3.5", {"start": v(128.15, 21.7) * mm, "end": v(128.15, 22.3) * mm});
            skLineSegment(sketch, "E22.2.3.6", {"start": v(124.15, 21.7) * mm, "end": v(124.15, 22.3) * mm});
            skLineSegment(sketch, "E22.2.3.7", {"start": v(124.15, 26.7) * mm, "end": v(124.15, 27.3) * mm});
            skLineSegment(sketch, "E22.2.4.0", {"start": v(128.15, 70.1) * mm, "end": v(124.15, 70.1) * mm});
            skLineSegment(sketch, "E22.2.4.1", {"start": v(128.15, 75.7) * mm, "end": v(124.15, 75.7) * mm});
            skLineSegment(sketch, "E22.2.4.2", {"start": v(128.15, 70.7) * mm, "end": v(124.15, 70.7) * mm});
            skLineSegment(sketch, "E22.2.4.3", {"start": v(128.15, 75.1) * mm, "end": v(124.15, 75.1) * mm});
            skLineSegment(sketch, "E22.2.4.4", {"start": v(128.15, 75.1) * mm, "end": v(128.15, 75.7) * mm});
            skLineSegment(sketch, "E22.2.4.5", {"start": v(128.15, 70.1) * mm, "end": v(128.15, 70.7) * mm});
            skLineSegment(sketch, "E22.2.4.6", {"start": v(124.15, 70.1) * mm, "end": v(124.15, 70.7) * mm});
            skLineSegment(sketch, "E22.2.4.7", {"start": v(124.15, 75.1) * mm, "end": v(124.15, 75.7) * mm});
            skLineSegment(sketch, "E22.2.5.0", {"start": v(128.15, 118.5) * mm, "end": v(124.15, 118.5) * mm});
            skLineSegment(sketch, "E22.2.5.1", {"start": v(128.15, 124.1) * mm, "end": v(124.15, 124.1) * mm});
            skLineSegment(sketch, "E22.2.5.2", {"start": v(128.15, 119.1) * mm, "end": v(124.15, 119.1) * mm});
            skLineSegment(sketch, "E22.2.5.3", {"start": v(128.15, 123.5) * mm, "end": v(124.15, 123.5) * mm});
            skLineSegment(sketch, "E22.2.5.4", {"start": v(128.15, 123.5) * mm, "end": v(128.15, 124.1) * mm});
            skLineSegment(sketch, "E22.2.5.5", {"start": v(128.15, 118.5) * mm, "end": v(128.15, 119.1) * mm});
            skLineSegment(sketch, "E22.2.5.6", {"start": v(124.15, 118.5) * mm, "end": v(124.15, 119.1) * mm});
            skLineSegment(sketch, "E22.2.5.7", {"start": v(124.15, 123.5) * mm, "end": v(124.15, 124.1) * mm});
            skLineSegment(sketch, "E22.3.0.0", {"start": v(100.15, -123.5) * mm, "end": v(96.15, -123.5) * mm});
            skLineSegment(sketch, "E22.3.0.1", {"start": v(100.15, -117.9) * mm, "end": v(96.15, -117.9) * mm});
            skLineSegment(sketch, "E22.3.0.2", {"start": v(100.15, -122.9) * mm, "end": v(96.15, -122.9) * mm});
            skLineSegment(sketch, "E22.3.0.3", {"start": v(100.15, -118.5) * mm, "end": v(96.15, -118.5) * mm});
            skLineSegment(sketch, "E22.3.0.4", {"start": v(100.15, -118.5) * mm, "end": v(100.15, -117.9) * mm});
            skLineSegment(sketch, "E22.3.0.5", {"start": v(100.15, -123.5) * mm, "end": v(100.15, -122.9) * mm});
            skLineSegment(sketch, "E22.3.0.6", {"start": v(96.15, -123.5) * mm, "end": v(96.15, -122.9) * mm});
            skLineSegment(sketch, "E22.3.0.7", {"start": v(96.15, -118.5) * mm, "end": v(96.15, -117.9) * mm});
            skLineSegment(sketch, "E22.3.1.0", {"start": v(100.15, -75.1) * mm, "end": v(96.15, -75.1) * mm});
            skLineSegment(sketch, "E22.3.1.1", {"start": v(100.15, -69.5) * mm, "end": v(96.15, -69.5) * mm});
            skLineSegment(sketch, "E22.3.1.2", {"start": v(100.15, -74.5) * mm, "end": v(96.15, -74.5) * mm});
            skLineSegment(sketch, "E22.3.1.3", {"start": v(100.15, -70.1) * mm, "end": v(96.15, -70.1) * mm});
            skLineSegment(sketch, "E22.3.1.4", {"start": v(100.15, -70.1) * mm, "end": v(100.15, -69.5) * mm});
            skLineSegment(sketch, "E22.3.1.5", {"start": v(100.15, -75.1) * mm, "end": v(100.15, -74.5) * mm});
            skLineSegment(sketch, "E22.3.1.6", {"start": v(96.15, -75.1) * mm, "end": v(96.15, -74.5) * mm});
            skLineSegment(sketch, "E22.3.1.7", {"start": v(96.15, -70.1) * mm, "end": v(96.15, -69.5) * mm});
            skLineSegment(sketch, "E22.3.2.0", {"start": v(100.15, -26.7) * mm, "end": v(96.15, -26.7) * mm});
            skLineSegment(sketch, "E22.3.2.1", {"start": v(100.15, -21.1) * mm, "end": v(96.15, -21.1) * mm});
            skLineSegment(sketch, "E22.3.2.2", {"start": v(100.15, -26.1) * mm, "end": v(96.15, -26.1) * mm});
            skLineSegment(sketch, "E22.3.2.3", {"start": v(100.15, -21.7) * mm, "end": v(96.15, -21.7) * mm});
            skLineSegment(sketch, "E22.3.2.4", {"start": v(100.15, -21.7) * mm, "end": v(100.15, -21.1) * mm});
            skLineSegment(sketch, "E22.3.2.5", {"start": v(100.15, -26.7) * mm, "end": v(100.15, -26.1) * mm});
            skLineSegment(sketch, "E22.3.2.6", {"start": v(96.15, -26.7) * mm, "end": v(96.15, -26.1) * mm});
            skLineSegment(sketch, "E22.3.2.7", {"start": v(96.15, -21.7) * mm, "end": v(96.15, -21.1) * mm});
            skLineSegment(sketch, "E22.3.3.0", {"start": v(100.15, 21.7) * mm, "end": v(96.15, 21.7) * mm});
            skLineSegment(sketch, "E22.3.3.1", {"start": v(100.15, 27.3) * mm, "end": v(96.15, 27.3) * mm});
            skLineSegment(sketch, "E22.3.3.2", {"start": v(100.15, 22.3) * mm, "end": v(96.15, 22.3) * mm});
            skLineSegment(sketch, "E22.3.3.3", {"start": v(100.15, 26.7) * mm, "end": v(96.15, 26.7) * mm});
            skLineSegment(sketch, "E22.3.3.4", {"start": v(100.15, 26.7) * mm, "end": v(100.15, 27.3) * mm});
            skLineSegment(sketch, "E22.3.3.5", {"start": v(100.15, 21.7) * mm, "end": v(100.15, 22.3) * mm});
            skLineSegment(sketch, "E22.3.3.6", {"start": v(96.15, 21.7) * mm, "end": v(96.15, 22.3) * mm});
            skLineSegment(sketch, "E22.3.3.7", {"start": v(96.15, 26.7) * mm, "end": v(96.15, 27.3) * mm});
            skLineSegment(sketch, "E22.3.4.0", {"start": v(100.15, 70.1) * mm, "end": v(96.15, 70.1) * mm});
            skLineSegment(sketch, "E22.3.4.1", {"start": v(100.15, 75.7) * mm, "end": v(96.15, 75.7) * mm});
            skLineSegment(sketch, "E22.3.4.2", {"start": v(100.15, 70.7) * mm, "end": v(96.15, 70.7) * mm});
            skLineSegment(sketch, "E22.3.4.3", {"start": v(100.15, 75.1) * mm, "end": v(96.15, 75.1) * mm});
            skLineSegment(sketch, "E22.3.4.4", {"start": v(100.15, 75.1) * mm, "end": v(100.15, 75.7) * mm});
            skLineSegment(sketch, "E22.3.4.5", {"start": v(100.15, 70.1) * mm, "end": v(100.15, 70.7) * mm});
            skLineSegment(sketch, "E22.3.4.6", {"start": v(96.15, 70.1) * mm, "end": v(96.15, 70.7) * mm});
            skLineSegment(sketch, "E22.3.4.7", {"start": v(96.15, 75.1) * mm, "end": v(96.15, 75.7) * mm});
            skLineSegment(sketch, "E22.3.5.0", {"start": v(100.15, 118.5) * mm, "end": v(96.15, 118.5) * mm});
            skLineSegment(sketch, "E22.3.5.1", {"start": v(100.15, 124.1) * mm, "end": v(96.15, 124.1) * mm});
            skLineSegment(sketch, "E22.3.5.2", {"start": v(100.15, 119.1) * mm, "end": v(96.15, 119.1) * mm});
            skLineSegment(sketch, "E22.3.5.3", {"start": v(100.15, 123.5) * mm, "end": v(96.15, 123.5) * mm});
            skLineSegment(sketch, "E22.3.5.4", {"start": v(100.15, 123.5) * mm, "end": v(100.15, 124.1) * mm});
            skLineSegment(sketch, "E22.3.5.5", {"start": v(100.15, 118.5) * mm, "end": v(100.15, 119.1) * mm});
            skLineSegment(sketch, "E22.3.5.6", {"start": v(96.15, 118.5) * mm, "end": v(96.15, 119.1) * mm});
            skLineSegment(sketch, "E22.3.5.7", {"start": v(96.15, 123.5) * mm, "end": v(96.15, 124.1) * mm});
            skLineSegment(sketch, "E22.4.0.0", {"start": v(72.15, -123.5) * mm, "end": v(68.15, -123.5) * mm});
            skLineSegment(sketch, "E22.4.0.1", {"start": v(72.15, -117.9) * mm, "end": v(68.15, -117.9) * mm});
            skLineSegment(sketch, "E22.4.0.2", {"start": v(72.15, -122.9) * mm, "end": v(68.15, -122.9) * mm});
            skLineSegment(sketch, "E22.4.0.3", {"start": v(72.15, -118.5) * mm, "end": v(68.15, -118.5) * mm});
            skLineSegment(sketch, "E22.4.0.4", {"start": v(72.15, -118.5) * mm, "end": v(72.15, -117.9) * mm});
            skLineSegment(sketch, "E22.4.0.5", {"start": v(72.15, -123.5) * mm, "end": v(72.15, -122.9) * mm});
            skLineSegment(sketch, "E22.4.0.6", {"start": v(68.15, -123.5) * mm, "end": v(68.15, -122.9) * mm});
            skLineSegment(sketch, "E22.4.0.7", {"start": v(68.15, -118.5) * mm, "end": v(68.15, -117.9) * mm});
            skLineSegment(sketch, "E22.4.1.0", {"start": v(72.15, -75.1) * mm, "end": v(68.15, -75.1) * mm});
            skLineSegment(sketch, "E22.4.1.1", {"start": v(72.15, -69.5) * mm, "end": v(68.15, -69.5) * mm});
            skLineSegment(sketch, "E22.4.1.2", {"start": v(72.15, -74.5) * mm, "end": v(68.15, -74.5) * mm});
            skLineSegment(sketch, "E22.4.1.3", {"start": v(72.15, -70.1) * mm, "end": v(68.15, -70.1) * mm});
            skLineSegment(sketch, "E22.4.1.4", {"start": v(72.15, -70.1) * mm, "end": v(72.15, -69.5) * mm});
            skLineSegment(sketch, "E22.4.1.5", {"start": v(72.15, -75.1) * mm, "end": v(72.15, -74.5) * mm});
            skLineSegment(sketch, "E22.4.1.6", {"start": v(68.15, -75.1) * mm, "end": v(68.15, -74.5) * mm});
            skLineSegment(sketch, "E22.4.1.7", {"start": v(68.15, -70.1) * mm, "end": v(68.15, -69.5) * mm});
            skLineSegment(sketch, "E22.4.2.0", {"start": v(72.15, -26.7) * mm, "end": v(68.15, -26.7) * mm});
            skLineSegment(sketch, "E22.4.2.1", {"start": v(72.15, -21.1) * mm, "end": v(68.15, -21.1) * mm});
            skLineSegment(sketch, "E22.4.2.2", {"start": v(72.15, -26.1) * mm, "end": v(68.15, -26.1) * mm});
            skLineSegment(sketch, "E22.4.2.3", {"start": v(72.15, -21.7) * mm, "end": v(68.15, -21.7) * mm});
            skLineSegment(sketch, "E22.4.2.4", {"start": v(72.15, -21.7) * mm, "end": v(72.15, -21.1) * mm});
            skLineSegment(sketch, "E22.4.2.5", {"start": v(72.15, -26.7) * mm, "end": v(72.15, -26.1) * mm});
            skLineSegment(sketch, "E22.4.2.6", {"start": v(68.15, -26.7) * mm, "end": v(68.15, -26.1) * mm});
            skLineSegment(sketch, "E22.4.2.7", {"start": v(68.15, -21.7) * mm, "end": v(68.15, -21.1) * mm});
            skLineSegment(sketch, "E22.4.3.0", {"start": v(72.15, 21.7) * mm, "end": v(68.15, 21.7) * mm});
            skLineSegment(sketch, "E22.4.3.1", {"start": v(72.15, 27.3) * mm, "end": v(68.15, 27.3) * mm});
            skLineSegment(sketch, "E22.4.3.2", {"start": v(72.15, 22.3) * mm, "end": v(68.15, 22.3) * mm});
            skLineSegment(sketch, "E22.4.3.3", {"start": v(72.15, 26.7) * mm, "end": v(68.15, 26.7) * mm});
            skLineSegment(sketch, "E22.4.3.4", {"start": v(72.15, 26.7) * mm, "end": v(72.15, 27.3) * mm});
            skLineSegment(sketch, "E22.4.3.5", {"start": v(72.15, 21.7) * mm, "end": v(72.15, 22.3) * mm});
            skLineSegment(sketch, "E22.4.3.6", {"start": v(68.15, 21.7) * mm, "end": v(68.15, 22.3) * mm});
            skLineSegment(sketch, "E22.4.3.7", {"start": v(68.15, 26.7) * mm, "end": v(68.15, 27.3) * mm});
            skLineSegment(sketch, "E22.4.4.0", {"start": v(72.15, 70.1) * mm, "end": v(68.15, 70.1) * mm});
            skLineSegment(sketch, "E22.4.4.1", {"start": v(72.15, 75.7) * mm, "end": v(68.15, 75.7) * mm});
            skLineSegment(sketch, "E22.4.4.2", {"start": v(72.15, 70.7) * mm, "end": v(68.15, 70.7) * mm});
            skLineSegment(sketch, "E22.4.4.3", {"start": v(72.15, 75.1) * mm, "end": v(68.15, 75.1) * mm});
            skLineSegment(sketch, "E22.4.4.4", {"start": v(72.15, 75.1) * mm, "end": v(72.15, 75.7) * mm});
            skLineSegment(sketch, "E22.4.4.5", {"start": v(72.15, 70.1) * mm, "end": v(72.15, 70.7) * mm});
            skLineSegment(sketch, "E22.4.4.6", {"start": v(68.15, 70.1) * mm, "end": v(68.15, 70.7) * mm});
            skLineSegment(sketch, "E22.4.4.7", {"start": v(68.15, 75.1) * mm, "end": v(68.15, 75.7) * mm});
            skLineSegment(sketch, "E22.4.5.0", {"start": v(72.15, 118.5) * mm, "end": v(68.15, 118.5) * mm});
            skLineSegment(sketch, "E22.4.5.1", {"start": v(72.15, 124.1) * mm, "end": v(68.15, 124.1) * mm});
            skLineSegment(sketch, "E22.4.5.2", {"start": v(72.15, 119.1) * mm, "end": v(68.15, 119.1) * mm});
            skLineSegment(sketch, "E22.4.5.3", {"start": v(72.15, 123.5) * mm, "end": v(68.15, 123.5) * mm});
            skLineSegment(sketch, "E22.4.5.4", {"start": v(72.15, 123.5) * mm, "end": v(72.15, 124.1) * mm});
            skLineSegment(sketch, "E22.4.5.5", {"start": v(72.15, 118.5) * mm, "end": v(72.15, 119.1) * mm});
            skLineSegment(sketch, "E22.4.5.6", {"start": v(68.15, 118.5) * mm, "end": v(68.15, 119.1) * mm});
            skLineSegment(sketch, "E22.4.5.7", {"start": v(68.15, 123.5) * mm, "end": v(68.15, 124.1) * mm});
            skLineSegment(sketch, "E22.5.0.0", {"start": v(44.15, -123.5) * mm, "end": v(40.15, -123.5) * mm});
            skLineSegment(sketch, "E22.5.0.1", {"start": v(44.15, -117.9) * mm, "end": v(40.15, -117.9) * mm});
            skLineSegment(sketch, "E22.5.0.2", {"start": v(44.15, -122.9) * mm, "end": v(40.15, -122.9) * mm});
            skLineSegment(sketch, "E22.5.0.3", {"start": v(44.15, -118.5) * mm, "end": v(40.15, -118.5) * mm});
            skLineSegment(sketch, "E22.5.0.4", {"start": v(44.15, -118.5) * mm, "end": v(44.15, -117.9) * mm});
            skLineSegment(sketch, "E22.5.0.5", {"start": v(44.15, -123.5) * mm, "end": v(44.15, -122.9) * mm});
            skLineSegment(sketch, "E22.5.0.6", {"start": v(40.15, -123.5) * mm, "end": v(40.15, -122.9) * mm});
            skLineSegment(sketch, "E22.5.0.7", {"start": v(40.15, -118.5) * mm, "end": v(40.15, -117.9) * mm});
            skLineSegment(sketch, "E22.5.1.0", {"start": v(44.15, -75.1) * mm, "end": v(40.15, -75.1) * mm});
            skLineSegment(sketch, "E22.5.1.1", {"start": v(44.15, -69.5) * mm, "end": v(40.15, -69.5) * mm});
            skLineSegment(sketch, "E22.5.1.2", {"start": v(44.15, -74.5) * mm, "end": v(40.15, -74.5) * mm});
            skLineSegment(sketch, "E22.5.1.3", {"start": v(44.15, -70.1) * mm, "end": v(40.15, -70.1) * mm});
            skLineSegment(sketch, "E22.5.1.4", {"start": v(44.15, -70.1) * mm, "end": v(44.15, -69.5) * mm});
            skLineSegment(sketch, "E22.5.1.5", {"start": v(44.15, -75.1) * mm, "end": v(44.15, -74.5) * mm});
            skLineSegment(sketch, "E22.5.1.6", {"start": v(40.15, -75.1) * mm, "end": v(40.15, -74.5) * mm});
            skLineSegment(sketch, "E22.5.1.7", {"start": v(40.15, -70.1) * mm, "end": v(40.15, -69.5) * mm});
            skLineSegment(sketch, "E22.5.2.0", {"start": v(44.15, -26.7) * mm, "end": v(40.15, -26.7) * mm});
            skLineSegment(sketch, "E22.5.2.1", {"start": v(44.15, -21.1) * mm, "end": v(40.15, -21.1) * mm});
            skLineSegment(sketch, "E22.5.2.2", {"start": v(44.15, -26.1) * mm, "end": v(40.15, -26.1) * mm});
            skLineSegment(sketch, "E22.5.2.3", {"start": v(44.15, -21.7) * mm, "end": v(40.15, -21.7) * mm});
            skLineSegment(sketch, "E22.5.2.4", {"start": v(44.15, -21.7) * mm, "end": v(44.15, -21.1) * mm});
            skLineSegment(sketch, "E22.5.2.5", {"start": v(44.15, -26.7) * mm, "end": v(44.15, -26.1) * mm});
            skLineSegment(sketch, "E22.5.2.6", {"start": v(40.15, -26.7) * mm, "end": v(40.15, -26.1) * mm});
            skLineSegment(sketch, "E22.5.2.7", {"start": v(40.15, -21.7) * mm, "end": v(40.15, -21.1) * mm});
            skLineSegment(sketch, "E22.5.3.0", {"start": v(44.15, 21.7) * mm, "end": v(40.15, 21.7) * mm});
            skLineSegment(sketch, "E22.5.3.1", {"start": v(44.15, 27.3) * mm, "end": v(40.15, 27.3) * mm});
            skLineSegment(sketch, "E22.5.3.2", {"start": v(44.15, 22.3) * mm, "end": v(40.15, 22.3) * mm});
            skLineSegment(sketch, "E22.5.3.3", {"start": v(44.15, 26.7) * mm, "end": v(40.15, 26.7) * mm});
            skLineSegment(sketch, "E22.5.3.4", {"start": v(44.15, 26.7) * mm, "end": v(44.15, 27.3) * mm});
            skLineSegment(sketch, "E22.5.3.5", {"start": v(44.15, 21.7) * mm, "end": v(44.15, 22.3) * mm});
            skLineSegment(sketch, "E22.5.3.6", {"start": v(40.15, 21.7) * mm, "end": v(40.15, 22.3) * mm});
            skLineSegment(sketch, "E22.5.3.7", {"start": v(40.15, 26.7) * mm, "end": v(40.15, 27.3) * mm});
            skLineSegment(sketch, "E22.5.4.0", {"start": v(44.15, 70.1) * mm, "end": v(40.15, 70.1) * mm});
            skLineSegment(sketch, "E22.5.4.1", {"start": v(44.15, 75.7) * mm, "end": v(40.15, 75.7) * mm});
            skLineSegment(sketch, "E22.5.4.2", {"start": v(44.15, 70.7) * mm, "end": v(40.15, 70.7) * mm});
            skLineSegment(sketch, "E22.5.4.3", {"start": v(44.15, 75.1) * mm, "end": v(40.15, 75.1) * mm});
            skLineSegment(sketch, "E22.5.4.4", {"start": v(44.15, 75.1) * mm, "end": v(44.15, 75.7) * mm});
            skLineSegment(sketch, "E22.5.4.5", {"start": v(44.15, 70.1) * mm, "end": v(44.15, 70.7) * mm});
            skLineSegment(sketch, "E22.5.4.6", {"start": v(40.15, 70.1) * mm, "end": v(40.15, 70.7) * mm});
            skLineSegment(sketch, "E22.5.4.7", {"start": v(40.15, 75.1) * mm, "end": v(40.15, 75.7) * mm});
            skLineSegment(sketch, "E22.5.5.0", {"start": v(44.15, 118.5) * mm, "end": v(40.15, 118.5) * mm});
            skLineSegment(sketch, "E22.5.5.1", {"start": v(44.15, 124.1) * mm, "end": v(40.15, 124.1) * mm});
            skLineSegment(sketch, "E22.5.5.2", {"start": v(44.15, 119.1) * mm, "end": v(40.15, 119.1) * mm});
            skLineSegment(sketch, "E22.5.5.3", {"start": v(44.15, 123.5) * mm, "end": v(40.15, 123.5) * mm});
            skLineSegment(sketch, "E22.5.5.4", {"start": v(44.15, 123.5) * mm, "end": v(44.15, 124.1) * mm});
            skLineSegment(sketch, "E22.5.5.5", {"start": v(44.15, 118.5) * mm, "end": v(44.15, 119.1) * mm});
            skLineSegment(sketch, "E22.5.5.6", {"start": v(40.15, 118.5) * mm, "end": v(40.15, 119.1) * mm});
            skLineSegment(sketch, "E22.5.5.7", {"start": v(40.15, 123.5) * mm, "end": v(40.15, 124.1) * mm});
            skLineSegment(sketch, "E22.6.0.0", {"start": v(16.15, -123.5) * mm, "end": v(12.15, -123.5) * mm});
            skLineSegment(sketch, "E22.6.0.1", {"start": v(16.15, -117.9) * mm, "end": v(12.15, -117.9) * mm});
            skLineSegment(sketch, "E22.6.0.2", {"start": v(16.15, -122.9) * mm, "end": v(12.15, -122.9) * mm});
            skLineSegment(sketch, "E22.6.0.3", {"start": v(16.15, -118.5) * mm, "end": v(12.15, -118.5) * mm});
            skLineSegment(sketch, "E22.6.0.4", {"start": v(16.15, -118.5) * mm, "end": v(16.15, -117.9) * mm});
            skLineSegment(sketch, "E22.6.0.5", {"start": v(16.15, -123.5) * mm, "end": v(16.15, -122.9) * mm});
            skLineSegment(sketch, "E22.6.0.6", {"start": v(12.15, -123.5) * mm, "end": v(12.15, -122.9) * mm});
            skLineSegment(sketch, "E22.6.0.7", {"start": v(12.15, -118.5) * mm, "end": v(12.15, -117.9) * mm});
            skLineSegment(sketch, "E22.6.1.0", {"start": v(16.15, -75.1) * mm, "end": v(12.15, -75.1) * mm});
            skLineSegment(sketch, "E22.6.1.1", {"start": v(16.15, -69.5) * mm, "end": v(12.15, -69.5) * mm});
            skLineSegment(sketch, "E22.6.1.2", {"start": v(16.15, -74.5) * mm, "end": v(12.15, -74.5) * mm});
            skLineSegment(sketch, "E22.6.1.3", {"start": v(16.15, -70.1) * mm, "end": v(12.15, -70.1) * mm});
            skLineSegment(sketch, "E22.6.1.4", {"start": v(16.15, -70.1) * mm, "end": v(16.15, -69.5) * mm});
            skLineSegment(sketch, "E22.6.1.5", {"start": v(16.15, -75.1) * mm, "end": v(16.15, -74.5) * mm});
            skLineSegment(sketch, "E22.6.1.6", {"start": v(12.15, -75.1) * mm, "end": v(12.15, -74.5) * mm});
            skLineSegment(sketch, "E22.6.1.7", {"start": v(12.15, -70.1) * mm, "end": v(12.15, -69.5) * mm});
            skLineSegment(sketch, "E22.6.2.0", {"start": v(16.15, -26.7) * mm, "end": v(12.15, -26.7) * mm});
            skLineSegment(sketch, "E22.6.2.1", {"start": v(16.15, -21.1) * mm, "end": v(12.15, -21.1) * mm});
            skLineSegment(sketch, "E22.6.2.2", {"start": v(16.15, -26.1) * mm, "end": v(12.15, -26.1) * mm});
            skLineSegment(sketch, "E22.6.2.3", {"start": v(16.15, -21.7) * mm, "end": v(12.15, -21.7) * mm});
            skLineSegment(sketch, "E22.6.2.4", {"start": v(16.15, -21.7) * mm, "end": v(16.15, -21.1) * mm});
            skLineSegment(sketch, "E22.6.2.5", {"start": v(16.15, -26.7) * mm, "end": v(16.15, -26.1) * mm});
            skLineSegment(sketch, "E22.6.2.6", {"start": v(12.15, -26.7) * mm, "end": v(12.15, -26.1) * mm});
            skLineSegment(sketch, "E22.6.2.7", {"start": v(12.15, -21.7) * mm, "end": v(12.15, -21.1) * mm});
            skLineSegment(sketch, "E22.6.3.0", {"start": v(16.15, 21.7) * mm, "end": v(12.15, 21.7) * mm});
            skLineSegment(sketch, "E22.6.3.1", {"start": v(16.15, 27.3) * mm, "end": v(12.15, 27.3) * mm});
            skLineSegment(sketch, "E22.6.3.2", {"start": v(16.15, 22.3) * mm, "end": v(12.15, 22.3) * mm});
            skLineSegment(sketch, "E22.6.3.3", {"start": v(16.15, 26.7) * mm, "end": v(12.15, 26.7) * mm});
            skLineSegment(sketch, "E22.6.3.4", {"start": v(16.15, 26.7) * mm, "end": v(16.15, 27.3) * mm});
            skLineSegment(sketch, "E22.6.3.5", {"start": v(16.15, 21.7) * mm, "end": v(16.15, 22.3) * mm});
            skLineSegment(sketch, "E22.6.3.6", {"start": v(12.15, 21.7) * mm, "end": v(12.15, 22.3) * mm});
            skLineSegment(sketch, "E22.6.3.7", {"start": v(12.15, 26.7) * mm, "end": v(12.15, 27.3) * mm});
            skLineSegment(sketch, "E22.6.4.0", {"start": v(16.15, 70.1) * mm, "end": v(12.15, 70.1) * mm});
            skLineSegment(sketch, "E22.6.4.1", {"start": v(16.15, 75.7) * mm, "end": v(12.15, 75.7) * mm});
            skLineSegment(sketch, "E22.6.4.2", {"start": v(16.15, 70.7) * mm, "end": v(12.15, 70.7) * mm});
            skLineSegment(sketch, "E22.6.4.3", {"start": v(16.15, 75.1) * mm, "end": v(12.15, 75.1) * mm});
            skLineSegment(sketch, "E22.6.4.4", {"start": v(16.15, 75.1) * mm, "end": v(16.15, 75.7) * mm});
            skLineSegment(sketch, "E22.6.4.5", {"start": v(16.15, 70.1) * mm, "end": v(16.15, 70.7) * mm});
            skLineSegment(sketch, "E22.6.4.6", {"start": v(12.15, 70.1) * mm, "end": v(12.15, 70.7) * mm});
            skLineSegment(sketch, "E22.6.4.7", {"start": v(12.15, 75.1) * mm, "end": v(12.15, 75.7) * mm});
            skLineSegment(sketch, "E22.6.5.0", {"start": v(16.15, 118.5) * mm, "end": v(12.15, 118.5) * mm});
            skLineSegment(sketch, "E22.6.5.1", {"start": v(16.15, 124.1) * mm, "end": v(12.15, 124.1) * mm});
            skLineSegment(sketch, "E22.6.5.2", {"start": v(16.15, 119.1) * mm, "end": v(12.15, 119.1) * mm});
            skLineSegment(sketch, "E22.6.5.3", {"start": v(16.15, 123.5) * mm, "end": v(12.15, 123.5) * mm});
            skLineSegment(sketch, "E22.6.5.4", {"start": v(16.15, 123.5) * mm, "end": v(16.15, 124.1) * mm});
            skLineSegment(sketch, "E22.6.5.5", {"start": v(16.15, 118.5) * mm, "end": v(16.15, 119.1) * mm});
            skLineSegment(sketch, "E22.6.5.6", {"start": v(12.15, 118.5) * mm, "end": v(12.15, 119.1) * mm});
            skLineSegment(sketch, "E22.6.5.7", {"start": v(12.15, 123.5) * mm, "end": v(12.15, 124.1) * mm});
            skLineSegment(sketch, "E22.7.0.0", {"start": v(-11.85, -123.5) * mm, "end": v(-15.85, -123.5) * mm});
            skLineSegment(sketch, "E22.7.0.1", {"start": v(-11.85, -117.9) * mm, "end": v(-15.85, -117.9) * mm});
            skLineSegment(sketch, "E22.7.0.2", {"start": v(-11.85, -122.9) * mm, "end": v(-15.85, -122.9) * mm});
            skLineSegment(sketch, "E22.7.0.3", {"start": v(-11.85, -118.5) * mm, "end": v(-15.85, -118.5) * mm});
            skLineSegment(sketch, "E22.7.0.4", {"start": v(-11.85, -118.5) * mm, "end": v(-11.85, -117.9) * mm});
            skLineSegment(sketch, "E22.7.0.5", {"start": v(-11.85, -123.5) * mm, "end": v(-11.85, -122.9) * mm});
            skLineSegment(sketch, "E22.7.0.6", {"start": v(-15.85, -123.5) * mm, "end": v(-15.85, -122.9) * mm});
            skLineSegment(sketch, "E22.7.0.7", {"start": v(-15.85, -118.5) * mm, "end": v(-15.85, -117.9) * mm});
            skLineSegment(sketch, "E22.7.1.0", {"start": v(-11.85, -75.1) * mm, "end": v(-15.85, -75.1) * mm});
            skLineSegment(sketch, "E22.7.1.1", {"start": v(-11.85, -69.5) * mm, "end": v(-15.85, -69.5) * mm});
            skLineSegment(sketch, "E22.7.1.2", {"start": v(-11.85, -74.5) * mm, "end": v(-15.85, -74.5) * mm});
            skLineSegment(sketch, "E22.7.1.3", {"start": v(-11.85, -70.1) * mm, "end": v(-15.85, -70.1) * mm});
            skLineSegment(sketch, "E22.7.1.4", {"start": v(-11.85, -70.1) * mm, "end": v(-11.85, -69.5) * mm});
            skLineSegment(sketch, "E22.7.1.5", {"start": v(-11.85, -75.1) * mm, "end": v(-11.85, -74.5) * mm});
            skLineSegment(sketch, "E22.7.1.6", {"start": v(-15.85, -75.1) * mm, "end": v(-15.85, -74.5) * mm});
            skLineSegment(sketch, "E22.7.1.7", {"start": v(-15.85, -70.1) * mm, "end": v(-15.85, -69.5) * mm});
            skLineSegment(sketch, "E22.7.2.0", {"start": v(-11.85, -26.7) * mm, "end": v(-15.85, -26.7) * mm});
            skLineSegment(sketch, "E22.7.2.1", {"start": v(-11.85, -21.1) * mm, "end": v(-15.85, -21.1) * mm});
            skLineSegment(sketch, "E22.7.2.2", {"start": v(-11.85, -26.1) * mm, "end": v(-15.85, -26.1) * mm});
            skLineSegment(sketch, "E22.7.2.3", {"start": v(-11.85, -21.7) * mm, "end": v(-15.85, -21.7) * mm});
            skLineSegment(sketch, "E22.7.2.4", {"start": v(-11.85, -21.7) * mm, "end": v(-11.85, -21.1) * mm});
            skLineSegment(sketch, "E22.7.2.5", {"start": v(-11.85, -26.7) * mm, "end": v(-11.85, -26.1) * mm});
            skLineSegment(sketch, "E22.7.2.6", {"start": v(-15.85, -26.7) * mm, "end": v(-15.85, -26.1) * mm});
            skLineSegment(sketch, "E22.7.2.7", {"start": v(-15.85, -21.7) * mm, "end": v(-15.85, -21.1) * mm});
            skLineSegment(sketch, "E22.7.3.0", {"start": v(-11.85, 21.7) * mm, "end": v(-15.85, 21.7) * mm});
            skLineSegment(sketch, "E22.7.3.1", {"start": v(-11.85, 27.3) * mm, "end": v(-15.85, 27.3) * mm});
            skLineSegment(sketch, "E22.7.3.2", {"start": v(-11.85, 22.3) * mm, "end": v(-15.85, 22.3) * mm});
            skLineSegment(sketch, "E22.7.3.3", {"start": v(-11.85, 26.7) * mm, "end": v(-15.85, 26.7) * mm});
            skLineSegment(sketch, "E22.7.3.4", {"start": v(-11.85, 26.7) * mm, "end": v(-11.85, 27.3) * mm});
            skLineSegment(sketch, "E22.7.3.5", {"start": v(-11.85, 21.7) * mm, "end": v(-11.85, 22.3) * mm});
            skLineSegment(sketch, "E22.7.3.6", {"start": v(-15.85, 21.7) * mm, "end": v(-15.85, 22.3) * mm});
            skLineSegment(sketch, "E22.7.3.7", {"start": v(-15.85, 26.7) * mm, "end": v(-15.85, 27.3) * mm});
            skLineSegment(sketch, "E22.7.4.0", {"start": v(-11.85, 70.1) * mm, "end": v(-15.85, 70.1) * mm});
            skLineSegment(sketch, "E22.7.4.1", {"start": v(-11.85, 75.7) * mm, "end": v(-15.85, 75.7) * mm});
            skLineSegment(sketch, "E22.7.4.2", {"start": v(-11.85, 70.7) * mm, "end": v(-15.85, 70.7) * mm});
            skLineSegment(sketch, "E22.7.4.3", {"start": v(-11.85, 75.1) * mm, "end": v(-15.85, 75.1) * mm});
            skLineSegment(sketch, "E22.7.4.4", {"start": v(-11.85, 75.1) * mm, "end": v(-11.85, 75.7) * mm});
            skLineSegment(sketch, "E22.7.4.5", {"start": v(-11.85, 70.1) * mm, "end": v(-11.85, 70.7) * mm});
            skLineSegment(sketch, "E22.7.4.6", {"start": v(-15.85, 70.1) * mm, "end": v(-15.85, 70.7) * mm});
            skLineSegment(sketch, "E22.7.4.7", {"start": v(-15.85, 75.1) * mm, "end": v(-15.85, 75.7) * mm});
            skLineSegment(sketch, "E22.7.5.0", {"start": v(-11.85, 118.5) * mm, "end": v(-15.85, 118.5) * mm});
            skLineSegment(sketch, "E22.7.5.1", {"start": v(-11.85, 124.1) * mm, "end": v(-15.85, 124.1) * mm});
            skLineSegment(sketch, "E22.7.5.2", {"start": v(-11.85, 119.1) * mm, "end": v(-15.85, 119.1) * mm});
            skLineSegment(sketch, "E22.7.5.3", {"start": v(-11.85, 123.5) * mm, "end": v(-15.85, 123.5) * mm});
            skLineSegment(sketch, "E22.7.5.4", {"start": v(-11.85, 123.5) * mm, "end": v(-11.85, 124.1) * mm});
            skLineSegment(sketch, "E22.7.5.5", {"start": v(-11.85, 118.5) * mm, "end": v(-11.85, 119.1) * mm});
            skLineSegment(sketch, "E22.7.5.6", {"start": v(-15.85, 118.5) * mm, "end": v(-15.85, 119.1) * mm});
            skLineSegment(sketch, "E22.7.5.7", {"start": v(-15.85, 123.5) * mm, "end": v(-15.85, 124.1) * mm});
            skLineSegment(sketch, "E22.8.0.0", {"start": v(-39.85, -123.5) * mm, "end": v(-43.85, -123.5) * mm});
            skLineSegment(sketch, "E22.8.0.1", {"start": v(-39.85, -117.9) * mm, "end": v(-43.85, -117.9) * mm});
            skLineSegment(sketch, "E22.8.0.2", {"start": v(-39.85, -122.9) * mm, "end": v(-43.85, -122.9) * mm});
            skLineSegment(sketch, "E22.8.0.3", {"start": v(-39.85, -118.5) * mm, "end": v(-43.85, -118.5) * mm});
            skLineSegment(sketch, "E22.8.0.4", {"start": v(-39.85, -118.5) * mm, "end": v(-39.85, -117.9) * mm});
            skLineSegment(sketch, "E22.8.0.5", {"start": v(-39.85, -123.5) * mm, "end": v(-39.85, -122.9) * mm});
            skLineSegment(sketch, "E22.8.0.6", {"start": v(-43.85, -123.5) * mm, "end": v(-43.85, -122.9) * mm});
            skLineSegment(sketch, "E22.8.0.7", {"start": v(-43.85, -118.5) * mm, "end": v(-43.85, -117.9) * mm});
            skLineSegment(sketch, "E22.8.1.0", {"start": v(-39.85, -75.1) * mm, "end": v(-43.85, -75.1) * mm});
            skLineSegment(sketch, "E22.8.1.1", {"start": v(-39.85, -69.5) * mm, "end": v(-43.85, -69.5) * mm});
            skLineSegment(sketch, "E22.8.1.2", {"start": v(-39.85, -74.5) * mm, "end": v(-43.85, -74.5) * mm});
            skLineSegment(sketch, "E22.8.1.3", {"start": v(-39.85, -70.1) * mm, "end": v(-43.85, -70.1) * mm});
            skLineSegment(sketch, "E22.8.1.4", {"start": v(-39.85, -70.1) * mm, "end": v(-39.85, -69.5) * mm});
            skLineSegment(sketch, "E22.8.1.5", {"start": v(-39.85, -75.1) * mm, "end": v(-39.85, -74.5) * mm});
            skLineSegment(sketch, "E22.8.1.6", {"start": v(-43.85, -75.1) * mm, "end": v(-43.85, -74.5) * mm});
            skLineSegment(sketch, "E22.8.1.7", {"start": v(-43.85, -70.1) * mm, "end": v(-43.85, -69.5) * mm});
            skLineSegment(sketch, "E22.8.2.0", {"start": v(-39.85, -26.7) * mm, "end": v(-43.85, -26.7) * mm});
            skLineSegment(sketch, "E22.8.2.1", {"start": v(-39.85, -21.1) * mm, "end": v(-43.85, -21.1) * mm});
            skLineSegment(sketch, "E22.8.2.2", {"start": v(-39.85, -26.1) * mm, "end": v(-43.85, -26.1) * mm});
            skLineSegment(sketch, "E22.8.2.3", {"start": v(-39.85, -21.7) * mm, "end": v(-43.85, -21.7) * mm});
            skLineSegment(sketch, "E22.8.2.4", {"start": v(-39.85, -21.7) * mm, "end": v(-39.85, -21.1) * mm});
            skLineSegment(sketch, "E22.8.2.5", {"start": v(-39.85, -26.7) * mm, "end": v(-39.85, -26.1) * mm});
            skLineSegment(sketch, "E22.8.2.6", {"start": v(-43.85, -26.7) * mm, "end": v(-43.85, -26.1) * mm});
            skLineSegment(sketch, "E22.8.2.7", {"start": v(-43.85, -21.7) * mm, "end": v(-43.85, -21.1) * mm});
            skLineSegment(sketch, "E22.8.3.0", {"start": v(-39.85, 21.7) * mm, "end": v(-43.85, 21.7) * mm});
            skLineSegment(sketch, "E22.8.3.1", {"start": v(-39.85, 27.3) * mm, "end": v(-43.85, 27.3) * mm});
            skLineSegment(sketch, "E22.8.3.2", {"start": v(-39.85, 22.3) * mm, "end": v(-43.85, 22.3) * mm});
            skLineSegment(sketch, "E22.8.3.3", {"start": v(-39.85, 26.7) * mm, "end": v(-43.85, 26.7) * mm});
            skLineSegment(sketch, "E22.8.3.4", {"start": v(-39.85, 26.7) * mm, "end": v(-39.85, 27.3) * mm});
            skLineSegment(sketch, "E22.8.3.5", {"start": v(-39.85, 21.7) * mm, "end": v(-39.85, 22.3) * mm});
            skLineSegment(sketch, "E22.8.3.6", {"start": v(-43.85, 21.7) * mm, "end": v(-43.85, 22.3) * mm});
            skLineSegment(sketch, "E22.8.3.7", {"start": v(-43.85, 26.7) * mm, "end": v(-43.85, 27.3) * mm});
            skLineSegment(sketch, "E22.8.4.0", {"start": v(-39.85, 70.1) * mm, "end": v(-43.85, 70.1) * mm});
            skLineSegment(sketch, "E22.8.4.1", {"start": v(-39.85, 75.7) * mm, "end": v(-43.85, 75.7) * mm});
            skLineSegment(sketch, "E22.8.4.2", {"start": v(-39.85, 70.7) * mm, "end": v(-43.85, 70.7) * mm});
            skLineSegment(sketch, "E22.8.4.3", {"start": v(-39.85, 75.1) * mm, "end": v(-43.85, 75.1) * mm});
            skLineSegment(sketch, "E22.8.4.4", {"start": v(-39.85, 75.1) * mm, "end": v(-39.85, 75.7) * mm});
            skLineSegment(sketch, "E22.8.4.5", {"start": v(-39.85, 70.1) * mm, "end": v(-39.85, 70.7) * mm});
            skLineSegment(sketch, "E22.8.4.6", {"start": v(-43.85, 70.1) * mm, "end": v(-43.85, 70.7) * mm});
            skLineSegment(sketch, "E22.8.4.7", {"start": v(-43.85, 75.1) * mm, "end": v(-43.85, 75.7) * mm});
            skLineSegment(sketch, "E22.8.5.0", {"start": v(-39.85, 118.5) * mm, "end": v(-43.85, 118.5) * mm});
            skLineSegment(sketch, "E22.8.5.1", {"start": v(-39.85, 124.1) * mm, "end": v(-43.85, 124.1) * mm});
            skLineSegment(sketch, "E22.8.5.2", {"start": v(-39.85, 119.1) * mm, "end": v(-43.85, 119.1) * mm});
            skLineSegment(sketch, "E22.8.5.3", {"start": v(-39.85, 123.5) * mm, "end": v(-43.85, 123.5) * mm});
            skLineSegment(sketch, "E22.8.5.4", {"start": v(-39.85, 123.5) * mm, "end": v(-39.85, 124.1) * mm});
            skLineSegment(sketch, "E22.8.5.5", {"start": v(-39.85, 118.5) * mm, "end": v(-39.85, 119.1) * mm});
            skLineSegment(sketch, "E22.8.5.6", {"start": v(-43.85, 118.5) * mm, "end": v(-43.85, 119.1) * mm});
            skLineSegment(sketch, "E22.8.5.7", {"start": v(-43.85, 123.5) * mm, "end": v(-43.85, 124.1) * mm});
            skLineSegment(sketch, "E22.9.0.0", {"start": v(-67.85, -123.5) * mm, "end": v(-71.85, -123.5) * mm});
            skLineSegment(sketch, "E22.9.0.1", {"start": v(-67.85, -117.9) * mm, "end": v(-71.85, -117.9) * mm});
            skLineSegment(sketch, "E22.9.0.2", {"start": v(-67.85, -122.9) * mm, "end": v(-71.85, -122.9) * mm});
            skLineSegment(sketch, "E22.9.0.3", {"start": v(-67.85, -118.5) * mm, "end": v(-71.85, -118.5) * mm});
            skLineSegment(sketch, "E22.9.0.4", {"start": v(-67.85, -118.5) * mm, "end": v(-67.85, -117.9) * mm});
            skLineSegment(sketch, "E22.9.0.5", {"start": v(-67.85, -123.5) * mm, "end": v(-67.85, -122.9) * mm});
            skLineSegment(sketch, "E22.9.0.6", {"start": v(-71.85, -123.5) * mm, "end": v(-71.85, -122.9) * mm});
            skLineSegment(sketch, "E22.9.0.7", {"start": v(-71.85, -118.5) * mm, "end": v(-71.85, -117.9) * mm});
            skLineSegment(sketch, "E22.9.1.0", {"start": v(-67.85, -75.1) * mm, "end": v(-71.85, -75.1) * mm});
            skLineSegment(sketch, "E22.9.1.1", {"start": v(-67.85, -69.5) * mm, "end": v(-71.85, -69.5) * mm});
            skLineSegment(sketch, "E22.9.1.2", {"start": v(-67.85, -74.5) * mm, "end": v(-71.85, -74.5) * mm});
            skLineSegment(sketch, "E22.9.1.3", {"start": v(-67.85, -70.1) * mm, "end": v(-71.85, -70.1) * mm});
            skLineSegment(sketch, "E22.9.1.4", {"start": v(-67.85, -70.1) * mm, "end": v(-67.85, -69.5) * mm});
            skLineSegment(sketch, "E22.9.1.5", {"start": v(-67.85, -75.1) * mm, "end": v(-67.85, -74.5) * mm});
            skLineSegment(sketch, "E22.9.1.6", {"start": v(-71.85, -75.1) * mm, "end": v(-71.85, -74.5) * mm});
            skLineSegment(sketch, "E22.9.1.7", {"start": v(-71.85, -70.1) * mm, "end": v(-71.85, -69.5) * mm});
            skLineSegment(sketch, "E22.9.2.0", {"start": v(-67.85, -26.7) * mm, "end": v(-71.85, -26.7) * mm});
            skLineSegment(sketch, "E22.9.2.1", {"start": v(-67.85, -21.1) * mm, "end": v(-71.85, -21.1) * mm});
            skLineSegment(sketch, "E22.9.2.2", {"start": v(-67.85, -26.1) * mm, "end": v(-71.85, -26.1) * mm});
            skLineSegment(sketch, "E22.9.2.3", {"start": v(-67.85, -21.7) * mm, "end": v(-71.85, -21.7) * mm});
            skLineSegment(sketch, "E22.9.2.4", {"start": v(-67.85, -21.7) * mm, "end": v(-67.85, -21.1) * mm});
            skLineSegment(sketch, "E22.9.2.5", {"start": v(-67.85, -26.7) * mm, "end": v(-67.85, -26.1) * mm});
            skLineSegment(sketch, "E22.9.2.6", {"start": v(-71.85, -26.7) * mm, "end": v(-71.85, -26.1) * mm});
            skLineSegment(sketch, "E22.9.2.7", {"start": v(-71.85, -21.7) * mm, "end": v(-71.85, -21.1) * mm});
            skLineSegment(sketch, "E22.9.3.0", {"start": v(-67.85, 21.7) * mm, "end": v(-71.85, 21.7) * mm});
            skLineSegment(sketch, "E22.9.3.1", {"start": v(-67.85, 27.3) * mm, "end": v(-71.85, 27.3) * mm});
            skLineSegment(sketch, "E22.9.3.2", {"start": v(-67.85, 22.3) * mm, "end": v(-71.85, 22.3) * mm});
            skLineSegment(sketch, "E22.9.3.3", {"start": v(-67.85, 26.7) * mm, "end": v(-71.85, 26.7) * mm});
            skLineSegment(sketch, "E22.9.3.4", {"start": v(-67.85, 26.7) * mm, "end": v(-67.85, 27.3) * mm});
            skLineSegment(sketch, "E22.9.3.5", {"start": v(-67.85, 21.7) * mm, "end": v(-67.85, 22.3) * mm});
            skLineSegment(sketch, "E22.9.3.6", {"start": v(-71.85, 21.7) * mm, "end": v(-71.85, 22.3) * mm});
            skLineSegment(sketch, "E22.9.3.7", {"start": v(-71.85, 26.7) * mm, "end": v(-71.85, 27.3) * mm});
            skLineSegment(sketch, "E22.9.4.0", {"start": v(-67.85, 70.1) * mm, "end": v(-71.85, 70.1) * mm});
            skLineSegment(sketch, "E22.9.4.1", {"start": v(-67.85, 75.7) * mm, "end": v(-71.85, 75.7) * mm});
            skLineSegment(sketch, "E22.9.4.2", {"start": v(-67.85, 70.7) * mm, "end": v(-71.85, 70.7) * mm});
            skLineSegment(sketch, "E22.9.4.3", {"start": v(-67.85, 75.1) * mm, "end": v(-71.85, 75.1) * mm});
            skLineSegment(sketch, "E22.9.4.4", {"start": v(-67.85, 75.1) * mm, "end": v(-67.85, 75.7) * mm});
            skLineSegment(sketch, "E22.9.4.5", {"start": v(-67.85, 70.1) * mm, "end": v(-67.85, 70.7) * mm});
            skLineSegment(sketch, "E22.9.4.6", {"start": v(-71.85, 70.1) * mm, "end": v(-71.85, 70.7) * mm});
            skLineSegment(sketch, "E22.9.4.7", {"start": v(-71.85, 75.1) * mm, "end": v(-71.85, 75.7) * mm});
            skLineSegment(sketch, "E22.9.5.0", {"start": v(-67.85, 118.5) * mm, "end": v(-71.85, 118.5) * mm});
            skLineSegment(sketch, "E22.9.5.1", {"start": v(-67.85, 124.1) * mm, "end": v(-71.85, 124.1) * mm});
            skLineSegment(sketch, "E22.9.5.2", {"start": v(-67.85, 119.1) * mm, "end": v(-71.85, 119.1) * mm});
            skLineSegment(sketch, "E22.9.5.3", {"start": v(-67.85, 123.5) * mm, "end": v(-71.85, 123.5) * mm});
            skLineSegment(sketch, "E22.9.5.4", {"start": v(-67.85, 123.5) * mm, "end": v(-67.85, 124.1) * mm});
            skLineSegment(sketch, "E22.9.5.5", {"start": v(-67.85, 118.5) * mm, "end": v(-67.85, 119.1) * mm});
            skLineSegment(sketch, "E22.9.5.6", {"start": v(-71.85, 118.5) * mm, "end": v(-71.85, 119.1) * mm});
            skLineSegment(sketch, "E22.9.5.7", {"start": v(-71.85, 123.5) * mm, "end": v(-71.85, 124.1) * mm});
            skLineSegment(sketch, "E22.10.0.0", {"start": v(-95.85, -123.5) * mm, "end": v(-99.85, -123.5) * mm});
            skLineSegment(sketch, "E22.10.0.1", {"start": v(-95.85, -117.9) * mm, "end": v(-99.85, -117.9) * mm});
            skLineSegment(sketch, "E22.10.0.2", {"start": v(-95.85, -122.9) * mm, "end": v(-99.85, -122.9) * mm});
            skLineSegment(sketch, "E22.10.0.3", {"start": v(-95.85, -118.5) * mm, "end": v(-99.85, -118.5) * mm});
            skLineSegment(sketch, "E22.10.0.4", {"start": v(-95.85, -118.5) * mm, "end": v(-95.85, -117.9) * mm});
            skLineSegment(sketch, "E22.10.0.5", {"start": v(-95.85, -123.5) * mm, "end": v(-95.85, -122.9) * mm});
            skLineSegment(sketch, "E22.10.0.6", {"start": v(-99.85, -123.5) * mm, "end": v(-99.85, -122.9) * mm});
            skLineSegment(sketch, "E22.10.0.7", {"start": v(-99.85, -118.5) * mm, "end": v(-99.85, -117.9) * mm});
            skLineSegment(sketch, "E22.10.1.0", {"start": v(-95.85, -75.1) * mm, "end": v(-99.85, -75.1) * mm});
            skLineSegment(sketch, "E22.10.1.1", {"start": v(-95.85, -69.5) * mm, "end": v(-99.85, -69.5) * mm});
            skLineSegment(sketch, "E22.10.1.2", {"start": v(-95.85, -74.5) * mm, "end": v(-99.85, -74.5) * mm});
            skLineSegment(sketch, "E22.10.1.3", {"start": v(-95.85, -70.1) * mm, "end": v(-99.85, -70.1) * mm});
            skLineSegment(sketch, "E22.10.1.4", {"start": v(-95.85, -70.1) * mm, "end": v(-95.85, -69.5) * mm});
            skLineSegment(sketch, "E22.10.1.5", {"start": v(-95.85, -75.1) * mm, "end": v(-95.85, -74.5) * mm});
            skLineSegment(sketch, "E22.10.1.6", {"start": v(-99.85, -75.1) * mm, "end": v(-99.85, -74.5) * mm});
            skLineSegment(sketch, "E22.10.1.7", {"start": v(-99.85, -70.1) * mm, "end": v(-99.85, -69.5) * mm});
            skLineSegment(sketch, "E22.10.2.0", {"start": v(-95.85, -26.7) * mm, "end": v(-99.85, -26.7) * mm});
            skLineSegment(sketch, "E22.10.2.1", {"start": v(-95.85, -21.1) * mm, "end": v(-99.85, -21.1) * mm});
            skLineSegment(sketch, "E22.10.2.2", {"start": v(-95.85, -26.1) * mm, "end": v(-99.85, -26.1) * mm});
            skLineSegment(sketch, "E22.10.2.3", {"start": v(-95.85, -21.7) * mm, "end": v(-99.85, -21.7) * mm});
            skLineSegment(sketch, "E22.10.2.4", {"start": v(-95.85, -21.7) * mm, "end": v(-95.85, -21.1) * mm});
            skLineSegment(sketch, "E22.10.2.5", {"start": v(-95.85, -26.7) * mm, "end": v(-95.85, -26.1) * mm});
            skLineSegment(sketch, "E22.10.2.6", {"start": v(-99.85, -26.7) * mm, "end": v(-99.85, -26.1) * mm});
            skLineSegment(sketch, "E22.10.2.7", {"start": v(-99.85, -21.7) * mm, "end": v(-99.85, -21.1) * mm});
            skLineSegment(sketch, "E22.10.3.0", {"start": v(-95.85, 21.7) * mm, "end": v(-99.85, 21.7) * mm});
            skLineSegment(sketch, "E22.10.3.1", {"start": v(-95.85, 27.3) * mm, "end": v(-99.85, 27.3) * mm});
            skLineSegment(sketch, "E22.10.3.2", {"start": v(-95.85, 22.3) * mm, "end": v(-99.85, 22.3) * mm});
            skLineSegment(sketch, "E22.10.3.3", {"start": v(-95.85, 26.7) * mm, "end": v(-99.85, 26.7) * mm});
            skLineSegment(sketch, "E22.10.3.4", {"start": v(-95.85, 26.7) * mm, "end": v(-95.85, 27.3) * mm});
            skLineSegment(sketch, "E22.10.3.5", {"start": v(-95.85, 21.7) * mm, "end": v(-95.85, 22.3) * mm});
            skLineSegment(sketch, "E22.10.3.6", {"start": v(-99.85, 21.7) * mm, "end": v(-99.85, 22.3) * mm});
            skLineSegment(sketch, "E22.10.3.7", {"start": v(-99.85, 26.7) * mm, "end": v(-99.85, 27.3) * mm});
            skLineSegment(sketch, "E22.10.4.0", {"start": v(-95.85, 70.1) * mm, "end": v(-99.85, 70.1) * mm});
            skLineSegment(sketch, "E22.10.4.1", {"start": v(-95.85, 75.7) * mm, "end": v(-99.85, 75.7) * mm});
            skLineSegment(sketch, "E22.10.4.2", {"start": v(-95.85, 70.7) * mm, "end": v(-99.85, 70.7) * mm});
            skLineSegment(sketch, "E22.10.4.3", {"start": v(-95.85, 75.1) * mm, "end": v(-99.85, 75.1) * mm});
            skLineSegment(sketch, "E22.10.4.4", {"start": v(-95.85, 75.1) * mm, "end": v(-95.85, 75.7) * mm});
            skLineSegment(sketch, "E22.10.4.5", {"start": v(-95.85, 70.1) * mm, "end": v(-95.85, 70.7) * mm});
            skLineSegment(sketch, "E22.10.4.6", {"start": v(-99.85, 70.1) * mm, "end": v(-99.85, 70.7) * mm});
            skLineSegment(sketch, "E22.10.4.7", {"start": v(-99.85, 75.1) * mm, "end": v(-99.85, 75.7) * mm});
            skLineSegment(sketch, "E22.10.5.0", {"start": v(-95.85, 118.5) * mm, "end": v(-99.85, 118.5) * mm});
            skLineSegment(sketch, "E22.10.5.1", {"start": v(-95.85, 124.1) * mm, "end": v(-99.85, 124.1) * mm});
            skLineSegment(sketch, "E22.10.5.2", {"start": v(-95.85, 119.1) * mm, "end": v(-99.85, 119.1) * mm});
            skLineSegment(sketch, "E22.10.5.3", {"start": v(-95.85, 123.5) * mm, "end": v(-99.85, 123.5) * mm});
            skLineSegment(sketch, "E22.10.5.4", {"start": v(-95.85, 123.5) * mm, "end": v(-95.85, 124.1) * mm});
            skLineSegment(sketch, "E22.10.5.5", {"start": v(-95.85, 118.5) * mm, "end": v(-95.85, 119.1) * mm});
            skLineSegment(sketch, "E22.10.5.6", {"start": v(-99.85, 118.5) * mm, "end": v(-99.85, 119.1) * mm});
            skLineSegment(sketch, "E22.10.5.7", {"start": v(-99.85, 123.5) * mm, "end": v(-99.85, 124.1) * mm});
            skLineSegment(sketch, "E22.11.0.0", {"start": v(-123.85, -123.5) * mm, "end": v(-127.85, -123.5) * mm});
            skLineSegment(sketch, "E22.11.0.1", {"start": v(-123.85, -117.9) * mm, "end": v(-127.85, -117.9) * mm});
            skLineSegment(sketch, "E22.11.0.2", {"start": v(-123.85, -122.9) * mm, "end": v(-127.85, -122.9) * mm});
            skLineSegment(sketch, "E22.11.0.3", {"start": v(-123.85, -118.5) * mm, "end": v(-127.85, -118.5) * mm});
            skLineSegment(sketch, "E22.11.0.4", {"start": v(-123.85, -118.5) * mm, "end": v(-123.85, -117.9) * mm});
            skLineSegment(sketch, "E22.11.0.5", {"start": v(-123.85, -123.5) * mm, "end": v(-123.85, -122.9) * mm});
            skLineSegment(sketch, "E22.11.0.6", {"start": v(-127.85, -123.5) * mm, "end": v(-127.85, -122.9) * mm});
            skLineSegment(sketch, "E22.11.0.7", {"start": v(-127.85, -118.5) * mm, "end": v(-127.85, -117.9) * mm});
            skLineSegment(sketch, "E22.11.1.0", {"start": v(-123.85, -75.1) * mm, "end": v(-127.85, -75.1) * mm});
            skLineSegment(sketch, "E22.11.1.1", {"start": v(-123.85, -69.5) * mm, "end": v(-127.85, -69.5) * mm});
            skLineSegment(sketch, "E22.11.1.2", {"start": v(-123.85, -74.5) * mm, "end": v(-127.85, -74.5) * mm});
            skLineSegment(sketch, "E22.11.1.3", {"start": v(-123.85, -70.1) * mm, "end": v(-127.85, -70.1) * mm});
            skLineSegment(sketch, "E22.11.1.4", {"start": v(-123.85, -70.1) * mm, "end": v(-123.85, -69.5) * mm});
            skLineSegment(sketch, "E22.11.1.5", {"start": v(-123.85, -75.1) * mm, "end": v(-123.85, -74.5) * mm});
            skLineSegment(sketch, "E22.11.1.6", {"start": v(-127.85, -75.1) * mm, "end": v(-127.85, -74.5) * mm});
            skLineSegment(sketch, "E22.11.1.7", {"start": v(-127.85, -70.1) * mm, "end": v(-127.85, -69.5) * mm});
            skLineSegment(sketch, "E22.11.2.0", {"start": v(-123.85, -26.7) * mm, "end": v(-127.85, -26.7) * mm});
            skLineSegment(sketch, "E22.11.2.1", {"start": v(-123.85, -21.1) * mm, "end": v(-127.85, -21.1) * mm});
            skLineSegment(sketch, "E22.11.2.2", {"start": v(-123.85, -26.1) * mm, "end": v(-127.85, -26.1) * mm});
            skLineSegment(sketch, "E22.11.2.3", {"start": v(-123.85, -21.7) * mm, "end": v(-127.85, -21.7) * mm});
            skLineSegment(sketch, "E22.11.2.4", {"start": v(-123.85, -21.7) * mm, "end": v(-123.85, -21.1) * mm});
            skLineSegment(sketch, "E22.11.2.5", {"start": v(-123.85, -26.7) * mm, "end": v(-123.85, -26.1) * mm});
            skLineSegment(sketch, "E22.11.2.6", {"start": v(-127.85, -26.7) * mm, "end": v(-127.85, -26.1) * mm});
            skLineSegment(sketch, "E22.11.2.7", {"start": v(-127.85, -21.7) * mm, "end": v(-127.85, -21.1) * mm});
            skLineSegment(sketch, "E22.11.3.0", {"start": v(-123.85, 21.7) * mm, "end": v(-127.85, 21.7) * mm});
            skLineSegment(sketch, "E22.11.3.1", {"start": v(-123.85, 27.3) * mm, "end": v(-127.85, 27.3) * mm});
            skLineSegment(sketch, "E22.11.3.2", {"start": v(-123.85, 22.3) * mm, "end": v(-127.85, 22.3) * mm});
            skLineSegment(sketch, "E22.11.3.3", {"start": v(-123.85, 26.7) * mm, "end": v(-127.85, 26.7) * mm});
            skLineSegment(sketch, "E22.11.3.4", {"start": v(-123.85, 26.7) * mm, "end": v(-123.85, 27.3) * mm});
            skLineSegment(sketch, "E22.11.3.5", {"start": v(-123.85, 21.7) * mm, "end": v(-123.85, 22.3) * mm});
            skLineSegment(sketch, "E22.11.3.6", {"start": v(-127.85, 21.7) * mm, "end": v(-127.85, 22.3) * mm});
            skLineSegment(sketch, "E22.11.3.7", {"start": v(-127.85, 26.7) * mm, "end": v(-127.85, 27.3) * mm});
            skLineSegment(sketch, "E22.11.4.0", {"start": v(-123.85, 70.1) * mm, "end": v(-127.85, 70.1) * mm});
            skLineSegment(sketch, "E22.11.4.1", {"start": v(-123.85, 75.7) * mm, "end": v(-127.85, 75.7) * mm});
            skLineSegment(sketch, "E22.11.4.2", {"start": v(-123.85, 70.7) * mm, "end": v(-127.85, 70.7) * mm});
            skLineSegment(sketch, "E22.11.4.3", {"start": v(-123.85, 75.1) * mm, "end": v(-127.85, 75.1) * mm});
            skLineSegment(sketch, "E22.11.4.4", {"start": v(-123.85, 75.1) * mm, "end": v(-123.85, 75.7) * mm});
            skLineSegment(sketch, "E22.11.4.5", {"start": v(-123.85, 70.1) * mm, "end": v(-123.85, 70.7) * mm});
            skLineSegment(sketch, "E22.11.4.6", {"start": v(-127.85, 70.1) * mm, "end": v(-127.85, 70.7) * mm});
            skLineSegment(sketch, "E22.11.4.7", {"start": v(-127.85, 75.1) * mm, "end": v(-127.85, 75.7) * mm});
            skLineSegment(sketch, "E22.11.5.0", {"start": v(-123.85, 118.5) * mm, "end": v(-127.85, 118.5) * mm});
            skLineSegment(sketch, "E22.11.5.1", {"start": v(-123.85, 124.1) * mm, "end": v(-127.85, 124.1) * mm});
            skLineSegment(sketch, "E22.11.5.2", {"start": v(-123.85, 119.1) * mm, "end": v(-127.85, 119.1) * mm});
            skLineSegment(sketch, "E22.11.5.3", {"start": v(-123.85, 123.5) * mm, "end": v(-127.85, 123.5) * mm});
            skLineSegment(sketch, "E22.11.5.4", {"start": v(-123.85, 123.5) * mm, "end": v(-123.85, 124.1) * mm});
            skLineSegment(sketch, "E22.11.5.5", {"start": v(-123.85, 118.5) * mm, "end": v(-123.85, 119.1) * mm});
            skLineSegment(sketch, "E22.11.5.6", {"start": v(-127.85, 118.5) * mm, "end": v(-127.85, 119.1) * mm});
            skLineSegment(sketch, "E22.11.5.7", {"start": v(-127.85, 123.5) * mm, "end": v(-127.85, 124.1) * mm});
            skLineSegment(sketch, "E22.12.0.0", {"start": v(-151.85, -123.5) * mm, "end": v(-155.85, -123.5) * mm});
            skLineSegment(sketch, "E22.12.0.1", {"start": v(-151.85, -117.9) * mm, "end": v(-155.85, -117.9) * mm});
            skLineSegment(sketch, "E22.12.0.2", {"start": v(-151.85, -122.9) * mm, "end": v(-155.85, -122.9) * mm});
            skLineSegment(sketch, "E22.12.0.3", {"start": v(-151.85, -118.5) * mm, "end": v(-155.85, -118.5) * mm});
            skLineSegment(sketch, "E22.12.0.4", {"start": v(-151.85, -118.5) * mm, "end": v(-151.85, -117.9) * mm});
            skLineSegment(sketch, "E22.12.0.5", {"start": v(-151.85, -123.5) * mm, "end": v(-151.85, -122.9) * mm});
            skLineSegment(sketch, "E22.12.0.6", {"start": v(-155.85, -123.5) * mm, "end": v(-155.85, -122.9) * mm});
            skLineSegment(sketch, "E22.12.0.7", {"start": v(-155.85, -118.5) * mm, "end": v(-155.85, -117.9) * mm});
            skLineSegment(sketch, "E22.12.1.0", {"start": v(-151.85, -75.1) * mm, "end": v(-155.85, -75.1) * mm});
            skLineSegment(sketch, "E22.12.1.1", {"start": v(-151.85, -69.5) * mm, "end": v(-155.85, -69.5) * mm});
            skLineSegment(sketch, "E22.12.1.2", {"start": v(-151.85, -74.5) * mm, "end": v(-155.85, -74.5) * mm});
            skLineSegment(sketch, "E22.12.1.3", {"start": v(-151.85, -70.1) * mm, "end": v(-155.85, -70.1) * mm});
            skLineSegment(sketch, "E22.12.1.4", {"start": v(-151.85, -70.1) * mm, "end": v(-151.85, -69.5) * mm});
            skLineSegment(sketch, "E22.12.1.5", {"start": v(-151.85, -75.1) * mm, "end": v(-151.85, -74.5) * mm});
            skLineSegment(sketch, "E22.12.1.6", {"start": v(-155.85, -75.1) * mm, "end": v(-155.85, -74.5) * mm});
            skLineSegment(sketch, "E22.12.1.7", {"start": v(-155.85, -70.1) * mm, "end": v(-155.85, -69.5) * mm});
            skLineSegment(sketch, "E22.12.2.0", {"start": v(-151.85, -26.7) * mm, "end": v(-155.85, -26.7) * mm});
            skLineSegment(sketch, "E22.12.2.1", {"start": v(-151.85, -21.1) * mm, "end": v(-155.85, -21.1) * mm});
            skLineSegment(sketch, "E22.12.2.2", {"start": v(-151.85, -26.1) * mm, "end": v(-155.85, -26.1) * mm});
            skLineSegment(sketch, "E22.12.2.3", {"start": v(-151.85, -21.7) * mm, "end": v(-155.85, -21.7) * mm});
            skLineSegment(sketch, "E22.12.2.4", {"start": v(-151.85, -21.7) * mm, "end": v(-151.85, -21.1) * mm});
            skLineSegment(sketch, "E22.12.2.5", {"start": v(-151.85, -26.7) * mm, "end": v(-151.85, -26.1) * mm});
            skLineSegment(sketch, "E22.12.2.6", {"start": v(-155.85, -26.7) * mm, "end": v(-155.85, -26.1) * mm});
            skLineSegment(sketch, "E22.12.2.7", {"start": v(-155.85, -21.7) * mm, "end": v(-155.85, -21.1) * mm});
            skLineSegment(sketch, "E22.12.3.0", {"start": v(-151.85, 21.7) * mm, "end": v(-155.85, 21.7) * mm});
            skLineSegment(sketch, "E22.12.3.1", {"start": v(-151.85, 27.3) * mm, "end": v(-155.85, 27.3) * mm});
            skLineSegment(sketch, "E22.12.3.2", {"start": v(-151.85, 22.3) * mm, "end": v(-155.85, 22.3) * mm});
            skLineSegment(sketch, "E22.12.3.3", {"start": v(-151.85, 26.7) * mm, "end": v(-155.85, 26.7) * mm});
            skLineSegment(sketch, "E22.12.3.4", {"start": v(-151.85, 26.7) * mm, "end": v(-151.85, 27.3) * mm});
            skLineSegment(sketch, "E22.12.3.5", {"start": v(-151.85, 21.7) * mm, "end": v(-151.85, 22.3) * mm});
            skLineSegment(sketch, "E22.12.3.6", {"start": v(-155.85, 21.7) * mm, "end": v(-155.85, 22.3) * mm});
            skLineSegment(sketch, "E22.12.3.7", {"start": v(-155.85, 26.7) * mm, "end": v(-155.85, 27.3) * mm});
            skLineSegment(sketch, "E22.12.4.0", {"start": v(-151.85, 70.1) * mm, "end": v(-155.85, 70.1) * mm});
            skLineSegment(sketch, "E22.12.4.1", {"start": v(-151.85, 75.7) * mm, "end": v(-155.85, 75.7) * mm});
            skLineSegment(sketch, "E22.12.4.2", {"start": v(-151.85, 70.7) * mm, "end": v(-155.85, 70.7) * mm});
            skLineSegment(sketch, "E22.12.4.3", {"start": v(-151.85, 75.1) * mm, "end": v(-155.85, 75.1) * mm});
            skLineSegment(sketch, "E22.12.4.4", {"start": v(-151.85, 75.1) * mm, "end": v(-151.85, 75.7) * mm});
            skLineSegment(sketch, "E22.12.4.5", {"start": v(-151.85, 70.1) * mm, "end": v(-151.85, 70.7) * mm});
            skLineSegment(sketch, "E22.12.4.6", {"start": v(-155.85, 70.1) * mm, "end": v(-155.85, 70.7) * mm});
            skLineSegment(sketch, "E22.12.4.7", {"start": v(-155.85, 75.1) * mm, "end": v(-155.85, 75.7) * mm});
            skLineSegment(sketch, "E22.12.5.0", {"start": v(-151.85, 118.5) * mm, "end": v(-155.85, 118.5) * mm});
            skLineSegment(sketch, "E22.12.5.1", {"start": v(-151.85, 124.1) * mm, "end": v(-155.85, 124.1) * mm});
            skLineSegment(sketch, "E22.12.5.2", {"start": v(-151.85, 119.1) * mm, "end": v(-155.85, 119.1) * mm});
            skLineSegment(sketch, "E22.12.5.3", {"start": v(-151.85, 123.5) * mm, "end": v(-155.85, 123.5) * mm});
            skLineSegment(sketch, "E22.12.5.4", {"start": v(-151.85, 123.5) * mm, "end": v(-151.85, 124.1) * mm});
            skLineSegment(sketch, "E22.12.5.5", {"start": v(-151.85, 118.5) * mm, "end": v(-151.85, 119.1) * mm});
            skLineSegment(sketch, "E22.12.5.6", {"start": v(-155.85, 118.5) * mm, "end": v(-155.85, 119.1) * mm});
            skLineSegment(sketch, "E22.12.5.7", {"start": v(-155.85, 123.5) * mm, "end": v(-155.85, 124.1) * mm});
            skLineSegment(sketch, "E22.13.0.0", {"start": v(-179.85, -123.5) * mm, "end": v(-183.85, -123.5) * mm});
            skLineSegment(sketch, "E22.13.0.1", {"start": v(-179.85, -117.9) * mm, "end": v(-183.85, -117.9) * mm});
            skLineSegment(sketch, "E22.13.0.2", {"start": v(-179.85, -122.9) * mm, "end": v(-183.85, -122.9) * mm});
            skLineSegment(sketch, "E22.13.0.3", {"start": v(-179.85, -118.5) * mm, "end": v(-183.85, -118.5) * mm});
            skLineSegment(sketch, "E22.13.0.4", {"start": v(-179.85, -118.5) * mm, "end": v(-179.85, -117.9) * mm});
            skLineSegment(sketch, "E22.13.0.5", {"start": v(-179.85, -123.5) * mm, "end": v(-179.85, -122.9) * mm});
            skLineSegment(sketch, "E22.13.0.6", {"start": v(-183.85, -123.5) * mm, "end": v(-183.85, -122.9) * mm});
            skLineSegment(sketch, "E22.13.0.7", {"start": v(-183.85, -118.5) * mm, "end": v(-183.85, -117.9) * mm});
            skLineSegment(sketch, "E22.13.1.0", {"start": v(-179.85, -75.1) * mm, "end": v(-183.85, -75.1) * mm});
            skLineSegment(sketch, "E22.13.1.1", {"start": v(-179.85, -69.5) * mm, "end": v(-183.85, -69.5) * mm});
            skLineSegment(sketch, "E22.13.1.2", {"start": v(-179.85, -74.5) * mm, "end": v(-183.85, -74.5) * mm});
            skLineSegment(sketch, "E22.13.1.3", {"start": v(-179.85, -70.1) * mm, "end": v(-183.85, -70.1) * mm});
            skLineSegment(sketch, "E22.13.1.4", {"start": v(-179.85, -70.1) * mm, "end": v(-179.85, -69.5) * mm});
            skLineSegment(sketch, "E22.13.1.5", {"start": v(-179.85, -75.1) * mm, "end": v(-179.85, -74.5) * mm});
            skLineSegment(sketch, "E22.13.1.6", {"start": v(-183.85, -75.1) * mm, "end": v(-183.85, -74.5) * mm});
            skLineSegment(sketch, "E22.13.1.7", {"start": v(-183.85, -70.1) * mm, "end": v(-183.85, -69.5) * mm});
            skLineSegment(sketch, "E22.13.2.0", {"start": v(-179.85, -26.7) * mm, "end": v(-183.85, -26.7) * mm});
            skLineSegment(sketch, "E22.13.2.1", {"start": v(-179.85, -21.1) * mm, "end": v(-183.85, -21.1) * mm});
            skLineSegment(sketch, "E22.13.2.2", {"start": v(-179.85, -26.1) * mm, "end": v(-183.85, -26.1) * mm});
            skLineSegment(sketch, "E22.13.2.3", {"start": v(-179.85, -21.7) * mm, "end": v(-183.85, -21.7) * mm});
            skLineSegment(sketch, "E22.13.2.4", {"start": v(-179.85, -21.7) * mm, "end": v(-179.85, -21.1) * mm});
            skLineSegment(sketch, "E22.13.2.5", {"start": v(-179.85, -26.7) * mm, "end": v(-179.85, -26.1) * mm});
            skLineSegment(sketch, "E22.13.2.6", {"start": v(-183.85, -26.7) * mm, "end": v(-183.85, -26.1) * mm});
            skLineSegment(sketch, "E22.13.2.7", {"start": v(-183.85, -21.7) * mm, "end": v(-183.85, -21.1) * mm});
            skLineSegment(sketch, "E22.13.3.0", {"start": v(-179.85, 21.7) * mm, "end": v(-183.85, 21.7) * mm});
            skLineSegment(sketch, "E22.13.3.1", {"start": v(-179.85, 27.3) * mm, "end": v(-183.85, 27.3) * mm});
            skLineSegment(sketch, "E22.13.3.2", {"start": v(-179.85, 22.3) * mm, "end": v(-183.85, 22.3) * mm});
            skLineSegment(sketch, "E22.13.3.3", {"start": v(-179.85, 26.7) * mm, "end": v(-183.85, 26.7) * mm});
            skLineSegment(sketch, "E22.13.3.4", {"start": v(-179.85, 26.7) * mm, "end": v(-179.85, 27.3) * mm});
            skLineSegment(sketch, "E22.13.3.5", {"start": v(-179.85, 21.7) * mm, "end": v(-179.85, 22.3) * mm});
            skLineSegment(sketch, "E22.13.3.6", {"start": v(-183.85, 21.7) * mm, "end": v(-183.85, 22.3) * mm});
            skLineSegment(sketch, "E22.13.3.7", {"start": v(-183.85, 26.7) * mm, "end": v(-183.85, 27.3) * mm});
            skLineSegment(sketch, "E22.13.4.0", {"start": v(-179.85, 70.1) * mm, "end": v(-183.85, 70.1) * mm});
            skLineSegment(sketch, "E22.13.4.1", {"start": v(-179.85, 75.7) * mm, "end": v(-183.85, 75.7) * mm});
            skLineSegment(sketch, "E22.13.4.2", {"start": v(-179.85, 70.7) * mm, "end": v(-183.85, 70.7) * mm});
            skLineSegment(sketch, "E22.13.4.3", {"start": v(-179.85, 75.1) * mm, "end": v(-183.85, 75.1) * mm});
            skLineSegment(sketch, "E22.13.4.4", {"start": v(-179.85, 75.1) * mm, "end": v(-179.85, 75.7) * mm});
            skLineSegment(sketch, "E22.13.4.5", {"start": v(-179.85, 70.1) * mm, "end": v(-179.85, 70.7) * mm});
            skLineSegment(sketch, "E22.13.4.6", {"start": v(-183.85, 70.1) * mm, "end": v(-183.85, 70.7) * mm});
            skLineSegment(sketch, "E22.13.4.7", {"start": v(-183.85, 75.1) * mm, "end": v(-183.85, 75.7) * mm});
            skLineSegment(sketch, "E22.13.5.0", {"start": v(-179.85, 118.5) * mm, "end": v(-183.85, 118.5) * mm});
            skLineSegment(sketch, "E22.13.5.1", {"start": v(-179.85, 124.1) * mm, "end": v(-183.85, 124.1) * mm});
            skLineSegment(sketch, "E22.13.5.2", {"start": v(-179.85, 119.1) * mm, "end": v(-183.85, 119.1) * mm});
            skLineSegment(sketch, "E22.13.5.3", {"start": v(-179.85, 123.5) * mm, "end": v(-183.85, 123.5) * mm});
            skLineSegment(sketch, "E22.13.5.4", {"start": v(-179.85, 123.5) * mm, "end": v(-179.85, 124.1) * mm});
            skLineSegment(sketch, "E22.13.5.5", {"start": v(-179.85, 118.5) * mm, "end": v(-179.85, 119.1) * mm});
            skLineSegment(sketch, "E22.13.5.6", {"start": v(-183.85, 118.5) * mm, "end": v(-183.85, 119.1) * mm});
            skLineSegment(sketch, "E22.13.5.7", {"start": v(-183.85, 123.5) * mm, "end": v(-183.85, 124.1) * mm});
            skLineSegment(sketch, "E22.direction1", {"start": v(180.15, -123.5) * mm, "end": v(152.15, -123.5) * mm, "construction": true});
            skLineSegment(sketch, "E22.direction2", {"start": v(180.15, -123.5) * mm, "end": v(180.15, -75.1) * mm, "construction": true});
            skSolve(sketch);
        }
        {
            var Q0;
            Q0 = qSketchRegion(id + "F2", true);
            extrude(context, id + "F3", {"entities" : qUnion([Q0]), "depth" : 1 * mm, "offsetDistance" : 25 * mm});
        }
    });
